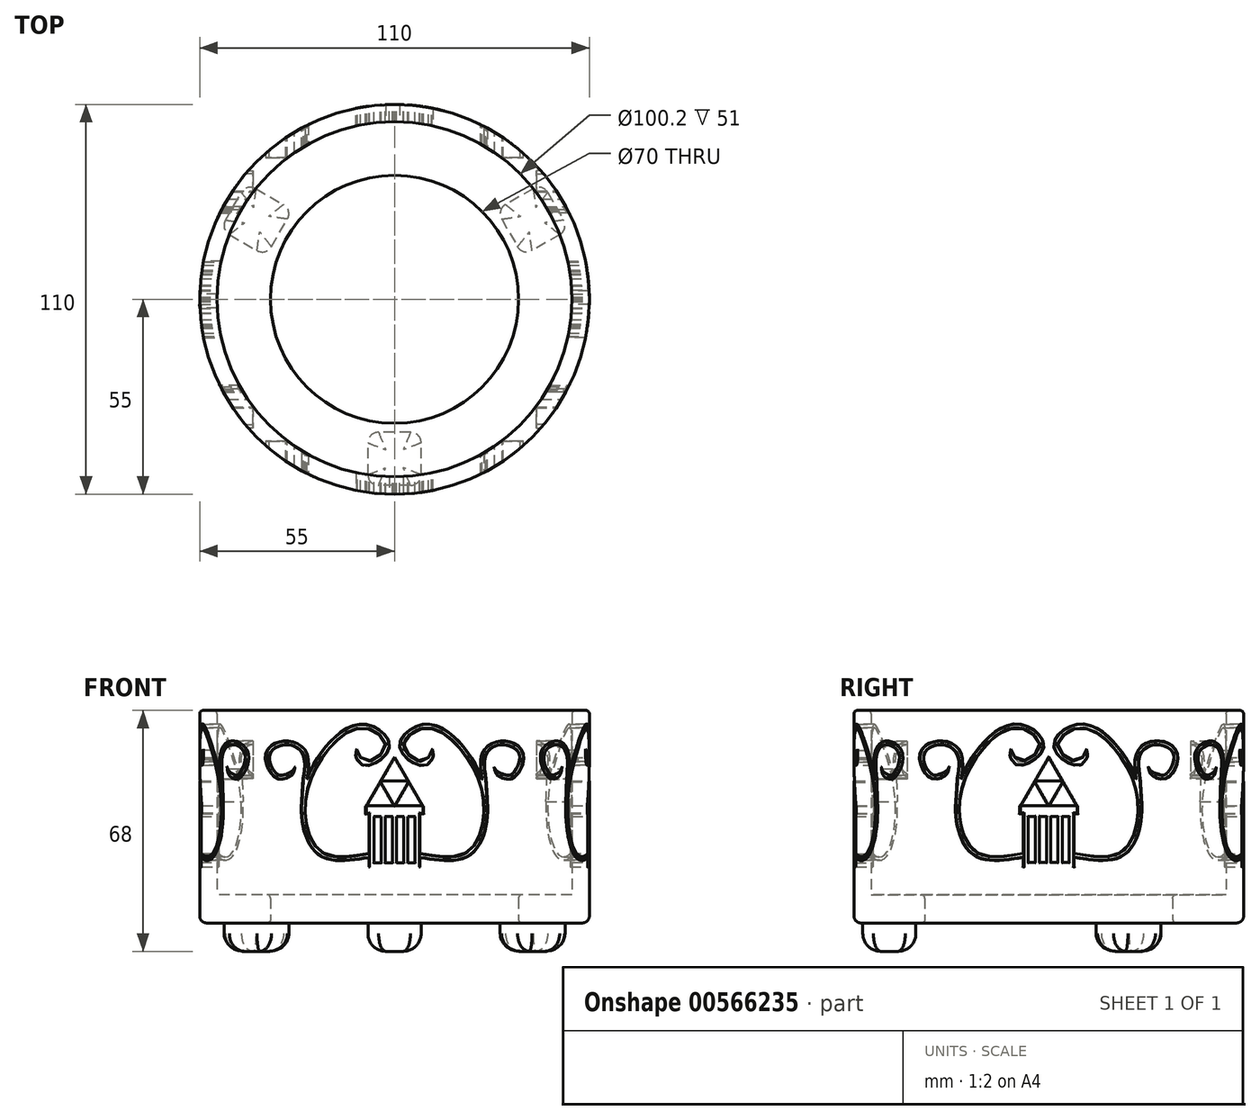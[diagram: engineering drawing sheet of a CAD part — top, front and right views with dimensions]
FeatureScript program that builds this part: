
annotation { "Feature Type Name" : "Feature", "Feature Type Description" : "" }
export const myFeature = defineFeature(function(context is Context, id is Id, definition is map)
    precondition{}
    {
        {
            var Q0;
            Q0=qCreatedBy(makeId("Top.planeOp"),FACE);
            var sketch = newSketch(context, id + "F0", { "sketchPlane" : qUnion([Q0])});
            skCircle(sketch, "E0", {"center": v(0, 0) * mm, "radius": 50.1 * mm});
            skCircle(sketch, "E1", {"center": v(0, 0) * mm, "radius": 55 * mm});
            skCircle(sketch, "E2", {"center": v(0, 0) * mm, "radius": 35 * mm});
            skLineSegment(sketch, "E3", {"start": v(0, -35) * mm, "end": v(0, -45) * mm, "construction": true});
            skLineSegment(sketch, "E4.bottom", {"start": v(4.5, -52.5) * mm, "end": v(-4.5, -52.5) * mm});
            skLineSegment(sketch, "E4.top", {"start": v(4.5, -37.5) * mm, "end": v(-4.5, -37.5) * mm});
            skLineSegment(sketch, "E4.left", {"start": v(7.5, -49.5) * mm, "end": v(7.5, -40.5) * mm});
            skLineSegment(sketch, "E4.right", {"start": v(-7.5, -49.5) * mm, "end": v(-7.5, -40.5) * mm});
            skPoint(sketch, "E4.middle", {"position": v(0, -45) * mm});
            skPoint(sketch, "E5.visualSharp", {"position": v(-7.5, -37.5) * mm});
            skArc(sketch, "E5.filletArc", {"start": v(-4.5, -37.5) * mm, "mid": v(-6.62, -38.38) * mm, "end": v(-7.5, -40.5) * mm});
            skPoint(sketch, "E6.visualSharp", {"position": v(7.5, -37.5) * mm});
            skArc(sketch, "E6.filletArc", {"start": v(7.5, -40.5) * mm, "mid": v(6.62, -38.38) * mm, "end": v(4.5, -37.5) * mm});
            skPoint(sketch, "E7.visualSharp", {"position": v(7.5, -52.5) * mm});
            skArc(sketch, "E7.filletArc", {"start": v(4.5, -52.5) * mm, "mid": v(6.62, -51.62) * mm, "end": v(7.5, -49.5) * mm});
            skPoint(sketch, "E8.visualSharp", {"position": v(-7.5, -52.5) * mm});
            skArc(sketch, "E8.filletArc", {"start": v(-7.5, -49.5) * mm, "mid": v(-6.62, -51.62) * mm, "end": v(-4.5, -52.5) * mm});
            skLineSegment(sketch, "E9.1.0", {"start": v(46.62, 18.25) * mm, "end": v(38.82, 13.75) * mm});
            skArc(sketch, "E9.1.1", {"start": v(34.73, 14.85) * mm, "mid": v(36.55, 13.46) * mm, "end": v(38.82, 13.75) * mm});
            skLineSegment(sketch, "E9.1.2", {"start": v(30.23, 22.65) * mm, "end": v(34.73, 14.85) * mm});
            skArc(sketch, "E9.1.3", {"start": v(31.32, 26.75) * mm, "mid": v(29.93, 24.92) * mm, "end": v(30.23, 22.65) * mm});
            skLineSegment(sketch, "E9.1.4", {"start": v(39.12, 31.25) * mm, "end": v(31.32, 26.75) * mm});
            skArc(sketch, "E9.1.5", {"start": v(43.22, 30.15) * mm, "mid": v(41.4, 31.54) * mm, "end": v(39.12, 31.25) * mm});
            skLineSegment(sketch, "E9.1.6", {"start": v(43.22, 30.15) * mm, "end": v(47.72, 22.35) * mm});
            skArc(sketch, "E9.1.7", {"start": v(46.62, 18.25) * mm, "mid": v(48.02, 20.08) * mm, "end": v(47.72, 22.35) * mm});
            skLineSegment(sketch, "E9.2.0", {"start": v(-39.12, 31.25) * mm, "end": v(-31.32, 26.75) * mm});
            skArc(sketch, "E9.2.1", {"start": v(-30.23, 22.65) * mm, "mid": v(-29.93, 24.92) * mm, "end": v(-31.32, 26.75) * mm});
            skLineSegment(sketch, "E9.2.2", {"start": v(-34.73, 14.85) * mm, "end": v(-30.23, 22.65) * mm});
            skArc(sketch, "E9.2.3", {"start": v(-38.82, 13.75) * mm, "mid": v(-36.55, 13.46) * mm, "end": v(-34.73, 14.85) * mm});
            skLineSegment(sketch, "E9.2.4", {"start": v(-46.62, 18.25) * mm, "end": v(-38.82, 13.75) * mm});
            skArc(sketch, "E9.2.5", {"start": v(-47.72, 22.35) * mm, "mid": v(-48.02, 20.08) * mm, "end": v(-46.62, 18.25) * mm});
            skLineSegment(sketch, "E9.2.6", {"start": v(-47.72, 22.35) * mm, "end": v(-43.22, 30.15) * mm});
            skArc(sketch, "E9.2.7", {"start": v(-39.12, 31.25) * mm, "mid": v(-41.4, 31.54) * mm, "end": v(-43.22, 30.15) * mm});
            skSolve(sketch);
        }
        {
            var Q0;
            Q0=makeQuery(id+"F0.imprint","IMPRINT",FACE,{"disambiguationData":[TD([[makeQuery(id+"F0.imprint","IMPRINT",EDGE,{"derivedFrom":sQuery(id+"F0.wireOp",EDGE,"E0")}),-1.0]])]});
            var Q1;
            {var subQ5=sQuery(id+"F0.wireOp",EDGE,"E9.2.6");Q1=makeQuery(id+"F0.imprint","IMPRINT",FACE,{"disambiguationData":[TD([[makeQuery(id+"F0.imprint","IMPRINT",EDGE,{"derivedFrom":subQ5}),-1.0]])]});}
            var Q2;
            {var subQ5=sQuery(id+"F0.wireOp",EDGE,"E9.1.6");Q2=makeQuery(id+"F0.imprint","IMPRINT",FACE,{"disambiguationData":[TD([[makeQuery(id+"F0.imprint","IMPRINT",EDGE,{"derivedFrom":subQ5}),-1.0]])]});}
            var Q3;
            {var subQ5=sQuery(id+"F0.wireOp",EDGE,"E4.bottom");Q3=makeQuery(id+"F0.imprint","IMPRINT",FACE,{"disambiguationData":[TD([[makeQuery(id+"F0.imprint","IMPRINT",EDGE,{"derivedFrom":subQ5}),-1.0]])]});}
            extrude(context, id + "F1", {"entities" : qUnion([Q0, Q1, Q2, Q3]), "depth" : 60 * mm, "offsetDistance" : 25 * mm});
        }
        {
            var Q0;
            Q0=makeQuery(id+"F0.imprint","IMPRINT",FACE,{"disambiguationData":[TD([[makeQuery(id+"F0.imprint","IMPRINT",EDGE,{"derivedFrom":sQuery(id+"F0.wireOp",EDGE,"E0")}),1.0]])]});
            var Q1;
            {var subQ0=sQuery(id+"F0.wireOp",EDGE,"E9.1.0");Q1=makeQuery(id+"F0.imprint","IMPRINT",FACE,{"disambiguationData":[TD([[makeQuery(id+"F0.imprint","IMPRINT",EDGE,{"derivedFrom":subQ0}),-1.0]])]});}
            var Q2;
            {var subQ0=sQuery(id+"F0.wireOp",EDGE,"E9.2.0");Q2=makeQuery(id+"F0.imprint","IMPRINT",FACE,{"disambiguationData":[TD([[makeQuery(id+"F0.imprint","IMPRINT",EDGE,{"derivedFrom":subQ0}),-1.0]])]});}
            var Q3;
            Q3=makeQuery(id+"F0.imprint","IMPRINT",FACE,{"disambiguationData":[TD([[makeQuery(id+"F0.imprint","IMPRINT",EDGE,{"derivedFrom":sQuery(id+"F0.wireOp",EDGE,"E4.top")}),1.0]])]});
            extrude(context, id + "F2", {"entities" : qUnion([Q0, Q1, Q2, Q3]), "operationType" : NewBodyOperationType.ADD, "depth" : 8 * mm, "offsetDistance" : 25 * mm});
        }
        {
            var Q0;
            Q0=qCreatedBy(makeId("Front.planeOp"),FACE);
            var sketch = newSketch(context, id + "F3", { "sketchPlane" : qUnion([Q0])});
            skLineSegment(sketch, "E10", {"start": v(0, 46.86) * mm, "end": v(4, 39.93) * mm});
            skLineSegment(sketch, "E11", {"start": v(4, 39.93) * mm, "end": v(-4, 39.93) * mm});
            skLineSegment(sketch, "E12", {"start": v(-4, 39.93) * mm, "end": v(0, 46.86) * mm});
            skLineSegment(sketch, "E13", {"start": v(4, 39.93) * mm, "end": v(0, 33) * mm});
            skLineSegment(sketch, "E14", {"start": v(0, 33) * mm, "end": v(8, 33) * mm});
            skLineSegment(sketch, "E15", {"start": v(8, 33) * mm, "end": v(4, 39.93) * mm});
            skLineSegment(sketch, "E16", {"start": v(-4, 39.93) * mm, "end": v(0, 33) * mm});
            skLineSegment(sketch, "E17", {"start": v(-8, 33) * mm, "end": v(-4, 39.93) * mm});
            skLineSegment(sketch, "E18", {"start": v(0, 33) * mm, "end": v(-8, 33) * mm});
            skLineSegment(sketch, "E19", {"start": v(-8, 33) * mm, "end": v(-8, 31) * mm});
            skLineSegment(sketch, "E20", {"start": v(8, 31) * mm, "end": v(8, 33) * mm});
            skLineSegment(sketch, "E21", {"start": v(7, 31) * mm, "end": v(7, 16) * mm});
            skLineSegment(sketch, "E22", {"start": v(7, 16) * mm, "end": v(-7, 16) * mm});
            skLineSegment(sketch, "E23", {"start": v(-7, 16) * mm, "end": v(-7, 31) * mm});
            skLineSegment(sketch, "E24.bottom", {"start": v(5.8, 30) * mm, "end": v(3.8, 30) * mm});
            skLineSegment(sketch, "E24.top", {"start": v(5.8, 17) * mm, "end": v(3.8, 17) * mm});
            skLineSegment(sketch, "E24.left", {"start": v(5.8, 30) * mm, "end": v(5.8, 17) * mm});
            skLineSegment(sketch, "E24.right", {"start": v(3.8, 30) * mm, "end": v(3.8, 17) * mm});
            skLineSegment(sketch, "E25.bottom", {"start": v(2.6, 17) * mm, "end": v(0.6, 17) * mm});
            skLineSegment(sketch, "E25.top", {"start": v(2.6, 30) * mm, "end": v(0.6, 30) * mm});
            skLineSegment(sketch, "E25.left", {"start": v(2.6, 17) * mm, "end": v(2.6, 30) * mm});
            skLineSegment(sketch, "E25.right", {"start": v(0.6, 17) * mm, "end": v(0.6, 30) * mm});
            skLineSegment(sketch, "E26.top", {"start": v(-0.6, 30) * mm, "end": v(-2.6, 30) * mm});
            skLineSegment(sketch, "E26.right", {"start": v(-2.6, 17) * mm, "end": v(-2.6, 30) * mm});
            skLineSegment(sketch, "E27.bottom", {"start": v(-3.8, 17) * mm, "end": v(-5.8, 17) * mm});
            skLineSegment(sketch, "E27.top", {"start": v(-3.8, 30) * mm, "end": v(-5.8, 30) * mm});
            skLineSegment(sketch, "E27.left", {"start": v(-3.8, 17) * mm, "end": v(-3.8, 30) * mm});
            skLineSegment(sketch, "E27.right", {"start": v(-5.8, 17) * mm, "end": v(-5.8, 30) * mm});
            skLineSegment(sketch, "E28", {"start": v(-0.6, 30) * mm, "end": v(-0.6, 17) * mm});
            skLineSegment(sketch, "E29", {"start": v(-0.6, 17) * mm, "end": v(-2.6, 17) * mm});
            skFitSpline(sketch, "E30", {"points": [v(7, 18.58) * mm, v(21.25, 19.27) * mm, v(26.2, 32.82) * mm, v(20.55, 48.14) * mm, v(8.79, 56.05) * mm, v(1.47, 50.51) * mm, v(4.83, 45.57) * mm, v(8.99, 44.58) * mm, v(10.47, 46.16) * mm], "startDerivative": vector(104.29, -16.9) * mm, "endDerivative": vector(19.37, 32.84) * mm});
            skFitSpline(sketch, "E31.0", {"points": [v(7.16, 19.56) * mm, v(8.25, 19.39) * mm, v(10.4, 19.04) * mm, v(13.5, 18.68) * mm, v(15.87, 18.66) * mm, v(17.58, 18.86) * mm, v(18.76, 19.14) * mm, v(19.82, 19.55) * mm, v(20.77, 20.12) * mm, v(21.63, 20.86) * mm, v(22.4, 21.78) * mm, v(23.1, 22.87) * mm, v(23.9, 24.5) * mm, v(24.66, 26.83) * mm, v(25.16, 29.89) * mm, v(25.25, 33) * mm, v(24.95, 36) * mm, v(24.27, 38.89) * mm, v(23.24, 41.67) * mm, v(21.9, 44.36) * mm, v(20.23, 46.96) * mm, v(18.29, 49.47) * mm, v(16.14, 51.74) * mm, v(14.23, 53.25) * mm, v(12.68, 54.16) * mm, v(11.52, 54.66) * mm, v(10.37, 54.98) * mm, v(9.43, 55.08) * mm, v(8.68, 55.05) * mm, v(7.92, 54.95) * mm, v(6.97, 54.7) * mm, v(5.87, 54.23) * mm, v(4.85, 53.6) * mm, v(3.96, 52.88) * mm, v(3.24, 52.1) * mm, v(2.73, 51.3) * mm, v(2.5, 50.68) * mm, v(2.44, 50.25) * mm, v(2.44, 49.83) * mm, v(2.56, 49.3) * mm, v(2.89, 48.64) * mm, v(3.56, 47.75) * mm, v(4.52, 46.94) * mm, v(5.57, 46.28) * mm, v(6.35, 45.9) * mm, v(7.09, 45.62) * mm, v(7.75, 45.47) * mm, v(8.2, 45.44) * mm, v(8.46, 45.47) * mm, v(8.61, 45.5) * mm, v(8.72, 45.55) * mm, v(8.86, 45.64) * mm, v(9.06, 45.82) * mm, v(9.32, 46.18) * mm, v(9.5, 46.5) * mm, v(9.6, 46.67) * mm]});
            skLineSegment(sketch, "E32", {"start": v(7.16, 19.56) * mm, "end": v(7, 19.94) * mm});
            skFitSpline(sketch, "E33", {"points": [v(10.47, 46.16) * mm, v(10.82, 47.06) * mm, v(10.61, 48.76) * mm], "startDerivative": vector(0.97, 1.8) * mm, "endDerivative": vector(-0.49, 2.17) * mm});
            skLineSegment(sketch, "E34", {"start": v(10.61, 48.76) * mm, "end": v(9.6, 46.67) * mm});
            skFitSpline(sketch, "E35", {"points": [v(25.01, 29.21) * mm, v(16.42, 37.92) * mm, v(12, 34.2) * mm, v(11.36, 25.97) * mm, v(17.98, 23.01) * mm, v(21.05, 29.47) * mm, v(15.1, 29.83) * mm], "startDerivative": vector(-33.14, 93.73) * mm, "endDerivative": vector(-8.06, -72.83) * mm});
            skFitSpline(sketch, "E36.0", {"points": [v(24.07, 28.88) * mm, v(23.4, 30.77) * mm, v(21.88, 33.78) * mm, v(19.82, 35.87) * mm, v(18.28, 36.7) * mm, v(17.22, 36.97) * mm, v(16.28, 36.93) * mm, v(15.43, 36.65) * mm, v(14.61, 36.1) * mm, v(13.84, 35.29) * mm, v(13.13, 34.24) * mm, v(12.5, 32.98) * mm, v(12.02, 31.6) * mm, v(11.7, 30.18) * mm, v(11.63, 28.78) * mm, v(11.77, 27.7) * mm, v(12.02, 26.9) * mm, v(12.27, 26.36) * mm, v(12.6, 25.84) * mm, v(13.15, 25.2) * mm, v(14, 24.5) * mm, v(15.16, 23.95) * mm, v(16.17, 23.76) * mm, v(16.95, 23.78) * mm, v(17.52, 23.9) * mm, v(18.07, 24.11) * mm, v(18.62, 24.43) * mm, v(19.14, 24.84) * mm, v(19.75, 25.48) * mm, v(20.22, 26.24) * mm, v(20.47, 27.01) * mm, v(20.55, 27.58) * mm, v(20.52, 28.13) * mm, v(20.36, 28.66) * mm, v(20.07, 29.18) * mm, v(19.6, 29.73) * mm, v(19.01, 30.21) * mm, v(18.35, 30.6) * mm, v(17.7, 30.84) * mm, v(17.12, 30.93) * mm, v(16.78, 30.87) * mm, v(16.6, 30.79) * mm, v(16.48, 30.7) * mm, v(16.37, 30.59) * mm, v(16.22, 30.34) * mm, v(16.13, 30.02) * mm, v(16.1, 29.72) * mm]});
            skFitSpline(sketch, "E37", {"points": [v(15.1, 29.83) * mm, v(15.1, 28.54) * mm, v(15.68, 27.75) * mm], "startDerivative": vector(-0.33, -2.62) * mm, "endDerivative": vector(1.54, -1.53) * mm});
            skLineSegment(sketch, "E38", {"start": v(16.1, 29.72) * mm, "end": v(15.68, 27.75) * mm});
            skLineSegment(sketch, "E39", {"start": v(24.02, 29.03) * mm, "end": v(24.65, 27.14) * mm});
            skFitSpline(sketch, "E40", {"points": [v(24.7, 40.55) * mm, v(25.08, 48.45) * mm, v(30.9, 51.3) * mm, v(36.26, 47.6) * mm, v(33.52, 41.03) * mm, v(30.36, 40.96) * mm], "startDerivative": vector(-5.16, 38.6) * mm, "endDerivative": vector(-21.83, 6.32) * mm});
            skFitSpline(sketch, "E41.0", {"points": [v(25.7, 40.68) * mm, v(25.6, 41.49) * mm, v(25.38, 43.08) * mm, v(25.25, 45.26) * mm, v(25.45, 46.79) * mm, v(25.78, 47.66) * mm, v(26.03, 48.1) * mm, v(26.32, 48.51) * mm, v(26.78, 49) * mm, v(27.7, 49.66) * mm, v(28.8, 50.12) * mm, v(30.03, 50.31) * mm, v(30.96, 50.32) * mm, v(31.9, 50.18) * mm, v(32.82, 49.9) * mm, v(33.64, 49.5) * mm, v(34.33, 48.99) * mm, v(34.86, 48.4) * mm, v(35.15, 47.85) * mm, v(35.29, 47.38) * mm, v(35.36, 46.86) * mm, v(35.34, 46.12) * mm, v(35.13, 45.14) * mm, v(34.76, 44.17) * mm, v(34.27, 43.27) * mm, v(33.8, 42.64) * mm, v(33.44, 42.24) * mm, v(33.17, 42) * mm, v(32.93, 41.84) * mm, v(32.64, 41.7) * mm, v(32.31, 41.62) * mm, v(31.85, 41.62) * mm, v(31.3, 41.73) * mm, v(30.86, 41.85) * mm, v(30.63, 41.92) * mm]});
            skFitSpline(sketch, "E42", {"points": [v(30.36, 40.96) * mm, v(28.83, 41.98) * mm, v(28.24, 43.52) * mm], "startDerivative": vector(-3.42, 1.69) * mm, "endDerivative": vector(-0.79, 3.45) * mm});
            skFitSpline(sketch, "E43", {"points": [v(30.63, 41.92) * mm, v(28.87, 42.76) * mm, v(28.24, 43.52) * mm], "startDerivative": vector(-3.46, 1.32) * mm, "endDerivative": vector(-1.2, 1.92) * mm});
            skLineSegment(sketch, "E44", {"start": v(25.7, 40.68) * mm, "end": v(26.12, 34.19) * mm});
            skLineSegment(sketch, "E45.MirrorCS", {"start": v(-7.16, 19.56) * mm, "end": v(-7, 19.94) * mm});
            skLineSegment(sketch, "E46.MirrorCS", {"start": v(-16.1, 29.72) * mm, "end": v(-15.68, 27.75) * mm});
            skFitSpline(sketch, "E47.MirrorCS", {"points": [v(-15.1, 29.83) * mm, v(-15.1, 28.54) * mm, v(-15.68, 27.75) * mm], "startDerivative": vector(0.33, -2.62) * mm, "endDerivative": vector(-1.54, -1.53) * mm});
            skLineSegment(sketch, "E48.MirrorCS", {"start": v(-24.02, 29.03) * mm, "end": v(-24.65, 27.14) * mm});
            skFitSpline(sketch, "E49.MirrorCS", {"points": [v(-25.01, 29.21) * mm, v(-16.42, 37.92) * mm, v(-12, 34.2) * mm, v(-11.36, 25.97) * mm, v(-17.98, 23.01) * mm, v(-21.05, 29.47) * mm, v(-15.1, 29.83) * mm], "startDerivative": vector(33.14, 93.73) * mm, "endDerivative": vector(8.06, -72.83) * mm});
            skFitSpline(sketch, "E50.MirrorCS", {"points": [v(-10.47, 46.16) * mm, v(-10.82, 47.06) * mm, v(-10.61, 48.76) * mm], "startDerivative": vector(-0.97, 1.8) * mm, "endDerivative": vector(0.49, 2.17) * mm});
            skLineSegment(sketch, "E51.MirrorCS", {"start": v(-25.7, 40.68) * mm, "end": v(-26.12, 34.19) * mm});
            skLineSegment(sketch, "E52.MirrorCS", {"start": v(-10.61, 48.76) * mm, "end": v(-9.6, 46.67) * mm});
            skFitSpline(sketch, "E53.MirrorCS", {"points": [v(-30.36, 40.96) * mm, v(-28.83, 41.98) * mm, v(-28.24, 43.52) * mm], "startDerivative": vector(3.42, 1.69) * mm, "endDerivative": vector(0.79, 3.45) * mm});
            skFitSpline(sketch, "E54.MirrorCS", {"points": [v(-30.63, 41.92) * mm, v(-28.87, 42.76) * mm, v(-28.24, 43.52) * mm], "startDerivative": vector(3.46, 1.32) * mm, "endDerivative": vector(1.2, 1.92) * mm});
            skFitSpline(sketch, "E55.MirrorCS", {"points": [v(-24.7, 40.55) * mm, v(-25.08, 48.45) * mm, v(-30.9, 51.3) * mm, v(-36.26, 47.6) * mm, v(-33.52, 41.03) * mm, v(-30.36, 40.96) * mm], "startDerivative": vector(5.16, 38.6) * mm, "endDerivative": vector(21.83, 6.32) * mm});
            skFitSpline(sketch, "E56.MirrorCS", {"points": [v(-7, 18.58) * mm, v(-21.25, 19.27) * mm, v(-26.2, 32.82) * mm, v(-20.55, 48.14) * mm, v(-8.79, 56.05) * mm, v(-1.47, 50.51) * mm, v(-4.83, 45.57) * mm, v(-8.99, 44.58) * mm, v(-10.47, 46.16) * mm], "startDerivative": vector(-104.29, -16.9) * mm, "endDerivative": vector(-19.37, 32.84) * mm});
            skFitSpline(sketch, "E57.0", {"points": [v(-7.16, 19.56) * mm, v(-8.25, 19.39) * mm, v(-10.4, 19.04) * mm, v(-13.5, 18.68) * mm, v(-15.87, 18.66) * mm, v(-17.58, 18.86) * mm, v(-18.76, 19.14) * mm, v(-19.82, 19.55) * mm, v(-20.77, 20.12) * mm, v(-21.63, 20.86) * mm, v(-22.4, 21.78) * mm, v(-23.1, 22.87) * mm, v(-23.9, 24.5) * mm, v(-24.66, 26.83) * mm, v(-25.16, 29.89) * mm, v(-25.25, 33) * mm, v(-24.95, 36) * mm, v(-24.27, 38.89) * mm, v(-23.24, 41.67) * mm, v(-21.9, 44.36) * mm, v(-20.23, 46.96) * mm, v(-18.29, 49.47) * mm, v(-16.14, 51.74) * mm, v(-14.23, 53.25) * mm, v(-12.68, 54.16) * mm, v(-11.52, 54.66) * mm, v(-10.37, 54.98) * mm, v(-9.43, 55.08) * mm, v(-8.68, 55.05) * mm, v(-7.92, 54.95) * mm, v(-6.97, 54.7) * mm, v(-5.87, 54.23) * mm, v(-4.85, 53.6) * mm, v(-3.96, 52.88) * mm, v(-3.24, 52.1) * mm, v(-2.73, 51.3) * mm, v(-2.5, 50.68) * mm, v(-2.44, 50.25) * mm, v(-2.44, 49.83) * mm, v(-2.56, 49.3) * mm, v(-2.89, 48.64) * mm, v(-3.56, 47.75) * mm, v(-4.52, 46.94) * mm, v(-5.57, 46.28) * mm, v(-6.35, 45.9) * mm, v(-7.09, 45.62) * mm, v(-7.75, 45.47) * mm, v(-8.2, 45.44) * mm, v(-8.46, 45.47) * mm, v(-8.61, 45.5) * mm, v(-8.72, 45.55) * mm, v(-8.86, 45.64) * mm, v(-9.06, 45.82) * mm, v(-9.32, 46.18) * mm, v(-9.5, 46.5) * mm, v(-9.6, 46.67) * mm]});
            skFitSpline(sketch, "E58.0", {"points": [v(-24.07, 28.88) * mm, v(-23.4, 30.77) * mm, v(-21.88, 33.78) * mm, v(-19.82, 35.87) * mm, v(-18.28, 36.7) * mm, v(-17.22, 36.97) * mm, v(-16.28, 36.93) * mm, v(-15.43, 36.65) * mm, v(-14.61, 36.1) * mm, v(-13.84, 35.29) * mm, v(-13.13, 34.24) * mm, v(-12.5, 32.98) * mm, v(-12.02, 31.6) * mm, v(-11.7, 30.18) * mm, v(-11.63, 28.78) * mm, v(-11.77, 27.7) * mm, v(-12.02, 26.9) * mm, v(-12.27, 26.36) * mm, v(-12.6, 25.84) * mm, v(-13.15, 25.2) * mm, v(-14, 24.5) * mm, v(-15.16, 23.95) * mm, v(-16.17, 23.76) * mm, v(-16.95, 23.78) * mm, v(-17.52, 23.9) * mm, v(-18.07, 24.11) * mm, v(-18.62, 24.43) * mm, v(-19.14, 24.84) * mm, v(-19.75, 25.48) * mm, v(-20.22, 26.24) * mm, v(-20.47, 27.01) * mm, v(-20.55, 27.58) * mm, v(-20.52, 28.13) * mm, v(-20.36, 28.66) * mm, v(-20.07, 29.18) * mm, v(-19.6, 29.73) * mm, v(-19.01, 30.21) * mm, v(-18.35, 30.6) * mm, v(-17.7, 30.84) * mm, v(-17.12, 30.93) * mm, v(-16.78, 30.87) * mm, v(-16.6, 30.79) * mm, v(-16.48, 30.7) * mm, v(-16.37, 30.59) * mm, v(-16.22, 30.34) * mm, v(-16.13, 30.02) * mm, v(-16.1, 29.72) * mm]});
            skFitSpline(sketch, "E59.0", {"points": [v(-25.7, 40.68) * mm, v(-25.6, 41.49) * mm, v(-25.38, 43.08) * mm, v(-25.25, 45.26) * mm, v(-25.45, 46.79) * mm, v(-25.78, 47.66) * mm, v(-26.03, 48.1) * mm, v(-26.32, 48.51) * mm, v(-26.78, 49) * mm, v(-27.7, 49.66) * mm, v(-28.8, 50.12) * mm, v(-30.03, 50.31) * mm, v(-30.96, 50.32) * mm, v(-31.9, 50.18) * mm, v(-32.82, 49.9) * mm, v(-33.64, 49.5) * mm, v(-34.33, 48.99) * mm, v(-34.86, 48.4) * mm, v(-35.15, 47.85) * mm, v(-35.29, 47.38) * mm, v(-35.36, 46.86) * mm, v(-35.34, 46.12) * mm, v(-35.13, 45.14) * mm, v(-34.76, 44.17) * mm, v(-34.27, 43.27) * mm, v(-33.8, 42.64) * mm, v(-33.44, 42.24) * mm, v(-33.17, 42) * mm, v(-32.93, 41.84) * mm, v(-32.64, 41.7) * mm, v(-32.31, 41.62) * mm, v(-31.85, 41.62) * mm, v(-31.3, 41.73) * mm, v(-30.86, 41.85) * mm, v(-30.63, 41.92) * mm]});
            skLineSegment(sketch, "E60.0", {"start": v(4, 39.73) * mm, "end": v(0.17, 33.1) * mm});
            skLineSegment(sketch, "E60.1", {"start": v(7.83, 33.1) * mm, "end": v(4, 39.73) * mm});
            skLineSegment(sketch, "E60.2", {"start": v(0.17, 33.1) * mm, "end": v(7.83, 33.1) * mm});
            skLineSegment(sketch, "E61.0", {"start": v(-4, 39.73) * mm, "end": v(-0.17, 33.1) * mm});
            skLineSegment(sketch, "E61.1", {"start": v(-7.83, 33.1) * mm, "end": v(-4, 39.73) * mm});
            skLineSegment(sketch, "E61.2", {"start": v(-0.17, 33.1) * mm, "end": v(-7.83, 33.1) * mm});
            skLineSegment(sketch, "E62.0", {"start": v(3.83, 40.03) * mm, "end": v(-3.83, 40.03) * mm});
            skLineSegment(sketch, "E62.1", {"start": v(0, 46.66) * mm, "end": v(3.83, 40.03) * mm});
            skLineSegment(sketch, "E62.2", {"start": v(-3.83, 40.03) * mm, "end": v(0, 46.66) * mm});
            skLineSegment(sketch, "E63", {"start": v(7, 31) * mm, "end": v(8, 31) * mm});
            skLineSegment(sketch, "E64", {"start": v(-8, 31) * mm, "end": v(-7, 31) * mm});
            skLineSegment(sketch, "E65.0", {"start": v(8.2, 30.8) * mm, "end": v(8.2, 33) * mm});
            skLineSegment(sketch, "E65.1", {"start": v(7.2, 30.8) * mm, "end": v(8.2, 30.8) * mm});
            skLineSegment(sketch, "E65.2", {"start": v(7.2, 30.8) * mm, "end": v(7.2, 15.8) * mm});
            skLineSegment(sketch, "E65.3", {"start": v(-8.2, 33) * mm, "end": v(-8.2, 30.8) * mm});
            skLineSegment(sketch, "E65.4", {"start": v(-8.2, 30.8) * mm, "end": v(-7.2, 30.8) * mm});
            skLineSegment(sketch, "E65.5", {"start": v(-7.2, 15.8) * mm, "end": v(-7.2, 30.8) * mm});
            skLineSegment(sketch, "E65.6", {"start": v(7.2, 15.8) * mm, "end": v(-7.2, 15.8) * mm});
            skLineSegment(sketch, "E66", {"start": v(-8, 33) * mm, "end": v(-8.2, 33) * mm});
            skLineSegment(sketch, "E67", {"start": v(8.2, 33) * mm, "end": v(8, 33) * mm});
            skLineSegment(sketch, "E68", {"start": v(7, 16) * mm, "end": v(7, 15.8) * mm});
            skLineSegment(sketch, "E69", {"start": v(-7, 16) * mm, "end": v(-7, 15.8) * mm});
            skSolve(sketch);
        }
        {
            var Q0;
            {var subQ1=sQuery(id+"F3.wireOp",EDGE,"E51.MirrorCS");Q0=makeQuery(id+"F3.imprint","IMPRINT",FACE,{"disambiguationData":[TD([[makeQuery(id+"F3.imprint","IMPRINT",EDGE,{"derivedFrom":subQ1}),1.0]])]});}
            var Q1;
            {var subQ1=sQuery(id+"F3.wireOp",EDGE,"E45.MirrorCS");Q1=makeQuery(id+"F3.imprint","IMPRINT",FACE,{"disambiguationData":[TD([[makeQuery(id+"F3.imprint","IMPRINT",EDGE,{"derivedFrom":subQ1}),-1.0]])]});}
            var Q2;
            {var subQ3=sQuery(id+"F3.wireOp",EDGE,"E46.MirrorCS");Q2=makeQuery(id+"F3.imprint","IMPRINT",FACE,{"disambiguationData":[TD([[makeQuery(id+"F3.imprint","IMPRINT",EDGE,{"derivedFrom":subQ3}),1.0]])]});}
            var Q3;
            {var subQ6=sQuery(id+"F3.wireOp",EDGE,"E32");Q3=makeQuery(id+"F3.imprint","IMPRINT",FACE,{"disambiguationData":[TD([[makeQuery(id+"F3.imprint","IMPRINT",EDGE,{"derivedFrom":subQ6}),1.0]])]});}
            var Q4;
            {var subQ0=sQuery(id+"F3.wireOp",EDGE,"E40");Q4=makeQuery(id+"F3.imprint","IMPRINT",FACE,{"disambiguationData":[TD([[makeQuery(id+"F3.imprint","IMPRINT",EDGE,{"derivedFrom":subQ0}),-1.0]])]});}
            var Q5;
            {var subQ0=sQuery(id+"F3.wireOp",EDGE,"E35");Q5=makeQuery(id+"F3.imprint","IMPRINT",FACE,{"disambiguationData":[TD([[makeQuery(id+"F3.imprint","IMPRINT",EDGE,{"derivedFrom":subQ0}),1.0]])]});}
            var Q6;
            Q6=makeQuery(id+"F3.imprint","IMPRINT",FACE,{"disambiguationData":[TD([[makeQuery(id+"F3.imprint","IMPRINT",EDGE,{"derivedFrom":sQuery(id+"F3.wireOp",EDGE,"E24.bottom")}),1.0]])]});
            var Q7;
            Q7=makeQuery(id+"F3.imprint","IMPRINT",FACE,{"disambiguationData":[TD([[makeQuery(id+"F3.imprint","IMPRINT",EDGE,{"derivedFrom":sQuery(id+"F3.wireOp",EDGE,"E25.bottom")}),-1.0]])]});
            var Q8;
            Q8=makeQuery(id+"F3.imprint","IMPRINT",FACE,{"disambiguationData":[TD([[makeQuery(id+"F3.imprint","IMPRINT",EDGE,{"derivedFrom":sQuery(id+"F3.wireOp",EDGE,"E26.top")}),1.0]])]});
            var Q9;
            Q9=makeQuery(id+"F3.imprint","IMPRINT",FACE,{"disambiguationData":[TD([[makeQuery(id+"F3.imprint","IMPRINT",EDGE,{"derivedFrom":sQuery(id+"F3.wireOp",EDGE,"E27.bottom")}),-1.0]])]});
            var Q10;
            Q10=makeQuery(id+"F3.imprint","IMPRINT",FACE,{"disambiguationData":[TD([[makeQuery(id+"F3.imprint","IMPRINT",EDGE,{"derivedFrom":sQuery(id+"F3.wireOp",EDGE,"E61.0")}),-1.0]])]});
            var Q11;
            Q11=makeQuery(id+"F3.imprint","IMPRINT",FACE,{"disambiguationData":[TD([[makeQuery(id+"F3.imprint","IMPRINT",EDGE,{"derivedFrom":sQuery(id+"F3.wireOp",EDGE,"E60.0")}),1.0]])]});
            var Q12;
            Q12=makeQuery(id+"F3.imprint","IMPRINT",FACE,{"disambiguationData":[TD([[makeQuery(id+"F3.imprint","IMPRINT",EDGE,{"derivedFrom":sQuery(id+"F3.wireOp",EDGE,"E62.0")}),-1.0]])]});
            var Q13;
            Q13=makeQuery(id+"F3.imprint","IMPRINT",FACE,{"disambiguationData":[TD([[makeQuery(id+"F3.imprint","IMPRINT",EDGE,{"derivedFrom":sQuery(id+"F3.wireOp",EDGE,"E20")}),-1.0]])]});
            var Q14;
            {var subQ9=sQuery(id+"F3.wireOp",EDGE,"E50.MirrorCS");Q14=makeQuery(id+"F3.imprint","IMPRINT",FACE,{"disambiguationData":[TD([[makeQuery(id+"F3.imprint","IMPRINT",EDGE,{"derivedFrom":subQ9}),-1.0]])]});}
            var Q15;
            {var subQ4=sQuery(id+"F3.wireOp",EDGE,"E33");Q15=makeQuery(id+"F3.imprint","IMPRINT",FACE,{"disambiguationData":[TD([[makeQuery(id+"F3.imprint","IMPRINT",EDGE,{"derivedFrom":subQ4}),1.0]])]});}
            var Q16;
            Q16=makeQuery(id+"F3.imprint","IMPRINT",FACE,{"disambiguationData":[TD([[makeQuery(id+"F3.imprint","IMPRINT",EDGE,{"derivedFrom":sQuery(id+"F3.wireOp",EDGE,"E19")}),-1.0]])]});
            var Q17;
            {var subQ3=sQuery(id+"F3.wireOp",EDGE,"E69");Q17=makeQuery(id+"F3.imprint","IMPRINT",FACE,{"disambiguationData":[TD([[makeQuery(id+"F3.imprint","IMPRINT",EDGE,{"derivedFrom":subQ3}),-1.0]])]});}
            var Q18;
            {var subQ3=sQuery(id+"F3.wireOp",EDGE,"E68");Q18=makeQuery(id+"F3.imprint","IMPRINT",FACE,{"disambiguationData":[TD([[makeQuery(id+"F3.imprint","IMPRINT",EDGE,{"derivedFrom":subQ3}),1.0]])]});}
            extrude(context, id + "F4", {"entities" : qUnion([Q0, Q1, Q2, Q3, Q4, Q5, Q6, Q7, Q8, Q9, Q10, Q11, Q12, Q13, Q14, Q15, Q16, Q17, Q18]), "operationType" : NewBodyOperationType.REMOVE, "depth" : 110 * mm, "offsetDistance" : 25 * mm, "hasSecondDirection" : true, "secondDirectionOppositeDirection" : true, "secondDirectionDepth" : 110 * mm});
        }
        {
            var Q0;
            Q0=qCreatedBy(makeId("Right.planeOp"),FACE);
            var sketch = newSketch(context, id + "F5", { "sketchPlane" : qUnion([Q0])});
            skLineSegment(sketch, "E70", {"start": v(0, 46.9) * mm, "end": v(4, 39.97) * mm});
            skLineSegment(sketch, "E71", {"start": v(4, 39.97) * mm, "end": v(-4, 39.97) * mm});
            skLineSegment(sketch, "E72", {"start": v(-4, 39.97) * mm, "end": v(0, 46.9) * mm});
            skLineSegment(sketch, "E73", {"start": v(4, 39.97) * mm, "end": v(0, 33.04) * mm});
            skLineSegment(sketch, "E74", {"start": v(0, 33.04) * mm, "end": v(8, 33.04) * mm});
            skLineSegment(sketch, "E75", {"start": v(8, 33.04) * mm, "end": v(4, 39.97) * mm});
            skLineSegment(sketch, "E76", {"start": v(-4, 39.97) * mm, "end": v(0, 33.04) * mm});
            skLineSegment(sketch, "E77", {"start": v(-8, 33.04) * mm, "end": v(-4, 39.97) * mm});
            skLineSegment(sketch, "E78", {"start": v(0, 33.04) * mm, "end": v(-8, 33.04) * mm});
            skLineSegment(sketch, "E79", {"start": v(-8, 33.04) * mm, "end": v(-8, 31.04) * mm});
            skLineSegment(sketch, "E80", {"start": v(8, 31.04) * mm, "end": v(8, 33.04) * mm});
            skLineSegment(sketch, "E81", {"start": v(7, 31.04) * mm, "end": v(7, 16.04) * mm});
            skLineSegment(sketch, "E82", {"start": v(7, 16.04) * mm, "end": v(-7, 16.04) * mm});
            skLineSegment(sketch, "E83", {"start": v(-7, 16.04) * mm, "end": v(-7, 31.04) * mm});
            skLineSegment(sketch, "E84.bottom", {"start": v(5.8, 30.04) * mm, "end": v(3.8, 30.04) * mm});
            skLineSegment(sketch, "E84.top", {"start": v(5.8, 17.04) * mm, "end": v(3.8, 17.04) * mm});
            skLineSegment(sketch, "E84.left", {"start": v(5.8, 30.04) * mm, "end": v(5.8, 17.04) * mm});
            skLineSegment(sketch, "E84.right", {"start": v(3.8, 30.04) * mm, "end": v(3.8, 17.04) * mm});
            skLineSegment(sketch, "E85.bottom", {"start": v(2.6, 17.04) * mm, "end": v(0.6, 17.04) * mm});
            skLineSegment(sketch, "E85.top", {"start": v(2.6, 30.04) * mm, "end": v(0.6, 30.04) * mm});
            skLineSegment(sketch, "E85.left", {"start": v(2.6, 17.04) * mm, "end": v(2.6, 30.04) * mm});
            skLineSegment(sketch, "E85.right", {"start": v(0.6, 17.04) * mm, "end": v(0.6, 30.04) * mm});
            skLineSegment(sketch, "E86.top", {"start": v(-0.6, 30.04) * mm, "end": v(-2.6, 30.04) * mm});
            skLineSegment(sketch, "E86.right", {"start": v(-2.6, 17.04) * mm, "end": v(-2.6, 30.04) * mm});
            skLineSegment(sketch, "E87.bottom", {"start": v(-3.8, 17.04) * mm, "end": v(-5.8, 17.04) * mm});
            skLineSegment(sketch, "E87.top", {"start": v(-3.8, 30.04) * mm, "end": v(-5.8, 30.04) * mm});
            skLineSegment(sketch, "E87.left", {"start": v(-3.8, 17.04) * mm, "end": v(-3.8, 30.04) * mm});
            skLineSegment(sketch, "E87.right", {"start": v(-5.8, 17.04) * mm, "end": v(-5.8, 30.04) * mm});
            skLineSegment(sketch, "E88", {"start": v(-0.6, 30.04) * mm, "end": v(-0.6, 17.04) * mm});
            skLineSegment(sketch, "E89", {"start": v(-0.6, 17.04) * mm, "end": v(-2.6, 17.04) * mm});
            skFitSpline(sketch, "E90", {"points": [v(7, 18.62) * mm, v(21.24, 19.3) * mm, v(26.19, 32.86) * mm, v(20.55, 48.18) * mm, v(8.78, 56.1) * mm, v(1.47, 50.55) * mm, v(4.83, 45.61) * mm, v(8.98, 44.62) * mm, v(10.47, 46.2) * mm], "startDerivative": vector(104.29, -16.9) * mm, "endDerivative": vector(19.37, 32.84) * mm});
            skFitSpline(sketch, "E91.0", {"points": [v(7.16, 19.6) * mm, v(8.24, 19.43) * mm, v(10.4, 19.08) * mm, v(13.5, 18.72) * mm, v(15.87, 18.7) * mm, v(17.58, 18.9) * mm, v(18.75, 19.18) * mm, v(19.82, 19.6) * mm, v(20.77, 20.16) * mm, v(21.62, 20.9) * mm, v(22.4, 21.82) * mm, v(23.1, 22.9) * mm, v(23.9, 24.54) * mm, v(24.65, 26.87) * mm, v(25.15, 29.93) * mm, v(25.25, 33.05) * mm, v(24.94, 36.04) * mm, v(24.27, 38.93) * mm, v(23.24, 41.71) * mm, v(21.89, 44.4) * mm, v(20.23, 47) * mm, v(18.29, 49.51) * mm, v(16.13, 51.78) * mm, v(14.23, 53.3) * mm, v(12.68, 54.2) * mm, v(11.51, 54.7) * mm, v(10.37, 55.02) * mm, v(9.42, 55.12) * mm, v(8.67, 55.1) * mm, v(7.92, 55) * mm, v(6.97, 54.74) * mm, v(5.87, 54.27) * mm, v(4.85, 53.65) * mm, v(3.95, 52.92) * mm, v(3.23, 52.13) * mm, v(2.73, 51.34) * mm, v(2.5, 50.72) * mm, v(2.44, 50.3) * mm, v(2.44, 49.87) * mm, v(2.56, 49.34) * mm, v(2.89, 48.68) * mm, v(3.56, 47.8) * mm, v(4.52, 46.98) * mm, v(5.57, 46.32) * mm, v(6.34, 45.94) * mm, v(7.08, 45.66) * mm, v(7.74, 45.5) * mm, v(8.19, 45.48) * mm, v(8.46, 45.5) * mm, v(8.6, 45.55) * mm, v(8.72, 45.6) * mm, v(8.86, 45.68) * mm, v(9.05, 45.86) * mm, v(9.31, 46.22) * mm, v(9.5, 46.54) * mm, v(9.6, 46.71) * mm]});
            skLineSegment(sketch, "E92", {"start": v(7.16, 19.6) * mm, "end": v(7, 19.98) * mm});
            skFitSpline(sketch, "E93", {"points": [v(10.47, 46.2) * mm, v(10.82, 47.1) * mm, v(10.6, 48.8) * mm], "startDerivative": vector(0.97, 1.8) * mm, "endDerivative": vector(-0.49, 2.17) * mm});
            skLineSegment(sketch, "E94", {"start": v(10.6, 48.8) * mm, "end": v(9.6, 46.71) * mm});
            skFitSpline(sketch, "E95", {"points": [v(25.01, 29.25) * mm, v(16.41, 37.96) * mm, v(12, 34.24) * mm, v(11.36, 26) * mm, v(17.98, 23.05) * mm, v(21.05, 29.51) * mm, v(15.1, 29.87) * mm], "startDerivative": vector(-33.14, 93.73) * mm, "endDerivative": vector(-8.06, -72.83) * mm});
            skFitSpline(sketch, "E96.0", {"points": [v(24.07, 28.92) * mm, v(23.4, 30.8) * mm, v(21.88, 33.82) * mm, v(19.81, 35.91) * mm, v(18.27, 36.74) * mm, v(17.21, 37) * mm, v(16.28, 36.97) * mm, v(15.43, 36.69) * mm, v(14.61, 36.14) * mm, v(13.83, 35.33) * mm, v(13.13, 34.28) * mm, v(12.5, 33.02) * mm, v(12.01, 31.65) * mm, v(11.7, 30.22) * mm, v(11.62, 28.82) * mm, v(11.76, 27.74) * mm, v(12.01, 26.95) * mm, v(12.27, 26.4) * mm, v(12.6, 25.88) * mm, v(13.15, 25.23) * mm, v(13.99, 24.54) * mm, v(15.15, 23.99) * mm, v(16.16, 23.8) * mm, v(16.95, 23.82) * mm, v(17.52, 23.94) * mm, v(18.07, 24.15) * mm, v(18.62, 24.47) * mm, v(19.13, 24.88) * mm, v(19.75, 25.52) * mm, v(20.21, 26.28) * mm, v(20.47, 27.05) * mm, v(20.55, 27.62) * mm, v(20.51, 28.17) * mm, v(20.36, 28.7) * mm, v(20.07, 29.22) * mm, v(19.6, 29.77) * mm, v(19, 30.25) * mm, v(18.35, 30.64) * mm, v(17.7, 30.88) * mm, v(17.11, 30.97) * mm, v(16.78, 30.91) * mm, v(16.59, 30.83) * mm, v(16.47, 30.75) * mm, v(16.37, 30.63) * mm, v(16.22, 30.38) * mm, v(16.13, 30.06) * mm, v(16.1, 29.76) * mm]});
            skFitSpline(sketch, "E97", {"points": [v(15.1, 29.87) * mm, v(15.1, 28.58) * mm, v(15.68, 27.79) * mm], "startDerivative": vector(-0.33, -2.62) * mm, "endDerivative": vector(1.54, -1.53) * mm});
            skLineSegment(sketch, "E98", {"start": v(16.1, 29.76) * mm, "end": v(15.68, 27.79) * mm});
            skLineSegment(sketch, "E99", {"start": v(24.02, 29.07) * mm, "end": v(24.65, 27.18) * mm});
            skFitSpline(sketch, "E100", {"points": [v(24.7, 40.6) * mm, v(25.07, 48.49) * mm, v(30.9, 51.34) * mm, v(36.25, 47.64) * mm, v(33.51, 41.07) * mm, v(30.35, 41) * mm], "startDerivative": vector(-5.16, 38.6) * mm, "endDerivative": vector(-21.83, 6.32) * mm});
            skFitSpline(sketch, "E101.0", {"points": [v(25.7, 40.72) * mm, v(25.59, 41.53) * mm, v(25.37, 43.12) * mm, v(25.25, 45.3) * mm, v(25.44, 46.83) * mm, v(25.77, 47.7) * mm, v(26.02, 48.14) * mm, v(26.32, 48.56) * mm, v(26.78, 49.04) * mm, v(27.69, 49.7) * mm, v(28.8, 50.16) * mm, v(30.02, 50.35) * mm, v(30.96, 50.36) * mm, v(31.9, 50.22) * mm, v(32.81, 49.95) * mm, v(33.63, 49.54) * mm, v(34.33, 49.03) * mm, v(34.86, 48.44) * mm, v(35.15, 47.89) * mm, v(35.28, 47.42) * mm, v(35.36, 46.9) * mm, v(35.34, 46.16) * mm, v(35.13, 45.19) * mm, v(34.76, 44.21) * mm, v(34.27, 43.3) * mm, v(33.8, 42.68) * mm, v(33.43, 42.28) * mm, v(33.16, 42.04) * mm, v(32.92, 41.88) * mm, v(32.64, 41.74) * mm, v(32.3, 41.66) * mm, v(31.85, 41.66) * mm, v(31.29, 41.77) * mm, v(30.86, 41.9) * mm, v(30.63, 41.96) * mm]});
            skFitSpline(sketch, "E102", {"points": [v(30.35, 41) * mm, v(28.83, 42.02) * mm, v(28.24, 43.56) * mm], "startDerivative": vector(-3.42, 1.69) * mm, "endDerivative": vector(-0.79, 3.45) * mm});
            skFitSpline(sketch, "E103", {"points": [v(30.63, 41.96) * mm, v(28.87, 42.8) * mm, v(28.24, 43.56) * mm], "startDerivative": vector(-3.46, 1.32) * mm, "endDerivative": vector(-1.2, 1.92) * mm});
            skLineSegment(sketch, "E104", {"start": v(25.7, 40.72) * mm, "end": v(26.11, 34.23) * mm});
            skLineSegment(sketch, "E105.MirrorCS", {"start": v(-7.16, 19.6) * mm, "end": v(-7, 19.98) * mm});
            skLineSegment(sketch, "E106.MirrorCS", {"start": v(-16.1, 29.76) * mm, "end": v(-15.69, 27.79) * mm});
            skFitSpline(sketch, "E107.MirrorCS", {"points": [v(-15.1, 29.87) * mm, v(-15.1, 28.58) * mm, v(-15.69, 27.79) * mm], "startDerivative": vector(0.33, -2.62) * mm, "endDerivative": vector(-1.54, -1.53) * mm});
            skLineSegment(sketch, "E108.MirrorCS", {"start": v(-24.02, 29.07) * mm, "end": v(-24.66, 27.18) * mm});
            skFitSpline(sketch, "E109.MirrorCS", {"points": [v(-25.02, 29.25) * mm, v(-16.42, 37.96) * mm, v(-12.01, 34.24) * mm, v(-11.37, 26) * mm, v(-17.98, 23.05) * mm, v(-21.06, 29.51) * mm, v(-15.1, 29.87) * mm], "startDerivative": vector(33.14, 93.73) * mm, "endDerivative": vector(8.06, -72.83) * mm});
            skFitSpline(sketch, "E110.MirrorCS", {"points": [v(-10.47, 46.2) * mm, v(-10.83, 47.1) * mm, v(-10.62, 48.8) * mm], "startDerivative": vector(-0.97, 1.8) * mm, "endDerivative": vector(0.49, 2.17) * mm});
            skLineSegment(sketch, "E111.MirrorCS", {"start": v(-25.7, 40.72) * mm, "end": v(-26.12, 34.23) * mm});
            skLineSegment(sketch, "E112.MirrorCS", {"start": v(-10.62, 48.8) * mm, "end": v(-9.61, 46.71) * mm});
            skFitSpline(sketch, "E113.MirrorCS", {"points": [v(-30.36, 41) * mm, v(-28.84, 42.02) * mm, v(-28.25, 43.56) * mm], "startDerivative": vector(3.42, 1.69) * mm, "endDerivative": vector(0.79, 3.45) * mm});
            skFitSpline(sketch, "E114.MirrorCS", {"points": [v(-30.64, 41.96) * mm, v(-28.88, 42.8) * mm, v(-28.25, 43.56) * mm], "startDerivative": vector(3.46, 1.32) * mm, "endDerivative": vector(1.2, 1.92) * mm});
            skFitSpline(sketch, "E115.MirrorCS", {"points": [v(-24.71, 40.6) * mm, v(-25.08, 48.49) * mm, v(-30.9, 51.34) * mm, v(-36.26, 47.64) * mm, v(-33.52, 41.07) * mm, v(-30.36, 41) * mm], "startDerivative": vector(5.16, 38.6) * mm, "endDerivative": vector(21.83, 6.32) * mm});
            skFitSpline(sketch, "E116.MirrorCS", {"points": [v(-7, 18.62) * mm, v(-21.25, 19.3) * mm, v(-26.2, 32.86) * mm, v(-20.56, 48.18) * mm, v(-8.8, 56.1) * mm, v(-1.48, 50.55) * mm, v(-4.84, 45.61) * mm, v(-9, 44.62) * mm, v(-10.47, 46.2) * mm], "startDerivative": vector(-104.29, -16.9) * mm, "endDerivative": vector(-19.37, 32.84) * mm});
            skFitSpline(sketch, "E117.0", {"points": [v(-7.16, 19.6) * mm, v(-8.25, 19.43) * mm, v(-10.4, 19.08) * mm, v(-13.5, 18.72) * mm, v(-15.87, 18.7) * mm, v(-17.59, 18.9) * mm, v(-18.76, 19.18) * mm, v(-19.83, 19.6) * mm, v(-20.77, 20.16) * mm, v(-21.63, 20.9) * mm, v(-22.41, 21.82) * mm, v(-23.1, 22.9) * mm, v(-23.9, 24.54) * mm, v(-24.66, 26.87) * mm, v(-25.16, 29.93) * mm, v(-25.26, 33.05) * mm, v(-24.95, 36.04) * mm, v(-24.27, 38.93) * mm, v(-23.25, 41.71) * mm, v(-21.9, 44.4) * mm, v(-20.24, 47) * mm, v(-18.3, 49.51) * mm, v(-16.14, 51.78) * mm, v(-14.23, 53.3) * mm, v(-12.68, 54.2) * mm, v(-11.52, 54.7) * mm, v(-10.37, 55.02) * mm, v(-9.43, 55.12) * mm, v(-8.68, 55.1) * mm, v(-7.93, 55) * mm, v(-6.98, 54.74) * mm, v(-5.87, 54.27) * mm, v(-4.85, 53.65) * mm, v(-3.96, 52.92) * mm, v(-3.24, 52.13) * mm, v(-2.73, 51.34) * mm, v(-2.5, 50.72) * mm, v(-2.45, 50.3) * mm, v(-2.45, 49.87) * mm, v(-2.56, 49.34) * mm, v(-2.9, 48.68) * mm, v(-3.57, 47.8) * mm, v(-4.52, 46.98) * mm, v(-5.57, 46.32) * mm, v(-6.35, 45.94) * mm, v(-7.1, 45.66) * mm, v(-7.75, 45.5) * mm, v(-8.2, 45.48) * mm, v(-8.46, 45.5) * mm, v(-8.62, 45.55) * mm, v(-8.72, 45.6) * mm, v(-8.87, 45.68) * mm, v(-9.06, 45.86) * mm, v(-9.32, 46.22) * mm, v(-9.51, 46.54) * mm, v(-9.61, 46.71) * mm]});
            skFitSpline(sketch, "E118.0", {"points": [v(-24.08, 28.92) * mm, v(-23.4, 30.8) * mm, v(-21.88, 33.82) * mm, v(-19.82, 35.91) * mm, v(-18.28, 36.74) * mm, v(-17.22, 37) * mm, v(-16.29, 36.97) * mm, v(-15.44, 36.69) * mm, v(-14.62, 36.14) * mm, v(-13.84, 35.33) * mm, v(-13.13, 34.28) * mm, v(-12.51, 33.02) * mm, v(-12.02, 31.65) * mm, v(-11.71, 30.22) * mm, v(-11.63, 28.82) * mm, v(-11.77, 27.74) * mm, v(-12.02, 26.95) * mm, v(-12.28, 26.4) * mm, v(-12.61, 25.88) * mm, v(-13.16, 25.23) * mm, v(-14, 24.54) * mm, v(-15.16, 23.99) * mm, v(-16.17, 23.8) * mm, v(-16.96, 23.82) * mm, v(-17.52, 23.94) * mm, v(-18.08, 24.15) * mm, v(-18.63, 24.47) * mm, v(-19.14, 24.88) * mm, v(-19.76, 25.52) * mm, v(-20.22, 26.28) * mm, v(-20.47, 27.05) * mm, v(-20.55, 27.62) * mm, v(-20.52, 28.17) * mm, v(-20.37, 28.7) * mm, v(-20.08, 29.22) * mm, v(-19.6, 29.77) * mm, v(-19.01, 30.25) * mm, v(-18.35, 30.64) * mm, v(-17.7, 30.88) * mm, v(-17.12, 30.97) * mm, v(-16.78, 30.91) * mm, v(-16.6, 30.83) * mm, v(-16.48, 30.75) * mm, v(-16.37, 30.63) * mm, v(-16.23, 30.38) * mm, v(-16.13, 30.06) * mm, v(-16.1, 29.76) * mm]});
            skFitSpline(sketch, "E119.0", {"points": [v(-25.7, 40.72) * mm, v(-25.6, 41.53) * mm, v(-25.38, 43.12) * mm, v(-25.26, 45.3) * mm, v(-25.45, 46.83) * mm, v(-25.78, 47.7) * mm, v(-26.03, 48.14) * mm, v(-26.33, 48.56) * mm, v(-26.79, 49.04) * mm, v(-27.7, 49.7) * mm, v(-28.81, 50.16) * mm, v(-30.03, 50.35) * mm, v(-30.97, 50.36) * mm, v(-31.91, 50.22) * mm, v(-32.82, 49.95) * mm, v(-33.64, 49.54) * mm, v(-34.34, 49.03) * mm, v(-34.87, 48.44) * mm, v(-35.16, 47.89) * mm, v(-35.3, 47.42) * mm, v(-35.37, 46.9) * mm, v(-35.35, 46.16) * mm, v(-35.13, 45.19) * mm, v(-34.76, 44.21) * mm, v(-34.28, 43.3) * mm, v(-33.81, 42.68) * mm, v(-33.44, 42.28) * mm, v(-33.17, 42.04) * mm, v(-32.93, 41.88) * mm, v(-32.65, 41.74) * mm, v(-32.32, 41.66) * mm, v(-31.85, 41.66) * mm, v(-31.3, 41.77) * mm, v(-30.87, 41.9) * mm, v(-30.64, 41.96) * mm]});
            skLineSegment(sketch, "E120.0", {"start": v(4, 39.77) * mm, "end": v(0.17, 33.14) * mm});
            skLineSegment(sketch, "E120.1", {"start": v(7.82, 33.14) * mm, "end": v(4, 39.77) * mm});
            skLineSegment(sketch, "E120.2", {"start": v(0.17, 33.14) * mm, "end": v(7.82, 33.14) * mm});
            skLineSegment(sketch, "E121.0", {"start": v(-4, 39.77) * mm, "end": v(-0.18, 33.14) * mm});
            skLineSegment(sketch, "E121.1", {"start": v(-7.83, 33.14) * mm, "end": v(-4, 39.77) * mm});
            skLineSegment(sketch, "E121.2", {"start": v(-0.18, 33.14) * mm, "end": v(-7.83, 33.14) * mm});
            skLineSegment(sketch, "E122.0", {"start": v(3.82, 40.07) * mm, "end": v(-3.83, 40.07) * mm});
            skLineSegment(sketch, "E122.1", {"start": v(0, 46.7) * mm, "end": v(3.82, 40.07) * mm});
            skLineSegment(sketch, "E122.2", {"start": v(-3.83, 40.07) * mm, "end": v(0, 46.7) * mm});
            skLineSegment(sketch, "E123", {"start": v(7, 31.04) * mm, "end": v(8, 31.04) * mm});
            skLineSegment(sketch, "E124", {"start": v(-8, 31.04) * mm, "end": v(-7, 31.04) * mm});
            skLineSegment(sketch, "E125.0", {"start": v(8.2, 30.84) * mm, "end": v(8.2, 33.04) * mm});
            skLineSegment(sketch, "E125.1", {"start": v(7.2, 30.84) * mm, "end": v(8.2, 30.84) * mm});
            skLineSegment(sketch, "E125.2", {"start": v(7.2, 30.84) * mm, "end": v(7.2, 15.84) * mm});
            skLineSegment(sketch, "E125.3", {"start": v(-8.2, 33.04) * mm, "end": v(-8.2, 30.84) * mm});
            skLineSegment(sketch, "E125.4", {"start": v(-8.2, 30.84) * mm, "end": v(-7.2, 30.84) * mm});
            skLineSegment(sketch, "E125.5", {"start": v(-7.2, 15.84) * mm, "end": v(-7.2, 30.84) * mm});
            skLineSegment(sketch, "E125.6", {"start": v(7.2, 15.84) * mm, "end": v(-7.2, 15.84) * mm});
            skLineSegment(sketch, "E126", {"start": v(-8, 33.04) * mm, "end": v(-8.2, 33.04) * mm});
            skLineSegment(sketch, "E127", {"start": v(8.2, 33.04) * mm, "end": v(8, 33.04) * mm});
            skLineSegment(sketch, "E128", {"start": v(7, 16.04) * mm, "end": v(7, 15.84) * mm});
            skLineSegment(sketch, "E129", {"start": v(-7, 16.04) * mm, "end": v(-7, 15.84) * mm});
            skSolve(sketch);
        }
        {
            var Q0;
            {var subQ0=sQuery(id+"F5.wireOp",EDGE,"E100");Q0=makeQuery(id+"F5.imprint","IMPRINT",FACE,{"disambiguationData":[TD([[makeQuery(id+"F5.imprint","IMPRINT",EDGE,{"derivedFrom":subQ0}),-1.0]])]});}
            var Q1;
            {var subQ4=sQuery(id+"F5.wireOp",EDGE,"E93");Q1=makeQuery(id+"F5.imprint","IMPRINT",FACE,{"disambiguationData":[TD([[makeQuery(id+"F5.imprint","IMPRINT",EDGE,{"derivedFrom":subQ4}),1.0]])]});}
            var Q2;
            {var subQ0=sQuery(id+"F5.wireOp",EDGE,"E95");Q2=makeQuery(id+"F5.imprint","IMPRINT",FACE,{"disambiguationData":[TD([[makeQuery(id+"F5.imprint","IMPRINT",EDGE,{"derivedFrom":subQ0}),1.0]])]});}
            var Q3;
            {var subQ9=sQuery(id+"F5.wireOp",EDGE,"E110.MirrorCS");Q3=makeQuery(id+"F5.imprint","IMPRINT",FACE,{"disambiguationData":[TD([[makeQuery(id+"F5.imprint","IMPRINT",EDGE,{"derivedFrom":subQ9}),-1.0]])]});}
            var Q4;
            {var subQ2=sQuery(id+"F5.wireOp",EDGE,"E106.MirrorCS");Q4=makeQuery(id+"F5.imprint","IMPRINT",FACE,{"disambiguationData":[TD([[makeQuery(id+"F5.imprint","IMPRINT",EDGE,{"derivedFrom":subQ2}),1.0]])]});}
            var Q5;
            {var subQ1=sQuery(id+"F5.wireOp",EDGE,"E111.MirrorCS");Q5=makeQuery(id+"F5.imprint","IMPRINT",FACE,{"disambiguationData":[TD([[makeQuery(id+"F5.imprint","IMPRINT",EDGE,{"derivedFrom":subQ1}),1.0]])]});}
            var Q6;
            Q6=makeQuery(id+"F5.imprint","IMPRINT",FACE,{"disambiguationData":[TD([[makeQuery(id+"F5.imprint","IMPRINT",EDGE,{"derivedFrom":sQuery(id+"F5.wireOp",EDGE,"E122.0")}),-1.0]])]});
            var Q7;
            Q7=makeQuery(id+"F5.imprint","IMPRINT",FACE,{"disambiguationData":[TD([[makeQuery(id+"F5.imprint","IMPRINT",EDGE,{"derivedFrom":sQuery(id+"F5.wireOp",EDGE,"E120.0")}),1.0]])]});
            var Q8;
            Q8=makeQuery(id+"F5.imprint","IMPRINT",FACE,{"disambiguationData":[TD([[makeQuery(id+"F5.imprint","IMPRINT",EDGE,{"derivedFrom":sQuery(id+"F5.wireOp",EDGE,"E121.0")}),-1.0]])]});
            var Q9;
            Q9=makeQuery(id+"F5.imprint","IMPRINT",FACE,{"disambiguationData":[TD([[makeQuery(id+"F5.imprint","IMPRINT",EDGE,{"derivedFrom":sQuery(id+"F5.wireOp",EDGE,"E80")}),-1.0]])]});
            var Q10;
            Q10=makeQuery(id+"F5.imprint","IMPRINT",FACE,{"disambiguationData":[TD([[makeQuery(id+"F5.imprint","IMPRINT",EDGE,{"derivedFrom":sQuery(id+"F5.wireOp",EDGE,"E79")}),-1.0]])]});
            var Q11;
            Q11=makeQuery(id+"F5.imprint","IMPRINT",FACE,{"disambiguationData":[TD([[makeQuery(id+"F5.imprint","IMPRINT",EDGE,{"derivedFrom":sQuery(id+"F5.wireOp",EDGE,"E87.bottom")}),-1.0]])]});
            var Q12;
            Q12=makeQuery(id+"F5.imprint","IMPRINT",FACE,{"disambiguationData":[TD([[makeQuery(id+"F5.imprint","IMPRINT",EDGE,{"derivedFrom":sQuery(id+"F5.wireOp",EDGE,"E86.top")}),1.0]])]});
            var Q13;
            Q13=makeQuery(id+"F5.imprint","IMPRINT",FACE,{"disambiguationData":[TD([[makeQuery(id+"F5.imprint","IMPRINT",EDGE,{"derivedFrom":sQuery(id+"F5.wireOp",EDGE,"E85.bottom")}),-1.0]])]});
            var Q14;
            Q14=makeQuery(id+"F5.imprint","IMPRINT",FACE,{"disambiguationData":[TD([[makeQuery(id+"F5.imprint","IMPRINT",EDGE,{"derivedFrom":sQuery(id+"F5.wireOp",EDGE,"E84.bottom")}),1.0]])]});
            var Q15;
            {var subQ3=sQuery(id+"F5.wireOp",EDGE,"E128");Q15=makeQuery(id+"F5.imprint","IMPRINT",FACE,{"disambiguationData":[TD([[makeQuery(id+"F5.imprint","IMPRINT",EDGE,{"derivedFrom":subQ3}),1.0]])]});}
            var Q16;
            {var subQ0=sQuery(id+"F5.wireOp",EDGE,"E92");Q16=makeQuery(id+"F5.imprint","IMPRINT",FACE,{"disambiguationData":[TD([[makeQuery(id+"F5.imprint","IMPRINT",EDGE,{"derivedFrom":subQ0}),1.0]])]});}
            var Q17;
            {var subQ1=sQuery(id+"F5.wireOp",EDGE,"E105.MirrorCS");Q17=makeQuery(id+"F5.imprint","IMPRINT",FACE,{"disambiguationData":[TD([[makeQuery(id+"F5.imprint","IMPRINT",EDGE,{"derivedFrom":subQ1}),-1.0]])]});}
            var Q18;
            {var subQ3=sQuery(id+"F5.wireOp",EDGE,"E129");Q18=makeQuery(id+"F5.imprint","IMPRINT",FACE,{"disambiguationData":[TD([[makeQuery(id+"F5.imprint","IMPRINT",EDGE,{"derivedFrom":subQ3}),-1.0]])]});}
            extrude(context, id + "F6", {"entities" : qUnion([Q0, Q1, Q2, Q3, Q4, Q5, Q6, Q7, Q8, Q9, Q10, Q11, Q12, Q13, Q14, Q15, Q16, Q17, Q18]), "operationType" : NewBodyOperationType.REMOVE, "oppositeDirection" : true, "depth" : 110 * mm, "offsetDistance" : 25 * mm, "hasSecondDirection" : true, "secondDirectionOppositeDirection" : false, "secondDirectionDepth" : 110 * mm});
        }
        {
            var Q0;
            Q0=makeQuery(id+"F0.imprint","IMPRINT",FACE,{"disambiguationData":[TD([[makeQuery(id+"F0.imprint","IMPRINT",EDGE,{"derivedFrom":sQuery(id+"F0.wireOp",EDGE,"E4.top")}),1.0]])]});
            var Q1;
            {var subQ5=sQuery(id+"F0.wireOp",EDGE,"E4.bottom");Q1=makeQuery(id+"F0.imprint","IMPRINT",FACE,{"disambiguationData":[TD([[makeQuery(id+"F0.imprint","IMPRINT",EDGE,{"derivedFrom":subQ5}),-1.0]])]});}
            var Q2;
            {var subQ0=sQuery(id+"F0.wireOp",EDGE,"E9.1.0");Q2=makeQuery(id+"F0.imprint","IMPRINT",FACE,{"disambiguationData":[TD([[makeQuery(id+"F0.imprint","IMPRINT",EDGE,{"derivedFrom":subQ0}),-1.0]])]});}
            var Q3;
            {var subQ5=sQuery(id+"F0.wireOp",EDGE,"E9.1.6");Q3=makeQuery(id+"F0.imprint","IMPRINT",FACE,{"disambiguationData":[TD([[makeQuery(id+"F0.imprint","IMPRINT",EDGE,{"derivedFrom":subQ5}),-1.0]])]});}
            var Q4;
            {var subQ0=sQuery(id+"F0.wireOp",EDGE,"E9.2.0");Q4=makeQuery(id+"F0.imprint","IMPRINT",FACE,{"disambiguationData":[TD([[makeQuery(id+"F0.imprint","IMPRINT",EDGE,{"derivedFrom":subQ0}),-1.0]])]});}
            var Q5;
            {var subQ5=sQuery(id+"F0.wireOp",EDGE,"E9.2.6");Q5=makeQuery(id+"F0.imprint","IMPRINT",FACE,{"disambiguationData":[TD([[makeQuery(id+"F0.imprint","IMPRINT",EDGE,{"derivedFrom":subQ5}),-1.0]])]});}
            extrude(context, id + "F7", {"entities" : qUnion([Q0, Q1, Q2, Q3, Q4, Q5]), "operationType" : NewBodyOperationType.ADD, "oppositeDirection" : true, "depth" : 8 * mm, "offsetDistance" : 25 * mm});
        }
        {
            var Q0;
            Q0=makeQuery(id+"F7.opExtrude","CAP_FACE",FACE,{"disambiguationData":[OSD([sQuery(id+"F0.wireOp",EDGE,"E4.bottom"),sQuery(id+"F0.wireOp",EDGE,"E4.top"),sQuery(id+"F0.wireOp",EDGE,"E4.left"),sQuery(id+"F0.wireOp",EDGE,"E4.right"),sQuery(id+"F0.wireOp",EDGE,"E5.filletArc"),sQuery(id+"F0.wireOp",EDGE,"E6.filletArc"),sQuery(id+"F0.wireOp",EDGE,"E7.filletArc"),sQuery(id+"F0.wireOp",EDGE,"E8.filletArc")])],"isStart":false});
            var Q1;
            Q1=makeQuery(id+"F7.opExtrude","CAP_FACE",FACE,{"disambiguationData":[OSD([sQuery(id+"F0.wireOp",EDGE,"E9.1.0"),sQuery(id+"F0.wireOp",EDGE,"E9.1.1"),sQuery(id+"F0.wireOp",EDGE,"E9.1.2"),sQuery(id+"F0.wireOp",EDGE,"E9.1.3"),sQuery(id+"F0.wireOp",EDGE,"E9.1.4"),sQuery(id+"F0.wireOp",EDGE,"E9.1.5"),sQuery(id+"F0.wireOp",EDGE,"E9.1.6"),sQuery(id+"F0.wireOp",EDGE,"E9.1.7")])],"isStart":false});
            var Q2;
            Q2=makeQuery(id+"F7.opExtrude","CAP_FACE",FACE,{"disambiguationData":[OSD([sQuery(id+"F0.wireOp",EDGE,"E9.2.0"),sQuery(id+"F0.wireOp",EDGE,"E9.2.1"),sQuery(id+"F0.wireOp",EDGE,"E9.2.2"),sQuery(id+"F0.wireOp",EDGE,"E9.2.3"),sQuery(id+"F0.wireOp",EDGE,"E9.2.4"),sQuery(id+"F0.wireOp",EDGE,"E9.2.5"),sQuery(id+"F0.wireOp",EDGE,"E9.2.6"),sQuery(id+"F0.wireOp",EDGE,"E9.2.7")])],"isStart":false});
            fillet(context, id + "F8", {"entities" : qUnion([Q0, Q1, Q2]), "radius" : 5 * mm, "tangentPropagation" : true, "allowEdgeOverflow" : false});
        }
        {
            var Q0;
            Q0=makeQuery(id+"F1.opExtrude","CAP_EDGE",EDGE,{"disambiguationData":[OSD([sQuery(id+"F0.wireOp",EDGE,"E1")])],"isStart":false});
            var Q1;
            Q1=makeQuery(id+"F1.opExtrude","CAP_EDGE",EDGE,{"disambiguationData":[OSD([sQuery(id+"F0.wireOp",EDGE,"E0")])],"isStart":false});
            var Q2;
            Q2=makeQuery(id+"F2.opExtrude","CAP_EDGE",EDGE,{"disambiguationData":[OSD([sQuery(id+"F0.wireOp",EDGE,"E2")])],"isStart":true});
            fillet(context, id + "F9", {"entities" : qUnion([Q0, Q1, Q2]), "radius" : 1 * mm, "tangentPropagation" : true, "allowEdgeOverflow" : false});
        }
        {
            var Q0;
            Q0=makeQuery(id+"F1.opExtrude","CAP_EDGE",EDGE,{"disambiguationData":[OSD([sQuery(id+"F0.wireOp",EDGE,"E1")])],"isStart":true});
            fillet(context, id + "F10", {"entities" : qUnion([Q0]), "radius" : 2 * mm, "tangentPropagation" : true, "allowEdgeOverflow" : false});
        }
        {
            var Q0;
            {var subQ0=sQuery(id+"F3.wireOp",EDGE,"E56.MirrorCS");Q0=makeQuery(id+"F4.boolean.opBoolean","INTERSECT",EDGE,{"disambiguationData":[OD(0.0)],"derivedFrom":[makeQuery(id+"F1.opExtrude","SWEPT_FACE",FACE,{"disambiguationData":[OSD([sQuery(id+"F0.wireOp",EDGE,"E1")])]}),makeQuery(id+"F4.opExtrude","SWEPT_FACE",FACE,{"disambiguationData":[OSD([subQ0]),TDD([makeQuery(id+"F3.imprint","IMPRINT",EDGE,{"disambiguationData":[TD([[makeQuery(id+"F3.imprint","INTERSECT",VERTEX,{"derivedFrom":[sQuery(id+"F3.wireOp",EDGE,"E50.MirrorCS"),subQ0]}),1.0]])],"derivedFrom":subQ0})])]})]});}
            var Q1;
            {var subQ0=sQuery(id+"F3.wireOp",EDGE,"E57.0");Q1=makeQuery(id+"F4.boolean.opBoolean","INTERSECT",EDGE,{"disambiguationData":[OD(0.0)],"derivedFrom":[makeQuery(id+"F1.opExtrude","SWEPT_FACE",FACE,{"disambiguationData":[OSD([sQuery(id+"F0.wireOp",EDGE,"E1")])]}),makeQuery(id+"F4.opExtrude","SWEPT_FACE",FACE,{"disambiguationData":[OSD([subQ0]),TDD([makeQuery(id+"F3.imprint","IMPRINT",EDGE,{"disambiguationData":[TD([[makeQuery(id+"F3.imprint","INTERSECT",VERTEX,{"derivedFrom":[sQuery(id+"F3.wireOp",EDGE,"E49.MirrorCS"),subQ0]}),-1.0]])],"derivedFrom":subQ0})])]})]});}
            var Q2;
            Q2=makeQuery(id+"F4.boolean.opBoolean","INTERSECT",EDGE,{"disambiguationData":[OD(0.0)],"derivedFrom":[makeQuery(id+"F1.opExtrude","SWEPT_FACE",FACE,{"disambiguationData":[OSD([sQuery(id+"F0.wireOp",EDGE,"E1")])]}),makeQuery(id+"F4.opExtrude","SWEPT_FACE",FACE,{"disambiguationData":[OSD([sQuery(id+"F3.wireOp",EDGE,"E55.MirrorCS")])]})]});
            var Q3;
            Q3=makeQuery(id+"F4.boolean.opBoolean","INTERSECT",EDGE,{"disambiguationData":[OD(0.0)],"derivedFrom":[makeQuery(id+"F1.opExtrude","SWEPT_FACE",FACE,{"disambiguationData":[OSD([sQuery(id+"F0.wireOp",EDGE,"E1")])]}),makeQuery(id+"F4.opExtrude","SWEPT_FACE",FACE,{"disambiguationData":[OSD([sQuery(id+"F3.wireOp",EDGE,"E59.0")])]})]});
            var Q4;
            Q4=makeQuery(id+"F4.boolean.opBoolean","INTERSECT",EDGE,{"disambiguationData":[OD(0.0)],"derivedFrom":[makeQuery(id+"F1.opExtrude","SWEPT_FACE",FACE,{"disambiguationData":[OSD([sQuery(id+"F0.wireOp",EDGE,"E1")])]}),makeQuery(id+"F4.opExtrude","SWEPT_FACE",FACE,{"disambiguationData":[OSD([sQuery(id+"F3.wireOp",EDGE,"E54.MirrorCS")])]})]});
            var Q5;
            Q5=makeQuery(id+"F4.boolean.opBoolean","INTERSECT",EDGE,{"disambiguationData":[OD(0.0)],"derivedFrom":[makeQuery(id+"F1.opExtrude","SWEPT_FACE",FACE,{"disambiguationData":[OSD([sQuery(id+"F0.wireOp",EDGE,"E1")])]}),makeQuery(id+"F4.opExtrude","SWEPT_FACE",FACE,{"disambiguationData":[OSD([sQuery(id+"F3.wireOp",EDGE,"E53.MirrorCS")])]})]});
            var Q6;
            Q6=makeQuery(id+"F4.boolean.opBoolean","INTERSECT",EDGE,{"disambiguationData":[OD(0.0)],"derivedFrom":[makeQuery(id+"F1.opExtrude","SWEPT_FACE",FACE,{"disambiguationData":[OSD([sQuery(id+"F0.wireOp",EDGE,"E1")])]}),makeQuery(id+"F4.opExtrude","SWEPT_FACE",FACE,{"disambiguationData":[OSD([sQuery(id+"F3.wireOp",EDGE,"E50.MirrorCS")])]})]});
            var Q7;
            Q7=makeQuery(id+"F4.boolean.opBoolean","INTERSECT",EDGE,{"disambiguationData":[OD(0.0)],"derivedFrom":[makeQuery(id+"F1.opExtrude","SWEPT_FACE",FACE,{"disambiguationData":[OSD([sQuery(id+"F0.wireOp",EDGE,"E1")])]}),makeQuery(id+"F4.opExtrude","SWEPT_FACE",FACE,{"disambiguationData":[OSD([sQuery(id+"F3.wireOp",EDGE,"E52.MirrorCS")])]})]});
            var Q8;
            {var subQ0=sQuery(id+"F3.wireOp",EDGE,"E56.MirrorCS");Q8=makeQuery(id+"F4.boolean.opBoolean","INTERSECT",EDGE,{"disambiguationData":[OD(0.0)],"derivedFrom":[makeQuery(id+"F1.opExtrude","SWEPT_FACE",FACE,{"disambiguationData":[OSD([sQuery(id+"F0.wireOp",EDGE,"E1")])]}),makeQuery(id+"F4.opExtrude","SWEPT_FACE",FACE,{"disambiguationData":[OSD([subQ0]),TDD([makeQuery(id+"F3.imprint","IMPRINT",EDGE,{"disambiguationData":[TD([[makeQuery(id+"F3.imprint","INTERSECT",VERTEX,{"derivedFrom":[sQuery(id+"F3.wireOp",EDGE,"E51.MirrorCS"),subQ0]}),1.0]])],"derivedFrom":subQ0})])]})]});}
            var Q9;
            Q9=makeQuery(id+"F4.boolean.opBoolean","INTERSECT",EDGE,{"disambiguationData":[OD(0.0)],"derivedFrom":[makeQuery(id+"F1.opExtrude","SWEPT_FACE",FACE,{"disambiguationData":[OSD([sQuery(id+"F0.wireOp",EDGE,"E1")])]}),makeQuery(id+"F4.opExtrude","SWEPT_FACE",FACE,{"disambiguationData":[OSD([sQuery(id+"F3.wireOp",EDGE,"E51.MirrorCS")])]})]});
            var Q10;
            Q10=makeQuery(id+"F4.boolean.opBoolean","INTERSECT",EDGE,{"disambiguationData":[OD(0.0)],"derivedFrom":[makeQuery(id+"F1.opExtrude","SWEPT_FACE",FACE,{"disambiguationData":[OSD([sQuery(id+"F0.wireOp",EDGE,"E1")])]}),makeQuery(id+"F4.opExtrude","SWEPT_FACE",FACE,{"disambiguationData":[OSD([sQuery(id+"F3.wireOp",EDGE,"E49.MirrorCS")])]})]});
            var Q11;
            Q11=makeQuery(id+"F4.boolean.opBoolean","INTERSECT",EDGE,{"disambiguationData":[OD(0.0)],"derivedFrom":[makeQuery(id+"F1.opExtrude","SWEPT_FACE",FACE,{"disambiguationData":[OSD([sQuery(id+"F0.wireOp",EDGE,"E1")])]}),makeQuery(id+"F4.opExtrude","SWEPT_FACE",FACE,{"disambiguationData":[OSD([sQuery(id+"F3.wireOp",EDGE,"E58.0")])]})]});
            var Q12;
            Q12=makeQuery(id+"F4.boolean.opBoolean","INTERSECT",EDGE,{"disambiguationData":[OD(0.0)],"derivedFrom":[makeQuery(id+"F1.opExtrude","SWEPT_FACE",FACE,{"disambiguationData":[OSD([sQuery(id+"F0.wireOp",EDGE,"E1")])]}),makeQuery(id+"F4.opExtrude","SWEPT_FACE",FACE,{"disambiguationData":[OSD([sQuery(id+"F3.wireOp",EDGE,"E48.MirrorCS")])]})]});
            var Q13;
            {var subQ0=sQuery(id+"F3.wireOp",EDGE,"E57.0");Q13=makeQuery(id+"F4.boolean.opBoolean","INTERSECT",EDGE,{"disambiguationData":[OD(0.0)],"derivedFrom":[makeQuery(id+"F1.opExtrude","SWEPT_FACE",FACE,{"disambiguationData":[OSD([sQuery(id+"F0.wireOp",EDGE,"E1")])]}),makeQuery(id+"F4.opExtrude","SWEPT_FACE",FACE,{"disambiguationData":[OSD([subQ0]),TDD([makeQuery(id+"F3.imprint","IMPRINT",EDGE,{"disambiguationData":[TD([[makeQuery(id+"F3.imprint","INTERSECT",VERTEX,{"derivedFrom":[sQuery(id+"F3.wireOp",EDGE,"E48.MirrorCS"),subQ0]}),1.0]])],"derivedFrom":subQ0})])]})]});}
            var Q14;
            Q14=makeQuery(id+"F4.boolean.opBoolean","INTERSECT",EDGE,{"disambiguationData":[OD(0.0)],"derivedFrom":[makeQuery(id+"F1.opExtrude","SWEPT_FACE",FACE,{"disambiguationData":[OSD([sQuery(id+"F0.wireOp",EDGE,"E1")])]}),makeQuery(id+"F4.opExtrude","SWEPT_FACE",FACE,{"disambiguationData":[OSD([sQuery(id+"F3.wireOp",EDGE,"E46.MirrorCS")])]})]});
            var Q15;
            Q15=makeQuery(id+"F4.boolean.opBoolean","INTERSECT",EDGE,{"disambiguationData":[OD(0.0)],"derivedFrom":[makeQuery(id+"F1.opExtrude","SWEPT_FACE",FACE,{"disambiguationData":[OSD([sQuery(id+"F0.wireOp",EDGE,"E1")])]}),makeQuery(id+"F4.opExtrude","SWEPT_FACE",FACE,{"disambiguationData":[OSD([sQuery(id+"F3.wireOp",EDGE,"E47.MirrorCS")])]})]});
            var Q16;
            Q16=makeQuery(id+"F4.boolean.opBoolean","INTERSECT",EDGE,{"disambiguationData":[OD(0.0)],"derivedFrom":[makeQuery(id+"F1.opExtrude","SWEPT_FACE",FACE,{"disambiguationData":[OSD([sQuery(id+"F0.wireOp",EDGE,"E1")])]}),makeQuery(id+"F4.opExtrude","SWEPT_FACE",FACE,{"disambiguationData":[OSD([sQuery(id+"F3.wireOp",EDGE,"E62.2")])]})]});
            var Q17;
            Q17=makeQuery(id+"F4.boolean.opBoolean","INTERSECT",EDGE,{"disambiguationData":[OD(0.0)],"derivedFrom":[makeQuery(id+"F1.opExtrude","SWEPT_FACE",FACE,{"disambiguationData":[OSD([sQuery(id+"F0.wireOp",EDGE,"E1")])]}),makeQuery(id+"F4.opExtrude","SWEPT_FACE",FACE,{"disambiguationData":[OSD([sQuery(id+"F3.wireOp",EDGE,"E62.1")])]})]});
            var Q18;
            Q18=makeQuery(id+"F4.boolean.opBoolean","INTERSECT",EDGE,{"disambiguationData":[OD(0.0)],"derivedFrom":[makeQuery(id+"F1.opExtrude","SWEPT_FACE",FACE,{"disambiguationData":[OSD([sQuery(id+"F0.wireOp",EDGE,"E1")])]}),makeQuery(id+"F4.opExtrude","SWEPT_FACE",FACE,{"disambiguationData":[OSD([sQuery(id+"F3.wireOp",EDGE,"E62.0")])]})]});
            var Q19;
            Q19=makeQuery(id+"F4.boolean.opBoolean","INTERSECT",EDGE,{"disambiguationData":[OD(0.0)],"derivedFrom":[makeQuery(id+"F1.opExtrude","SWEPT_FACE",FACE,{"disambiguationData":[OSD([sQuery(id+"F0.wireOp",EDGE,"E1")])]}),makeQuery(id+"F4.opExtrude","SWEPT_FACE",FACE,{"disambiguationData":[OSD([sQuery(id+"F3.wireOp",EDGE,"E61.0")])]})]});
            var Q20;
            Q20=makeQuery(id+"F4.boolean.opBoolean","INTERSECT",EDGE,{"disambiguationData":[OD(0.0)],"derivedFrom":[makeQuery(id+"F1.opExtrude","SWEPT_FACE",FACE,{"disambiguationData":[OSD([sQuery(id+"F0.wireOp",EDGE,"E1")])]}),makeQuery(id+"F4.opExtrude","SWEPT_FACE",FACE,{"disambiguationData":[OSD([sQuery(id+"F3.wireOp",EDGE,"E61.1")])]})]});
            var Q21;
            Q21=makeQuery(id+"F4.boolean.opBoolean","INTERSECT",EDGE,{"disambiguationData":[OD(0.0)],"derivedFrom":[makeQuery(id+"F1.opExtrude","SWEPT_FACE",FACE,{"disambiguationData":[OSD([sQuery(id+"F0.wireOp",EDGE,"E1")])]}),makeQuery(id+"F4.opExtrude","SWEPT_FACE",FACE,{"disambiguationData":[OSD([sQuery(id+"F3.wireOp",EDGE,"E60.0")])]})]});
            var Q22;
            Q22=makeQuery(id+"F4.boolean.opBoolean","INTERSECT",EDGE,{"disambiguationData":[OD(0.0)],"derivedFrom":[makeQuery(id+"F1.opExtrude","SWEPT_FACE",FACE,{"disambiguationData":[OSD([sQuery(id+"F0.wireOp",EDGE,"E1")])]}),makeQuery(id+"F4.opExtrude","SWEPT_FACE",FACE,{"disambiguationData":[OSD([sQuery(id+"F3.wireOp",EDGE,"E60.1")])]})]});
            var Q23;
            Q23=makeQuery(id+"F4.boolean.opBoolean","INTERSECT",EDGE,{"disambiguationData":[OD(0.0)],"derivedFrom":[makeQuery(id+"F1.opExtrude","SWEPT_FACE",FACE,{"disambiguationData":[OSD([sQuery(id+"F0.wireOp",EDGE,"E1")])]}),makeQuery(id+"F4.opExtrude","SWEPT_FACE",FACE,{"disambiguationData":[OSD([sQuery(id+"F3.wireOp",EDGE,"E60.2")])]})]});
            var Q24;
            Q24=makeQuery(id+"F4.boolean.opBoolean","INTERSECT",EDGE,{"disambiguationData":[OD(0.0)],"derivedFrom":[makeQuery(id+"F1.opExtrude","SWEPT_FACE",FACE,{"disambiguationData":[OSD([sQuery(id+"F0.wireOp",EDGE,"E1")])]}),makeQuery(id+"F4.opExtrude","SWEPT_FACE",FACE,{"disambiguationData":[OSD([sQuery(id+"F3.wireOp",EDGE,"E61.2")])]})]});
            var Q25;
            Q25=makeQuery(id+"F4.boolean.opBoolean","INTERSECT",EDGE,{"disambiguationData":[OD(0.0)],"derivedFrom":[makeQuery(id+"F1.opExtrude","SWEPT_FACE",FACE,{"disambiguationData":[OSD([sQuery(id+"F0.wireOp",EDGE,"E1")])]}),makeQuery(id+"F4.opExtrude","SWEPT_FACE",FACE,{"disambiguationData":[OSD([sQuery(id+"F3.wireOp",EDGE,"E65.0")])]})]});
            var Q26;
            Q26=makeQuery(id+"F4.boolean.opBoolean","INTERSECT",EDGE,{"disambiguationData":[OD(0.0)],"derivedFrom":[makeQuery(id+"F1.opExtrude","SWEPT_FACE",FACE,{"disambiguationData":[OSD([sQuery(id+"F0.wireOp",EDGE,"E1")])]}),makeQuery(id+"F4.opExtrude","SWEPT_FACE",FACE,{"disambiguationData":[OSD([sQuery(id+"F3.wireOp",EDGE,"E65.1")])]})]});
            var Q27;
            Q27=makeQuery(id+"F4.boolean.opBoolean","INTERSECT",EDGE,{"disambiguationData":[OD(0.0)],"derivedFrom":[makeQuery(id+"F1.opExtrude","SWEPT_FACE",FACE,{"disambiguationData":[OSD([sQuery(id+"F0.wireOp",EDGE,"E1")])]}),makeQuery(id+"F4.opExtrude","SWEPT_FACE",FACE,{"disambiguationData":[OSD([sQuery(id+"F3.wireOp",EDGE,"E63")])]})]});
            var Q28;
            Q28=makeQuery(id+"F4.boolean.opBoolean","INTERSECT",EDGE,{"disambiguationData":[OD(0.0)],"derivedFrom":[makeQuery(id+"F1.opExtrude","SWEPT_FACE",FACE,{"disambiguationData":[OSD([sQuery(id+"F0.wireOp",EDGE,"E1")])]}),makeQuery(id+"F4.opExtrude","SWEPT_FACE",FACE,{"disambiguationData":[OSD([sQuery(id+"F3.wireOp",EDGE,"E21"),sQuery(id+"F3.wireOp",EDGE,"E68")])]})]});
            var Q29;
            {var subQ0=sQuery(id+"F3.wireOp",EDGE,"E65.2");Q29=makeQuery(id+"F4.boolean.opBoolean","INTERSECT",EDGE,{"disambiguationData":[OD(0.0)],"derivedFrom":[makeQuery(id+"F1.opExtrude","SWEPT_FACE",FACE,{"disambiguationData":[OSD([sQuery(id+"F0.wireOp",EDGE,"E1")])]}),makeQuery(id+"F4.opExtrude","SWEPT_FACE",FACE,{"disambiguationData":[OSD([subQ0]),TDD([makeQuery(id+"F3.imprint","IMPRINT",EDGE,{"disambiguationData":[TD([[makeQuery(id+"F3.imprint","INTERSECT",VERTEX,{"derivedFrom":[sQuery(id+"F3.wireOp",EDGE,"E65.1"),subQ0]}),-1.0]])],"derivedFrom":subQ0})])]})]});}
            var Q30;
            Q30=makeQuery(id+"F4.boolean.opBoolean","INTERSECT",EDGE,{"disambiguationData":[OD(0.0)],"derivedFrom":[makeQuery(id+"F1.opExtrude","SWEPT_FACE",FACE,{"disambiguationData":[OSD([sQuery(id+"F0.wireOp",EDGE,"E1")])]}),makeQuery(id+"F4.opExtrude","SWEPT_FACE",FACE,{"disambiguationData":[OSD([sQuery(id+"F3.wireOp",EDGE,"E65.3")])]})]});
            var Q31;
            Q31=makeQuery(id+"F4.boolean.opBoolean","INTERSECT",EDGE,{"disambiguationData":[OD(0.0)],"derivedFrom":[makeQuery(id+"F1.opExtrude","SWEPT_FACE",FACE,{"disambiguationData":[OSD([sQuery(id+"F0.wireOp",EDGE,"E1")])]}),makeQuery(id+"F4.opExtrude","SWEPT_FACE",FACE,{"disambiguationData":[OSD([sQuery(id+"F3.wireOp",EDGE,"E65.4")])]})]});
            var Q32;
            Q32=makeQuery(id+"F4.boolean.opBoolean","INTERSECT",EDGE,{"disambiguationData":[OD(0.0)],"derivedFrom":[makeQuery(id+"F1.opExtrude","SWEPT_FACE",FACE,{"disambiguationData":[OSD([sQuery(id+"F0.wireOp",EDGE,"E1")])]}),makeQuery(id+"F4.opExtrude","SWEPT_FACE",FACE,{"disambiguationData":[OSD([sQuery(id+"F3.wireOp",EDGE,"E64")])]})]});
            var Q33;
            Q33=makeQuery(id+"F4.boolean.opBoolean","INTERSECT",EDGE,{"disambiguationData":[OD(0.0)],"derivedFrom":[makeQuery(id+"F1.opExtrude","SWEPT_FACE",FACE,{"disambiguationData":[OSD([sQuery(id+"F0.wireOp",EDGE,"E1")])]}),makeQuery(id+"F4.opExtrude","SWEPT_FACE",FACE,{"disambiguationData":[OSD([sQuery(id+"F3.wireOp",EDGE,"E23"),sQuery(id+"F3.wireOp",EDGE,"E69")])]})]});
            var Q34;
            {var subQ0=sQuery(id+"F3.wireOp",EDGE,"E65.5");Q34=makeQuery(id+"F4.boolean.opBoolean","INTERSECT",EDGE,{"disambiguationData":[OD(0.0)],"derivedFrom":[makeQuery(id+"F1.opExtrude","SWEPT_FACE",FACE,{"disambiguationData":[OSD([sQuery(id+"F0.wireOp",EDGE,"E1")])]}),makeQuery(id+"F4.opExtrude","SWEPT_FACE",FACE,{"disambiguationData":[OSD([subQ0]),TDD([makeQuery(id+"F3.imprint","IMPRINT",EDGE,{"disambiguationData":[TD([[makeQuery(id+"F3.imprint","INTERSECT",VERTEX,{"derivedFrom":[sQuery(id+"F3.wireOp",EDGE,"E65.4"),subQ0]}),1.0]])],"derivedFrom":subQ0})])]})]});}
            var Q35;
            {var subQ0=sQuery(id+"F3.wireOp",EDGE,"E65.5");Q35=makeQuery(id+"F4.boolean.opBoolean","INTERSECT",EDGE,{"disambiguationData":[OD(0.0)],"derivedFrom":[makeQuery(id+"F1.opExtrude","SWEPT_FACE",FACE,{"disambiguationData":[OSD([sQuery(id+"F0.wireOp",EDGE,"E1")])]}),makeQuery(id+"F4.opExtrude","SWEPT_FACE",FACE,{"disambiguationData":[OSD([subQ0]),TDD([makeQuery(id+"F3.imprint","IMPRINT",EDGE,{"disambiguationData":[TD([[makeQuery(id+"F3.imprint","INTERSECT",VERTEX,{"derivedFrom":[subQ0,sQuery(id+"F3.wireOp",EDGE,"E65.6")]}),-1.0]])],"derivedFrom":subQ0})])]})]});}
            var Q36;
            Q36=makeQuery(id+"F4.boolean.opBoolean","INTERSECT",EDGE,{"disambiguationData":[OD(0.0)],"derivedFrom":[makeQuery(id+"F1.opExtrude","SWEPT_FACE",FACE,{"disambiguationData":[OSD([sQuery(id+"F0.wireOp",EDGE,"E1")])]}),makeQuery(id+"F4.opExtrude","SWEPT_FACE",FACE,{"disambiguationData":[OSD([sQuery(id+"F3.wireOp",EDGE,"E27.right")])]})]});
            var Q37;
            Q37=makeQuery(id+"F4.boolean.opBoolean","INTERSECT",EDGE,{"disambiguationData":[OD(0.0)],"derivedFrom":[makeQuery(id+"F1.opExtrude","SWEPT_FACE",FACE,{"disambiguationData":[OSD([sQuery(id+"F0.wireOp",EDGE,"E1")])]}),makeQuery(id+"F4.opExtrude","SWEPT_FACE",FACE,{"disambiguationData":[OSD([sQuery(id+"F3.wireOp",EDGE,"E27.top")])]})]});
            var Q38;
            Q38=makeQuery(id+"F4.boolean.opBoolean","INTERSECT",EDGE,{"disambiguationData":[OD(0.0)],"derivedFrom":[makeQuery(id+"F1.opExtrude","SWEPT_FACE",FACE,{"disambiguationData":[OSD([sQuery(id+"F0.wireOp",EDGE,"E1")])]}),makeQuery(id+"F4.opExtrude","SWEPT_FACE",FACE,{"disambiguationData":[OSD([sQuery(id+"F3.wireOp",EDGE,"E27.bottom")])]})]});
            var Q39;
            Q39=makeQuery(id+"F4.boolean.opBoolean","INTERSECT",EDGE,{"disambiguationData":[OD(0.0)],"derivedFrom":[makeQuery(id+"F1.opExtrude","SWEPT_FACE",FACE,{"disambiguationData":[OSD([sQuery(id+"F0.wireOp",EDGE,"E1")])]}),makeQuery(id+"F4.opExtrude","SWEPT_FACE",FACE,{"disambiguationData":[OSD([sQuery(id+"F3.wireOp",EDGE,"E26.right")])]})]});
            var Q40;
            Q40=makeQuery(id+"F4.boolean.opBoolean","INTERSECT",EDGE,{"disambiguationData":[OD(0.0)],"derivedFrom":[makeQuery(id+"F1.opExtrude","SWEPT_FACE",FACE,{"disambiguationData":[OSD([sQuery(id+"F0.wireOp",EDGE,"E1")])]}),makeQuery(id+"F4.opExtrude","SWEPT_FACE",FACE,{"disambiguationData":[OSD([sQuery(id+"F3.wireOp",EDGE,"E26.top")])]})]});
            var Q41;
            Q41=makeQuery(id+"F4.boolean.opBoolean","INTERSECT",EDGE,{"disambiguationData":[OD(0.0)],"derivedFrom":[makeQuery(id+"F1.opExtrude","SWEPT_FACE",FACE,{"disambiguationData":[OSD([sQuery(id+"F0.wireOp",EDGE,"E1")])]}),makeQuery(id+"F4.opExtrude","SWEPT_FACE",FACE,{"disambiguationData":[OSD([sQuery(id+"F3.wireOp",EDGE,"E28")])]})]});
            var Q42;
            Q42=makeQuery(id+"F4.boolean.opBoolean","INTERSECT",EDGE,{"disambiguationData":[OD(0.0)],"derivedFrom":[makeQuery(id+"F1.opExtrude","SWEPT_FACE",FACE,{"disambiguationData":[OSD([sQuery(id+"F0.wireOp",EDGE,"E1")])]}),makeQuery(id+"F4.opExtrude","SWEPT_FACE",FACE,{"disambiguationData":[OSD([sQuery(id+"F3.wireOp",EDGE,"E29")])]})]});
            var Q43;
            Q43=makeQuery(id+"F4.boolean.opBoolean","INTERSECT",EDGE,{"disambiguationData":[OD(0.0)],"derivedFrom":[makeQuery(id+"F1.opExtrude","SWEPT_FACE",FACE,{"disambiguationData":[OSD([sQuery(id+"F0.wireOp",EDGE,"E1")])]}),makeQuery(id+"F4.opExtrude","SWEPT_FACE",FACE,{"disambiguationData":[OSD([sQuery(id+"F3.wireOp",EDGE,"E25.bottom")])]})]});
            var Q44;
            Q44=makeQuery(id+"F4.boolean.opBoolean","INTERSECT",EDGE,{"disambiguationData":[OD(0.0)],"derivedFrom":[makeQuery(id+"F1.opExtrude","SWEPT_FACE",FACE,{"disambiguationData":[OSD([sQuery(id+"F0.wireOp",EDGE,"E1")])]}),makeQuery(id+"F4.opExtrude","SWEPT_FACE",FACE,{"disambiguationData":[OSD([sQuery(id+"F3.wireOp",EDGE,"E24.top")])]})]});
            var Q45;
            Q45=makeQuery(id+"F4.boolean.opBoolean","INTERSECT",EDGE,{"disambiguationData":[OD(0.0)],"derivedFrom":[makeQuery(id+"F1.opExtrude","SWEPT_FACE",FACE,{"disambiguationData":[OSD([sQuery(id+"F0.wireOp",EDGE,"E1")])]}),makeQuery(id+"F4.opExtrude","SWEPT_FACE",FACE,{"disambiguationData":[OSD([sQuery(id+"F3.wireOp",EDGE,"E25.right")])]})]});
            var Q46;
            Q46=makeQuery(id+"F4.boolean.opBoolean","INTERSECT",EDGE,{"disambiguationData":[OD(0.0)],"derivedFrom":[makeQuery(id+"F1.opExtrude","SWEPT_FACE",FACE,{"disambiguationData":[OSD([sQuery(id+"F0.wireOp",EDGE,"E1")])]}),makeQuery(id+"F4.opExtrude","SWEPT_FACE",FACE,{"disambiguationData":[OSD([sQuery(id+"F3.wireOp",EDGE,"E25.left")])]})]});
            var Q47;
            Q47=makeQuery(id+"F4.boolean.opBoolean","INTERSECT",EDGE,{"disambiguationData":[OD(0.0)],"derivedFrom":[makeQuery(id+"F1.opExtrude","SWEPT_FACE",FACE,{"disambiguationData":[OSD([sQuery(id+"F0.wireOp",EDGE,"E1")])]}),makeQuery(id+"F4.opExtrude","SWEPT_FACE",FACE,{"disambiguationData":[OSD([sQuery(id+"F3.wireOp",EDGE,"E24.right")])]})]});
            var Q48;
            Q48=makeQuery(id+"F4.boolean.opBoolean","INTERSECT",EDGE,{"disambiguationData":[OD(0.0)],"derivedFrom":[makeQuery(id+"F1.opExtrude","SWEPT_FACE",FACE,{"disambiguationData":[OSD([sQuery(id+"F0.wireOp",EDGE,"E1")])]}),makeQuery(id+"F4.opExtrude","SWEPT_FACE",FACE,{"disambiguationData":[OSD([sQuery(id+"F3.wireOp",EDGE,"E24.left")])]})]});
            var Q49;
            Q49=makeQuery(id+"F4.boolean.opBoolean","INTERSECT",EDGE,{"disambiguationData":[OD(0.0)],"derivedFrom":[makeQuery(id+"F1.opExtrude","SWEPT_FACE",FACE,{"disambiguationData":[OSD([sQuery(id+"F0.wireOp",EDGE,"E1")])]}),makeQuery(id+"F4.opExtrude","SWEPT_FACE",FACE,{"disambiguationData":[OSD([sQuery(id+"F3.wireOp",EDGE,"E27.left")])]})]});
            var Q50;
            Q50=makeQuery(id+"F4.boolean.opBoolean","INTERSECT",EDGE,{"disambiguationData":[OD(0.0)],"derivedFrom":[makeQuery(id+"F1.opExtrude","SWEPT_FACE",FACE,{"disambiguationData":[OSD([sQuery(id+"F0.wireOp",EDGE,"E1")])]}),makeQuery(id+"F4.opExtrude","SWEPT_FACE",FACE,{"disambiguationData":[OSD([sQuery(id+"F3.wireOp",EDGE,"E25.top")])]})]});
            var Q51;
            Q51=makeQuery(id+"F4.boolean.opBoolean","INTERSECT",EDGE,{"disambiguationData":[OD(0.0)],"derivedFrom":[makeQuery(id+"F1.opExtrude","SWEPT_FACE",FACE,{"disambiguationData":[OSD([sQuery(id+"F0.wireOp",EDGE,"E1")])]}),makeQuery(id+"F4.opExtrude","SWEPT_FACE",FACE,{"disambiguationData":[OSD([sQuery(id+"F3.wireOp",EDGE,"E24.bottom")])]})]});
            var Q52;
            {var subQ0=sQuery(id+"F3.wireOp",EDGE,"E30");Q52=makeQuery(id+"F4.boolean.opBoolean","INTERSECT",EDGE,{"disambiguationData":[OD(0.0)],"derivedFrom":[makeQuery(id+"F1.opExtrude","SWEPT_FACE",FACE,{"disambiguationData":[OSD([sQuery(id+"F0.wireOp",EDGE,"E1")])]}),makeQuery(id+"F4.opExtrude","SWEPT_FACE",FACE,{"disambiguationData":[OSD([subQ0]),TDD([makeQuery(id+"F3.imprint","IMPRINT",EDGE,{"disambiguationData":[TD([[makeQuery(id+"F3.imprint","INTERSECT",VERTEX,{"derivedFrom":[subQ0,sQuery(id+"F3.wireOp",EDGE,"E44")]}),1.0]])],"derivedFrom":subQ0})])]})]});}
            var Q53;
            {var subQ0=sQuery(id+"F3.wireOp",EDGE,"E65.2");Q53=makeQuery(id+"F4.boolean.opBoolean","INTERSECT",EDGE,{"disambiguationData":[OD(0.0)],"derivedFrom":[makeQuery(id+"F1.opExtrude","SWEPT_FACE",FACE,{"disambiguationData":[OSD([sQuery(id+"F0.wireOp",EDGE,"E1")])]}),makeQuery(id+"F4.opExtrude","SWEPT_FACE",FACE,{"disambiguationData":[OSD([subQ0]),TDD([makeQuery(id+"F3.imprint","IMPRINT",EDGE,{"disambiguationData":[TD([[makeQuery(id+"F3.imprint","INTERSECT",VERTEX,{"derivedFrom":[subQ0,sQuery(id+"F3.wireOp",EDGE,"E65.6")]}),1.0]])],"derivedFrom":subQ0})])]})]});}
            var Q54;
            {var subQ0=sQuery(id+"F3.wireOp",EDGE,"E31.0");Q54=makeQuery(id+"F4.boolean.opBoolean","INTERSECT",EDGE,{"disambiguationData":[OD(0.0)],"derivedFrom":[makeQuery(id+"F1.opExtrude","SWEPT_FACE",FACE,{"disambiguationData":[OSD([sQuery(id+"F0.wireOp",EDGE,"E1")])]}),makeQuery(id+"F4.opExtrude","SWEPT_FACE",FACE,{"disambiguationData":[OSD([subQ0]),TDD([makeQuery(id+"F3.imprint","IMPRINT",EDGE,{"disambiguationData":[TD([[makeQuery(id+"F3.imprint","INTERSECT",VERTEX,{"derivedFrom":[subQ0,sQuery(id+"F3.wireOp",EDGE,"E39")]}),1.0]])],"derivedFrom":subQ0})])]})]});}
            var Q55;
            Q55=makeQuery(id+"F4.boolean.opBoolean","INTERSECT",EDGE,{"disambiguationData":[OD(0.0)],"derivedFrom":[makeQuery(id+"F1.opExtrude","SWEPT_FACE",FACE,{"disambiguationData":[OSD([sQuery(id+"F0.wireOp",EDGE,"E1")])]}),makeQuery(id+"F4.opExtrude","SWEPT_FACE",FACE,{"disambiguationData":[OSD([sQuery(id+"F3.wireOp",EDGE,"E35")])]})]});
            var Q56;
            Q56=makeQuery(id+"F4.boolean.opBoolean","INTERSECT",EDGE,{"disambiguationData":[OD(0.0)],"derivedFrom":[makeQuery(id+"F1.opExtrude","SWEPT_FACE",FACE,{"disambiguationData":[OSD([sQuery(id+"F0.wireOp",EDGE,"E1")])]}),makeQuery(id+"F4.opExtrude","SWEPT_FACE",FACE,{"disambiguationData":[OSD([sQuery(id+"F3.wireOp",EDGE,"E37")])]})]});
            var Q57;
            Q57=makeQuery(id+"F4.boolean.opBoolean","INTERSECT",EDGE,{"disambiguationData":[OD(0.0)],"derivedFrom":[makeQuery(id+"F1.opExtrude","SWEPT_FACE",FACE,{"disambiguationData":[OSD([sQuery(id+"F0.wireOp",EDGE,"E1")])]}),makeQuery(id+"F4.opExtrude","SWEPT_FACE",FACE,{"disambiguationData":[OSD([sQuery(id+"F3.wireOp",EDGE,"E38")])]})]});
            var Q58;
            Q58=makeQuery(id+"F4.boolean.opBoolean","INTERSECT",EDGE,{"disambiguationData":[OD(0.0)],"derivedFrom":[makeQuery(id+"F1.opExtrude","SWEPT_FACE",FACE,{"disambiguationData":[OSD([sQuery(id+"F0.wireOp",EDGE,"E1")])]}),makeQuery(id+"F4.opExtrude","SWEPT_FACE",FACE,{"disambiguationData":[OSD([sQuery(id+"F3.wireOp",EDGE,"E39")])]})]});
            var Q59;
            Q59=makeQuery(id+"F4.boolean.opBoolean","INTERSECT",EDGE,{"disambiguationData":[OD(0.0)],"derivedFrom":[makeQuery(id+"F1.opExtrude","SWEPT_FACE",FACE,{"disambiguationData":[OSD([sQuery(id+"F0.wireOp",EDGE,"E1")])]}),makeQuery(id+"F4.opExtrude","SWEPT_FACE",FACE,{"disambiguationData":[OSD([sQuery(id+"F3.wireOp",EDGE,"E36.0")])]})]});
            var Q60;
            {var subQ0=sQuery(id+"F3.wireOp",EDGE,"E31.0");Q60=makeQuery(id+"F4.boolean.opBoolean","INTERSECT",EDGE,{"disambiguationData":[OD(0.0)],"derivedFrom":[makeQuery(id+"F1.opExtrude","SWEPT_FACE",FACE,{"disambiguationData":[OSD([sQuery(id+"F0.wireOp",EDGE,"E1")])]}),makeQuery(id+"F4.opExtrude","SWEPT_FACE",FACE,{"disambiguationData":[OSD([subQ0]),TDD([makeQuery(id+"F3.imprint","IMPRINT",EDGE,{"disambiguationData":[TD([[makeQuery(id+"F3.imprint","INTERSECT",VERTEX,{"derivedFrom":[subQ0,sQuery(id+"F3.wireOp",EDGE,"E34")]}),1.0]])],"derivedFrom":subQ0})])]})]});}
            var Q61;
            Q61=makeQuery(id+"F4.boolean.opBoolean","INTERSECT",EDGE,{"disambiguationData":[OD(0.0)],"derivedFrom":[makeQuery(id+"F1.opExtrude","SWEPT_FACE",FACE,{"disambiguationData":[OSD([sQuery(id+"F0.wireOp",EDGE,"E1")])]}),makeQuery(id+"F4.opExtrude","SWEPT_FACE",FACE,{"disambiguationData":[OSD([sQuery(id+"F3.wireOp",EDGE,"E44")])]})]});
            var Q62;
            Q62=makeQuery(id+"F4.boolean.opBoolean","INTERSECT",EDGE,{"disambiguationData":[OD(0.0)],"derivedFrom":[makeQuery(id+"F1.opExtrude","SWEPT_FACE",FACE,{"disambiguationData":[OSD([sQuery(id+"F0.wireOp",EDGE,"E1")])]}),makeQuery(id+"F4.opExtrude","SWEPT_FACE",FACE,{"disambiguationData":[OSD([sQuery(id+"F3.wireOp",EDGE,"E41.0")])]})]});
            var Q63;
            Q63=makeQuery(id+"F4.boolean.opBoolean","INTERSECT",EDGE,{"disambiguationData":[OD(0.0)],"derivedFrom":[makeQuery(id+"F1.opExtrude","SWEPT_FACE",FACE,{"disambiguationData":[OSD([sQuery(id+"F0.wireOp",EDGE,"E1")])]}),makeQuery(id+"F4.opExtrude","SWEPT_FACE",FACE,{"disambiguationData":[OSD([sQuery(id+"F3.wireOp",EDGE,"E40")])]})]});
            var Q64;
            Q64=makeQuery(id+"F4.boolean.opBoolean","INTERSECT",EDGE,{"disambiguationData":[OD(0.0)],"derivedFrom":[makeQuery(id+"F1.opExtrude","SWEPT_FACE",FACE,{"disambiguationData":[OSD([sQuery(id+"F0.wireOp",EDGE,"E1")])]}),makeQuery(id+"F4.opExtrude","SWEPT_FACE",FACE,{"disambiguationData":[OSD([sQuery(id+"F3.wireOp",EDGE,"E43")])]})]});
            var Q65;
            Q65=makeQuery(id+"F4.boolean.opBoolean","INTERSECT",EDGE,{"disambiguationData":[OD(0.0)],"derivedFrom":[makeQuery(id+"F1.opExtrude","SWEPT_FACE",FACE,{"disambiguationData":[OSD([sQuery(id+"F0.wireOp",EDGE,"E1")])]}),makeQuery(id+"F4.opExtrude","SWEPT_FACE",FACE,{"disambiguationData":[OSD([sQuery(id+"F3.wireOp",EDGE,"E42")])]})]});
            var Q66;
            {var subQ0=sQuery(id+"F3.wireOp",EDGE,"E30");Q66=makeQuery(id+"F4.boolean.opBoolean","INTERSECT",EDGE,{"disambiguationData":[OD(0.0)],"derivedFrom":[makeQuery(id+"F1.opExtrude","SWEPT_FACE",FACE,{"disambiguationData":[OSD([sQuery(id+"F0.wireOp",EDGE,"E1")])]}),makeQuery(id+"F4.opExtrude","SWEPT_FACE",FACE,{"disambiguationData":[OSD([subQ0]),TDD([makeQuery(id+"F3.imprint","IMPRINT",EDGE,{"disambiguationData":[TD([[makeQuery(id+"F3.imprint","INTERSECT",VERTEX,{"derivedFrom":[subQ0,sQuery(id+"F3.wireOp",EDGE,"E33")]}),1.0]])],"derivedFrom":subQ0})])]})]});}
            var Q67;
            Q67=makeQuery(id+"F4.boolean.opBoolean","INTERSECT",EDGE,{"disambiguationData":[OD(0.0)],"derivedFrom":[makeQuery(id+"F1.opExtrude","SWEPT_FACE",FACE,{"disambiguationData":[OSD([sQuery(id+"F0.wireOp",EDGE,"E1")])]}),makeQuery(id+"F4.opExtrude","SWEPT_FACE",FACE,{"disambiguationData":[OSD([sQuery(id+"F3.wireOp",EDGE,"E34")])]})]});
            var Q68;
            Q68=makeQuery(id+"F4.boolean.opBoolean","INTERSECT",EDGE,{"disambiguationData":[OD(0.0)],"derivedFrom":[makeQuery(id+"F1.opExtrude","SWEPT_FACE",FACE,{"disambiguationData":[OSD([sQuery(id+"F0.wireOp",EDGE,"E1")])]}),makeQuery(id+"F4.opExtrude","SWEPT_FACE",FACE,{"disambiguationData":[OSD([sQuery(id+"F3.wireOp",EDGE,"E33")])]})]});
            fillet(context, id + "F11", {"entities" : qUnion([Q0, Q1, Q2, Q3, Q4, Q5, Q6, Q7, Q8, Q9, Q10, Q11, Q12, Q13, Q14, Q15, Q16, Q17, Q18, Q19, Q20, Q21, Q22, Q23, Q24, Q25, Q26, Q27, Q28, Q29, Q30, Q31, Q32, Q33, Q34, Q35, Q36, Q37, Q38, Q39, Q40, Q41, Q42, Q43, Q44, Q45, Q46, Q47, Q48, Q49, Q50, Q51, Q52, Q53, Q54, Q55, Q56, Q57, Q58, Q59, Q60, Q61, Q62, Q63, Q64, Q65, Q66, Q67, Q68]), "radius" : .1 * mm, "tangentPropagation" : true, "allowEdgeOverflow" : false});
        }
        {
            var Q0;
            {var subQ1=sQuery(id+"F3.wireOp",EDGE,"E51.MirrorCS");Q0=makeQuery(id+"F3.imprint","IMPRINT",FACE,{"disambiguationData":[TD([[makeQuery(id+"F3.imprint","IMPRINT",EDGE,{"derivedFrom":subQ1}),1.0]])]});}
            var Q1;
            {var subQ0=sQuery(id+"F3.wireOp",EDGE,"E40");Q1=makeQuery(id+"F3.imprint","IMPRINT",FACE,{"disambiguationData":[TD([[makeQuery(id+"F3.imprint","IMPRINT",EDGE,{"derivedFrom":subQ0}),-1.0]])]});}
            extrude(context, id + "F12", {"entities" : qUnion([Q0, Q1]), "operationType" : NewBodyOperationType.ADD, "depth" : 40 * mm, "offsetDistance" : 25 * mm, "hasSecondDirection" : true, "secondDirectionOppositeDirection" : true, "secondDirectionDepth" : 40 * mm});
        }
        {
            var Q0;
            {var subQ0=sQuery(id+"F5.wireOp",EDGE,"E100");Q0=makeQuery(id+"F5.imprint","IMPRINT",FACE,{"disambiguationData":[TD([[makeQuery(id+"F5.imprint","IMPRINT",EDGE,{"derivedFrom":subQ0}),-1.0]])]});}
            var Q1;
            {var subQ1=sQuery(id+"F5.wireOp",EDGE,"E111.MirrorCS");Q1=makeQuery(id+"F5.imprint","IMPRINT",FACE,{"disambiguationData":[TD([[makeQuery(id+"F5.imprint","IMPRINT",EDGE,{"derivedFrom":subQ1}),1.0]])]});}
            extrude(context, id + "F13", {"entities" : qUnion([Q0, Q1]), "operationType" : NewBodyOperationType.ADD, "depth" : 40 * mm, "offsetDistance" : 25 * mm, "hasSecondDirection" : true, "secondDirectionOppositeDirection" : true, "secondDirectionDepth" : 40 * mm});
        }
        {
            var Q0;
            Q0=makeQuery(id+"F2.opExtrude","CAP_FACE",FACE,{"disambiguationData":[OSD([sQuery(id+"F0.wireOp",EDGE,"E0"),sQuery(id+"F0.wireOp",EDGE,"E2")])],"isStart":false});
            var Q1;
            Q1=makeQuery(id+"F0.imprint","IMPRINT",FACE,{"disambiguationData":[TD([[makeQuery(id+"F0.imprint","IMPRINT",EDGE,{"derivedFrom":sQuery(id+"F0.wireOp",EDGE,"E2")}),1.0]])]});
            extrude(context, id + "F14", {"entities" : qUnion([Q0, Q1]), "operationType" : NewBodyOperationType.REMOVE, "depth" : 64 * mm, "offsetDistance" : 25 * mm});
        }
        {
            var Q0;
            Q0=makeQuery(id+"F2.opExtrude","CAP_EDGE",EDGE,{"disambiguationData":[OSD([sQuery(id+"F0.wireOp",EDGE,"E2")])],"isStart":false});
            fillet(context, id + "F15", {"entities" : qUnion([Q0]), "radius" : 1 * mm, "tangentPropagation" : true, "allowEdgeOverflow" : false});
        }
        {
            var Q0;
            Q0=makeQuery(id+"F6.boolean.opBoolean","INTERSECT",EDGE,{"disambiguationData":[OD(0.0)],"derivedFrom":[makeQuery(id+"F1.opExtrude","SWEPT_FACE",FACE,{"disambiguationData":[OSD([sQuery(id+"F0.wireOp",EDGE,"E1")])]}),makeQuery(id+"F6.opExtrude","SWEPT_FACE",FACE,{"disambiguationData":[OSD([sQuery(id+"F5.wireOp",EDGE,"E115.MirrorCS")])]})]});
            var Q1;
            Q1=makeQuery(id+"F6.boolean.opBoolean","INTERSECT",EDGE,{"disambiguationData":[OD(0.0)],"derivedFrom":[makeQuery(id+"F1.opExtrude","SWEPT_FACE",FACE,{"disambiguationData":[OSD([sQuery(id+"F0.wireOp",EDGE,"E1")])]}),makeQuery(id+"F6.opExtrude","SWEPT_FACE",FACE,{"disambiguationData":[OSD([sQuery(id+"F5.wireOp",EDGE,"E119.0")])]})]});
            var Q2;
            Q2=makeQuery(id+"F6.boolean.opBoolean","INTERSECT",EDGE,{"disambiguationData":[OD(0.0)],"derivedFrom":[makeQuery(id+"F1.opExtrude","SWEPT_FACE",FACE,{"disambiguationData":[OSD([sQuery(id+"F0.wireOp",EDGE,"E1")])]}),makeQuery(id+"F6.opExtrude","SWEPT_FACE",FACE,{"disambiguationData":[OSD([sQuery(id+"F5.wireOp",EDGE,"E114.MirrorCS")])]})]});
            var Q3;
            Q3=makeQuery(id+"F6.boolean.opBoolean","INTERSECT",EDGE,{"disambiguationData":[OD(0.0)],"derivedFrom":[makeQuery(id+"F1.opExtrude","SWEPT_FACE",FACE,{"disambiguationData":[OSD([sQuery(id+"F0.wireOp",EDGE,"E1")])]}),makeQuery(id+"F6.opExtrude","SWEPT_FACE",FACE,{"disambiguationData":[OSD([sQuery(id+"F5.wireOp",EDGE,"E113.MirrorCS")])]})]});
            var Q4;
            Q4=makeQuery(id+"F6.boolean.opBoolean","INTERSECT",EDGE,{"disambiguationData":[OD(0.0)],"derivedFrom":[makeQuery(id+"F1.opExtrude","SWEPT_FACE",FACE,{"disambiguationData":[OSD([sQuery(id+"F0.wireOp",EDGE,"E1")])]}),makeQuery(id+"F6.opExtrude","SWEPT_FACE",FACE,{"disambiguationData":[OSD([sQuery(id+"F5.wireOp",EDGE,"E111.MirrorCS")])]})]});
            var Q5;
            {var subQ0=sQuery(id+"F5.wireOp",EDGE,"E117.0");Q5=makeQuery(id+"F6.boolean.opBoolean","INTERSECT",EDGE,{"disambiguationData":[OD(0.0)],"derivedFrom":[makeQuery(id+"F1.opExtrude","SWEPT_FACE",FACE,{"disambiguationData":[OSD([sQuery(id+"F0.wireOp",EDGE,"E1")])]}),makeQuery(id+"F6.opExtrude","SWEPT_FACE",FACE,{"disambiguationData":[OSD([subQ0]),TDD([makeQuery(id+"F5.imprint","IMPRINT",EDGE,{"disambiguationData":[TD([[makeQuery(id+"F5.imprint","INTERSECT",VERTEX,{"derivedFrom":[sQuery(id+"F5.wireOp",EDGE,"E109.MirrorCS"),subQ0]}),-1.0]])],"derivedFrom":subQ0})])]})]});}
            var Q6;
            {var subQ0=sQuery(id+"F5.wireOp",EDGE,"E116.MirrorCS");Q6=makeQuery(id+"F6.boolean.opBoolean","INTERSECT",EDGE,{"disambiguationData":[OD(0.0)],"derivedFrom":[makeQuery(id+"F1.opExtrude","SWEPT_FACE",FACE,{"disambiguationData":[OSD([sQuery(id+"F0.wireOp",EDGE,"E1")])]}),makeQuery(id+"F6.opExtrude","SWEPT_FACE",FACE,{"disambiguationData":[OSD([subQ0]),TDD([makeQuery(id+"F5.imprint","IMPRINT",EDGE,{"disambiguationData":[TD([[makeQuery(id+"F5.imprint","INTERSECT",VERTEX,{"derivedFrom":[sQuery(id+"F5.wireOp",EDGE,"E110.MirrorCS"),subQ0]}),1.0]])],"derivedFrom":subQ0})])]})]});}
            var Q7;
            Q7=makeQuery(id+"F6.boolean.opBoolean","INTERSECT",EDGE,{"disambiguationData":[OD(0.0)],"derivedFrom":[makeQuery(id+"F1.opExtrude","SWEPT_FACE",FACE,{"disambiguationData":[OSD([sQuery(id+"F0.wireOp",EDGE,"E1")])]}),makeQuery(id+"F6.opExtrude","SWEPT_FACE",FACE,{"disambiguationData":[OSD([sQuery(id+"F5.wireOp",EDGE,"E112.MirrorCS")])]})]});
            var Q8;
            Q8=makeQuery(id+"F6.boolean.opBoolean","INTERSECT",EDGE,{"disambiguationData":[OD(0.0)],"derivedFrom":[makeQuery(id+"F1.opExtrude","SWEPT_FACE",FACE,{"disambiguationData":[OSD([sQuery(id+"F0.wireOp",EDGE,"E1")])]}),makeQuery(id+"F6.opExtrude","SWEPT_FACE",FACE,{"disambiguationData":[OSD([sQuery(id+"F5.wireOp",EDGE,"E110.MirrorCS")])]})]});
            var Q9;
            {var subQ0=sQuery(id+"F5.wireOp",EDGE,"E116.MirrorCS");Q9=makeQuery(id+"F6.boolean.opBoolean","INTERSECT",EDGE,{"disambiguationData":[OD(0.0)],"derivedFrom":[makeQuery(id+"F1.opExtrude","SWEPT_FACE",FACE,{"disambiguationData":[OSD([sQuery(id+"F0.wireOp",EDGE,"E1")])]}),makeQuery(id+"F6.opExtrude","SWEPT_FACE",FACE,{"disambiguationData":[OSD([subQ0]),TDD([makeQuery(id+"F5.imprint","IMPRINT",EDGE,{"disambiguationData":[TD([[makeQuery(id+"F5.imprint","INTERSECT",VERTEX,{"derivedFrom":[sQuery(id+"F5.wireOp",EDGE,"E111.MirrorCS"),subQ0]}),1.0]])],"derivedFrom":subQ0})])]})]});}
            var Q10;
            Q10=makeQuery(id+"F6.boolean.opBoolean","INTERSECT",EDGE,{"disambiguationData":[OD(0.0)],"derivedFrom":[makeQuery(id+"F1.opExtrude","SWEPT_FACE",FACE,{"disambiguationData":[OSD([sQuery(id+"F0.wireOp",EDGE,"E1")])]}),makeQuery(id+"F6.opExtrude","SWEPT_FACE",FACE,{"disambiguationData":[OSD([sQuery(id+"F5.wireOp",EDGE,"E109.MirrorCS")])]})]});
            var Q11;
            Q11=makeQuery(id+"F6.boolean.opBoolean","INTERSECT",EDGE,{"disambiguationData":[OD(0.0)],"derivedFrom":[makeQuery(id+"F1.opExtrude","SWEPT_FACE",FACE,{"disambiguationData":[OSD([sQuery(id+"F0.wireOp",EDGE,"E1")])]}),makeQuery(id+"F6.opExtrude","SWEPT_FACE",FACE,{"disambiguationData":[OSD([sQuery(id+"F5.wireOp",EDGE,"E118.0")])]})]});
            var Q12;
            Q12=makeQuery(id+"F6.boolean.opBoolean","INTERSECT",EDGE,{"disambiguationData":[OD(0.0)],"derivedFrom":[makeQuery(id+"F1.opExtrude","SWEPT_FACE",FACE,{"disambiguationData":[OSD([sQuery(id+"F0.wireOp",EDGE,"E1")])]}),makeQuery(id+"F6.opExtrude","SWEPT_FACE",FACE,{"disambiguationData":[OSD([sQuery(id+"F5.wireOp",EDGE,"E108.MirrorCS")])]})]});
            var Q13;
            {var subQ0=sQuery(id+"F5.wireOp",EDGE,"E117.0");Q13=makeQuery(id+"F6.boolean.opBoolean","INTERSECT",EDGE,{"disambiguationData":[OD(0.0)],"derivedFrom":[makeQuery(id+"F1.opExtrude","SWEPT_FACE",FACE,{"disambiguationData":[OSD([sQuery(id+"F0.wireOp",EDGE,"E1")])]}),makeQuery(id+"F6.opExtrude","SWEPT_FACE",FACE,{"disambiguationData":[OSD([subQ0]),TDD([makeQuery(id+"F5.imprint","IMPRINT",EDGE,{"disambiguationData":[TD([[makeQuery(id+"F5.imprint","INTERSECT",VERTEX,{"derivedFrom":[sQuery(id+"F5.wireOp",EDGE,"E108.MirrorCS"),subQ0]}),1.0]])],"derivedFrom":subQ0})])]})]});}
            var Q14;
            Q14=makeQuery(id+"F6.boolean.opBoolean","INTERSECT",EDGE,{"disambiguationData":[OD(0.0)],"derivedFrom":[makeQuery(id+"F1.opExtrude","SWEPT_FACE",FACE,{"disambiguationData":[OSD([sQuery(id+"F0.wireOp",EDGE,"E1")])]}),makeQuery(id+"F6.opExtrude","SWEPT_FACE",FACE,{"disambiguationData":[OSD([sQuery(id+"F5.wireOp",EDGE,"E106.MirrorCS")])]})]});
            var Q15;
            Q15=makeQuery(id+"F6.boolean.opBoolean","INTERSECT",EDGE,{"disambiguationData":[OD(0.0)],"derivedFrom":[makeQuery(id+"F1.opExtrude","SWEPT_FACE",FACE,{"disambiguationData":[OSD([sQuery(id+"F0.wireOp",EDGE,"E1")])]}),makeQuery(id+"F6.opExtrude","SWEPT_FACE",FACE,{"disambiguationData":[OSD([sQuery(id+"F5.wireOp",EDGE,"E107.MirrorCS")])]})]});
            var Q16;
            Q16=makeQuery(id+"F6.boolean.opBoolean","INTERSECT",EDGE,{"disambiguationData":[OD(0.0)],"derivedFrom":[makeQuery(id+"F1.opExtrude","SWEPT_FACE",FACE,{"disambiguationData":[OSD([sQuery(id+"F0.wireOp",EDGE,"E1")])]}),makeQuery(id+"F6.opExtrude","SWEPT_FACE",FACE,{"disambiguationData":[OSD([sQuery(id+"F5.wireOp",EDGE,"E100")])]})]});
            var Q17;
            Q17=makeQuery(id+"F6.boolean.opBoolean","INTERSECT",EDGE,{"disambiguationData":[OD(0.0)],"derivedFrom":[makeQuery(id+"F1.opExtrude","SWEPT_FACE",FACE,{"disambiguationData":[OSD([sQuery(id+"F0.wireOp",EDGE,"E1")])]}),makeQuery(id+"F6.opExtrude","SWEPT_FACE",FACE,{"disambiguationData":[OSD([sQuery(id+"F5.wireOp",EDGE,"E101.0")])]})]});
            var Q18;
            Q18=makeQuery(id+"F6.boolean.opBoolean","INTERSECT",EDGE,{"disambiguationData":[OD(0.0)],"derivedFrom":[makeQuery(id+"F1.opExtrude","SWEPT_FACE",FACE,{"disambiguationData":[OSD([sQuery(id+"F0.wireOp",EDGE,"E1")])]}),makeQuery(id+"F6.opExtrude","SWEPT_FACE",FACE,{"disambiguationData":[OSD([sQuery(id+"F5.wireOp",EDGE,"E103")])]})]});
            var Q19;
            Q19=makeQuery(id+"F6.boolean.opBoolean","INTERSECT",EDGE,{"disambiguationData":[OD(0.0)],"derivedFrom":[makeQuery(id+"F1.opExtrude","SWEPT_FACE",FACE,{"disambiguationData":[OSD([sQuery(id+"F0.wireOp",EDGE,"E1")])]}),makeQuery(id+"F6.opExtrude","SWEPT_FACE",FACE,{"disambiguationData":[OSD([sQuery(id+"F5.wireOp",EDGE,"E102")])]})]});
            var Q20;
            {var subQ0=sQuery(id+"F5.wireOp",EDGE,"E90");Q20=makeQuery(id+"F6.boolean.opBoolean","INTERSECT",EDGE,{"disambiguationData":[OD(0.0)],"derivedFrom":[makeQuery(id+"F1.opExtrude","SWEPT_FACE",FACE,{"disambiguationData":[OSD([sQuery(id+"F0.wireOp",EDGE,"E1")])]}),makeQuery(id+"F6.opExtrude","SWEPT_FACE",FACE,{"disambiguationData":[OSD([subQ0]),TDD([makeQuery(id+"F5.imprint","IMPRINT",EDGE,{"disambiguationData":[TD([[makeQuery(id+"F5.imprint","INTERSECT",VERTEX,{"derivedFrom":[subQ0,sQuery(id+"F5.wireOp",EDGE,"E93")]}),1.0]])],"derivedFrom":subQ0})])]})]});}
            var Q21;
            {var subQ0=sQuery(id+"F5.wireOp",EDGE,"E91.0");Q21=makeQuery(id+"F6.boolean.opBoolean","INTERSECT",EDGE,{"disambiguationData":[OD(0.0)],"derivedFrom":[makeQuery(id+"F1.opExtrude","SWEPT_FACE",FACE,{"disambiguationData":[OSD([sQuery(id+"F0.wireOp",EDGE,"E1")])]}),makeQuery(id+"F6.opExtrude","SWEPT_FACE",FACE,{"disambiguationData":[OSD([subQ0]),TDD([makeQuery(id+"F5.imprint","IMPRINT",EDGE,{"disambiguationData":[TD([[makeQuery(id+"F5.imprint","INTERSECT",VERTEX,{"derivedFrom":[subQ0,sQuery(id+"F5.wireOp",EDGE,"E94")]}),1.0]])],"derivedFrom":subQ0})])]})]});}
            var Q22;
            Q22=makeQuery(id+"F6.boolean.opBoolean","INTERSECT",EDGE,{"disambiguationData":[OD(0.0)],"derivedFrom":[makeQuery(id+"F1.opExtrude","SWEPT_FACE",FACE,{"disambiguationData":[OSD([sQuery(id+"F0.wireOp",EDGE,"E1")])]}),makeQuery(id+"F6.opExtrude","SWEPT_FACE",FACE,{"disambiguationData":[OSD([sQuery(id+"F5.wireOp",EDGE,"E93")])]})]});
            var Q23;
            Q23=makeQuery(id+"F6.boolean.opBoolean","INTERSECT",EDGE,{"disambiguationData":[OD(0.0)],"derivedFrom":[makeQuery(id+"F1.opExtrude","SWEPT_FACE",FACE,{"disambiguationData":[OSD([sQuery(id+"F0.wireOp",EDGE,"E1")])]}),makeQuery(id+"F6.opExtrude","SWEPT_FACE",FACE,{"disambiguationData":[OSD([sQuery(id+"F5.wireOp",EDGE,"E94")])]})]});
            var Q24;
            Q24=makeQuery(id+"F6.boolean.opBoolean","INTERSECT",EDGE,{"disambiguationData":[OD(0.0)],"derivedFrom":[makeQuery(id+"F1.opExtrude","SWEPT_FACE",FACE,{"disambiguationData":[OSD([sQuery(id+"F0.wireOp",EDGE,"E1")])]}),makeQuery(id+"F6.opExtrude","SWEPT_FACE",FACE,{"disambiguationData":[OSD([sQuery(id+"F5.wireOp",EDGE,"E104")])]})]});
            var Q25;
            {var subQ0=sQuery(id+"F5.wireOp",EDGE,"E90");Q25=makeQuery(id+"F6.boolean.opBoolean","INTERSECT",EDGE,{"disambiguationData":[OD(0.0)],"derivedFrom":[makeQuery(id+"F1.opExtrude","SWEPT_FACE",FACE,{"disambiguationData":[OSD([sQuery(id+"F0.wireOp",EDGE,"E1")])]}),makeQuery(id+"F6.opExtrude","SWEPT_FACE",FACE,{"disambiguationData":[OSD([subQ0]),TDD([makeQuery(id+"F5.imprint","IMPRINT",EDGE,{"disambiguationData":[TD([[makeQuery(id+"F5.imprint","INTERSECT",VERTEX,{"derivedFrom":[subQ0,sQuery(id+"F5.wireOp",EDGE,"E104")]}),1.0]])],"derivedFrom":subQ0})])]})]});}
            var Q26;
            Q26=makeQuery(id+"F6.boolean.opBoolean","INTERSECT",EDGE,{"disambiguationData":[OD(0.0)],"derivedFrom":[makeQuery(id+"F1.opExtrude","SWEPT_FACE",FACE,{"disambiguationData":[OSD([sQuery(id+"F0.wireOp",EDGE,"E1")])]}),makeQuery(id+"F6.opExtrude","SWEPT_FACE",FACE,{"disambiguationData":[OSD([sQuery(id+"F5.wireOp",EDGE,"E95")])]})]});
            var Q27;
            Q27=makeQuery(id+"F6.boolean.opBoolean","INTERSECT",EDGE,{"disambiguationData":[OD(0.0)],"derivedFrom":[makeQuery(id+"F1.opExtrude","SWEPT_FACE",FACE,{"disambiguationData":[OSD([sQuery(id+"F0.wireOp",EDGE,"E1")])]}),makeQuery(id+"F6.opExtrude","SWEPT_FACE",FACE,{"disambiguationData":[OSD([sQuery(id+"F5.wireOp",EDGE,"E96.0")])]})]});
            var Q28;
            Q28=makeQuery(id+"F6.boolean.opBoolean","INTERSECT",EDGE,{"disambiguationData":[OD(0.0)],"derivedFrom":[makeQuery(id+"F1.opExtrude","SWEPT_FACE",FACE,{"disambiguationData":[OSD([sQuery(id+"F0.wireOp",EDGE,"E1")])]}),makeQuery(id+"F6.opExtrude","SWEPT_FACE",FACE,{"disambiguationData":[OSD([sQuery(id+"F5.wireOp",EDGE,"E98")])]})]});
            var Q29;
            Q29=makeQuery(id+"F6.boolean.opBoolean","INTERSECT",EDGE,{"disambiguationData":[OD(0.0)],"derivedFrom":[makeQuery(id+"F1.opExtrude","SWEPT_FACE",FACE,{"disambiguationData":[OSD([sQuery(id+"F0.wireOp",EDGE,"E1")])]}),makeQuery(id+"F6.opExtrude","SWEPT_FACE",FACE,{"disambiguationData":[OSD([sQuery(id+"F5.wireOp",EDGE,"E97")])]})]});
            var Q30;
            Q30=makeQuery(id+"F6.boolean.opBoolean","INTERSECT",EDGE,{"disambiguationData":[OD(0.0)],"derivedFrom":[makeQuery(id+"F1.opExtrude","SWEPT_FACE",FACE,{"disambiguationData":[OSD([sQuery(id+"F0.wireOp",EDGE,"E1")])]}),makeQuery(id+"F6.opExtrude","SWEPT_FACE",FACE,{"disambiguationData":[OSD([sQuery(id+"F5.wireOp",EDGE,"E99")])]})]});
            var Q31;
            {var subQ0=sQuery(id+"F5.wireOp",EDGE,"E91.0");Q31=makeQuery(id+"F6.boolean.opBoolean","INTERSECT",EDGE,{"disambiguationData":[OD(0.0)],"derivedFrom":[makeQuery(id+"F1.opExtrude","SWEPT_FACE",FACE,{"disambiguationData":[OSD([sQuery(id+"F0.wireOp",EDGE,"E1")])]}),makeQuery(id+"F6.opExtrude","SWEPT_FACE",FACE,{"disambiguationData":[OSD([subQ0]),TDD([makeQuery(id+"F5.imprint","IMPRINT",EDGE,{"disambiguationData":[TD([[makeQuery(id+"F5.imprint","INTERSECT",VERTEX,{"derivedFrom":[subQ0,sQuery(id+"F5.wireOp",EDGE,"E99")]}),1.0]])],"derivedFrom":subQ0})])]})]});}
            var Q32;
            {var subQ0=sQuery(id+"F5.wireOp",EDGE,"E125.2");Q32=makeQuery(id+"F6.boolean.opBoolean","INTERSECT",EDGE,{"disambiguationData":[OD(0.0)],"derivedFrom":[makeQuery(id+"F1.opExtrude","SWEPT_FACE",FACE,{"disambiguationData":[OSD([sQuery(id+"F0.wireOp",EDGE,"E1")])]}),makeQuery(id+"F6.opExtrude","SWEPT_FACE",FACE,{"disambiguationData":[OSD([subQ0]),TDD([makeQuery(id+"F5.imprint","IMPRINT",EDGE,{"disambiguationData":[TD([[makeQuery(id+"F5.imprint","INTERSECT",VERTEX,{"derivedFrom":[sQuery(id+"F5.wireOp",EDGE,"E125.1"),subQ0]}),-1.0]])],"derivedFrom":subQ0})])]})]});}
            var Q33;
            Q33=makeQuery(id+"F6.boolean.opBoolean","INTERSECT",EDGE,{"disambiguationData":[OD(0.0)],"derivedFrom":[makeQuery(id+"F1.opExtrude","SWEPT_FACE",FACE,{"disambiguationData":[OSD([sQuery(id+"F0.wireOp",EDGE,"E1")])]}),makeQuery(id+"F6.opExtrude","SWEPT_FACE",FACE,{"disambiguationData":[OSD([sQuery(id+"F5.wireOp",EDGE,"E81"),sQuery(id+"F5.wireOp",EDGE,"E128")])]})]});
            var Q34;
            {var subQ0=sQuery(id+"F5.wireOp",EDGE,"E125.2");Q34=makeQuery(id+"F6.boolean.opBoolean","INTERSECT",EDGE,{"disambiguationData":[OD(0.0)],"derivedFrom":[makeQuery(id+"F1.opExtrude","SWEPT_FACE",FACE,{"disambiguationData":[OSD([sQuery(id+"F0.wireOp",EDGE,"E1")])]}),makeQuery(id+"F6.opExtrude","SWEPT_FACE",FACE,{"disambiguationData":[OSD([subQ0]),TDD([makeQuery(id+"F5.imprint","IMPRINT",EDGE,{"disambiguationData":[TD([[makeQuery(id+"F5.imprint","INTERSECT",VERTEX,{"derivedFrom":[subQ0,sQuery(id+"F5.wireOp",EDGE,"E125.6")]}),1.0]])],"derivedFrom":subQ0})])]})]});}
            var Q35;
            Q35=makeQuery(id+"F6.boolean.opBoolean","INTERSECT",EDGE,{"disambiguationData":[OD(0.0)],"derivedFrom":[makeQuery(id+"F1.opExtrude","SWEPT_FACE",FACE,{"disambiguationData":[OSD([sQuery(id+"F0.wireOp",EDGE,"E1")])]}),makeQuery(id+"F6.opExtrude","SWEPT_FACE",FACE,{"disambiguationData":[OSD([sQuery(id+"F5.wireOp",EDGE,"E123")])]})]});
            var Q36;
            Q36=makeQuery(id+"F6.boolean.opBoolean","INTERSECT",EDGE,{"disambiguationData":[OD(0.0)],"derivedFrom":[makeQuery(id+"F1.opExtrude","SWEPT_FACE",FACE,{"disambiguationData":[OSD([sQuery(id+"F0.wireOp",EDGE,"E1")])]}),makeQuery(id+"F6.opExtrude","SWEPT_FACE",FACE,{"disambiguationData":[OSD([sQuery(id+"F5.wireOp",EDGE,"E125.1")])]})]});
            var Q37;
            Q37=makeQuery(id+"F6.boolean.opBoolean","INTERSECT",EDGE,{"disambiguationData":[OD(0.0)],"derivedFrom":[makeQuery(id+"F1.opExtrude","SWEPT_FACE",FACE,{"disambiguationData":[OSD([sQuery(id+"F0.wireOp",EDGE,"E1")])]}),makeQuery(id+"F6.opExtrude","SWEPT_FACE",FACE,{"disambiguationData":[OSD([sQuery(id+"F5.wireOp",EDGE,"E125.0")])]})]});
            var Q38;
            Q38=makeQuery(id+"F6.boolean.opBoolean","INTERSECT",EDGE,{"disambiguationData":[OD(1.0)],"derivedFrom":[makeQuery(id+"F1.opExtrude","SWEPT_FACE",FACE,{"disambiguationData":[OSD([sQuery(id+"F0.wireOp",EDGE,"E1")])]}),makeQuery(id+"F6.opExtrude","SWEPT_FACE",FACE,{"disambiguationData":[OSD([sQuery(id+"F5.wireOp",EDGE,"E120.2")])]})]});
            var Q39;
            Q39=makeQuery(id+"F6.boolean.opBoolean","INTERSECT",EDGE,{"disambiguationData":[OD(1.0)],"derivedFrom":[makeQuery(id+"F1.opExtrude","SWEPT_FACE",FACE,{"disambiguationData":[OSD([sQuery(id+"F0.wireOp",EDGE,"E1")])]}),makeQuery(id+"F6.opExtrude","SWEPT_FACE",FACE,{"disambiguationData":[OSD([sQuery(id+"F5.wireOp",EDGE,"E120.1")])]})]});
            var Q40;
            Q40=makeQuery(id+"F6.boolean.opBoolean","INTERSECT",EDGE,{"disambiguationData":[OD(1.0)],"derivedFrom":[makeQuery(id+"F1.opExtrude","SWEPT_FACE",FACE,{"disambiguationData":[OSD([sQuery(id+"F0.wireOp",EDGE,"E1")])]}),makeQuery(id+"F6.opExtrude","SWEPT_FACE",FACE,{"disambiguationData":[OSD([sQuery(id+"F5.wireOp",EDGE,"E120.0")])]})]});
            var Q41;
            Q41=makeQuery(id+"F6.boolean.opBoolean","INTERSECT",EDGE,{"disambiguationData":[OD(1.0)],"derivedFrom":[makeQuery(id+"F1.opExtrude","SWEPT_FACE",FACE,{"disambiguationData":[OSD([sQuery(id+"F0.wireOp",EDGE,"E1")])]}),makeQuery(id+"F6.opExtrude","SWEPT_FACE",FACE,{"disambiguationData":[OSD([sQuery(id+"F5.wireOp",EDGE,"E122.0")])]})]});
            var Q42;
            Q42=makeQuery(id+"F6.boolean.opBoolean","INTERSECT",EDGE,{"disambiguationData":[OD(1.0)],"derivedFrom":[makeQuery(id+"F1.opExtrude","SWEPT_FACE",FACE,{"disambiguationData":[OSD([sQuery(id+"F0.wireOp",EDGE,"E1")])]}),makeQuery(id+"F6.opExtrude","SWEPT_FACE",FACE,{"disambiguationData":[OSD([sQuery(id+"F5.wireOp",EDGE,"E122.1")])]})]});
            var Q43;
            Q43=makeQuery(id+"F6.boolean.opBoolean","INTERSECT",EDGE,{"disambiguationData":[OD(1.0)],"derivedFrom":[makeQuery(id+"F1.opExtrude","SWEPT_FACE",FACE,{"disambiguationData":[OSD([sQuery(id+"F0.wireOp",EDGE,"E1")])]}),makeQuery(id+"F6.opExtrude","SWEPT_FACE",FACE,{"disambiguationData":[OSD([sQuery(id+"F5.wireOp",EDGE,"E122.2")])]})]});
            var Q44;
            Q44=makeQuery(id+"F6.boolean.opBoolean","INTERSECT",EDGE,{"disambiguationData":[OD(1.0)],"derivedFrom":[makeQuery(id+"F1.opExtrude","SWEPT_FACE",FACE,{"disambiguationData":[OSD([sQuery(id+"F0.wireOp",EDGE,"E1")])]}),makeQuery(id+"F6.opExtrude","SWEPT_FACE",FACE,{"disambiguationData":[OSD([sQuery(id+"F5.wireOp",EDGE,"E121.0")])]})]});
            var Q45;
            Q45=makeQuery(id+"F6.boolean.opBoolean","INTERSECT",EDGE,{"disambiguationData":[OD(1.0)],"derivedFrom":[makeQuery(id+"F1.opExtrude","SWEPT_FACE",FACE,{"disambiguationData":[OSD([sQuery(id+"F0.wireOp",EDGE,"E1")])]}),makeQuery(id+"F6.opExtrude","SWEPT_FACE",FACE,{"disambiguationData":[OSD([sQuery(id+"F5.wireOp",EDGE,"E121.1")])]})]});
            var Q46;
            Q46=makeQuery(id+"F6.boolean.opBoolean","INTERSECT",EDGE,{"disambiguationData":[OD(1.0)],"derivedFrom":[makeQuery(id+"F1.opExtrude","SWEPT_FACE",FACE,{"disambiguationData":[OSD([sQuery(id+"F0.wireOp",EDGE,"E1")])]}),makeQuery(id+"F6.opExtrude","SWEPT_FACE",FACE,{"disambiguationData":[OSD([sQuery(id+"F5.wireOp",EDGE,"E121.2")])]})]});
            var Q47;
            Q47=makeQuery(id+"F6.boolean.opBoolean","INTERSECT",EDGE,{"disambiguationData":[OD(0.0)],"derivedFrom":[makeQuery(id+"F1.opExtrude","SWEPT_FACE",FACE,{"disambiguationData":[OSD([sQuery(id+"F0.wireOp",EDGE,"E1")])]}),makeQuery(id+"F6.opExtrude","SWEPT_FACE",FACE,{"disambiguationData":[OSD([sQuery(id+"F5.wireOp",EDGE,"E125.3")])]})]});
            var Q48;
            Q48=makeQuery(id+"F6.boolean.opBoolean","INTERSECT",EDGE,{"disambiguationData":[OD(0.0)],"derivedFrom":[makeQuery(id+"F1.opExtrude","SWEPT_FACE",FACE,{"disambiguationData":[OSD([sQuery(id+"F0.wireOp",EDGE,"E1")])]}),makeQuery(id+"F6.opExtrude","SWEPT_FACE",FACE,{"disambiguationData":[OSD([sQuery(id+"F5.wireOp",EDGE,"E124")])]})]});
            var Q49;
            Q49=makeQuery(id+"F6.boolean.opBoolean","INTERSECT",EDGE,{"disambiguationData":[OD(0.0)],"derivedFrom":[makeQuery(id+"F1.opExtrude","SWEPT_FACE",FACE,{"disambiguationData":[OSD([sQuery(id+"F0.wireOp",EDGE,"E1")])]}),makeQuery(id+"F6.opExtrude","SWEPT_FACE",FACE,{"disambiguationData":[OSD([sQuery(id+"F5.wireOp",EDGE,"E125.4")])]})]});
            var Q50;
            {var subQ0=sQuery(id+"F5.wireOp",EDGE,"E125.5");Q50=makeQuery(id+"F6.boolean.opBoolean","INTERSECT",EDGE,{"disambiguationData":[OD(0.0)],"derivedFrom":[makeQuery(id+"F1.opExtrude","SWEPT_FACE",FACE,{"disambiguationData":[OSD([sQuery(id+"F0.wireOp",EDGE,"E1")])]}),makeQuery(id+"F6.opExtrude","SWEPT_FACE",FACE,{"disambiguationData":[OSD([subQ0]),TDD([makeQuery(id+"F5.imprint","IMPRINT",EDGE,{"disambiguationData":[TD([[makeQuery(id+"F5.imprint","INTERSECT",VERTEX,{"derivedFrom":[sQuery(id+"F5.wireOp",EDGE,"E125.4"),subQ0]}),1.0]])],"derivedFrom":subQ0})])]})]});}
            var Q51;
            Q51=makeQuery(id+"F6.boolean.opBoolean","INTERSECT",EDGE,{"disambiguationData":[OD(0.0)],"derivedFrom":[makeQuery(id+"F1.opExtrude","SWEPT_FACE",FACE,{"disambiguationData":[OSD([sQuery(id+"F0.wireOp",EDGE,"E1")])]}),makeQuery(id+"F6.opExtrude","SWEPT_FACE",FACE,{"disambiguationData":[OSD([sQuery(id+"F5.wireOp",EDGE,"E83"),sQuery(id+"F5.wireOp",EDGE,"E129")])]})]});
            var Q52;
            Q52=makeQuery(id+"F6.boolean.opBoolean","INTERSECT",EDGE,{"disambiguationData":[OD(1.0)],"derivedFrom":[makeQuery(id+"F1.opExtrude","SWEPT_FACE",FACE,{"disambiguationData":[OSD([sQuery(id+"F0.wireOp",EDGE,"E1")])]}),makeQuery(id+"F6.opExtrude","SWEPT_FACE",FACE,{"disambiguationData":[OSD([sQuery(id+"F5.wireOp",EDGE,"E87.top")])]})]});
            var Q53;
            Q53=makeQuery(id+"F6.boolean.opBoolean","INTERSECT",EDGE,{"disambiguationData":[OD(1.0)],"derivedFrom":[makeQuery(id+"F1.opExtrude","SWEPT_FACE",FACE,{"disambiguationData":[OSD([sQuery(id+"F0.wireOp",EDGE,"E1")])]}),makeQuery(id+"F6.opExtrude","SWEPT_FACE",FACE,{"disambiguationData":[OSD([sQuery(id+"F5.wireOp",EDGE,"E87.right")])]})]});
            var Q54;
            Q54=makeQuery(id+"F6.boolean.opBoolean","INTERSECT",EDGE,{"disambiguationData":[OD(1.0)],"derivedFrom":[makeQuery(id+"F1.opExtrude","SWEPT_FACE",FACE,{"disambiguationData":[OSD([sQuery(id+"F0.wireOp",EDGE,"E1")])]}),makeQuery(id+"F6.opExtrude","SWEPT_FACE",FACE,{"disambiguationData":[OSD([sQuery(id+"F5.wireOp",EDGE,"E87.left")])]})]});
            var Q55;
            Q55=makeQuery(id+"F6.boolean.opBoolean","INTERSECT",EDGE,{"disambiguationData":[OD(1.0)],"derivedFrom":[makeQuery(id+"F1.opExtrude","SWEPT_FACE",FACE,{"disambiguationData":[OSD([sQuery(id+"F0.wireOp",EDGE,"E1")])]}),makeQuery(id+"F6.opExtrude","SWEPT_FACE",FACE,{"disambiguationData":[OSD([sQuery(id+"F5.wireOp",EDGE,"E86.right")])]})]});
            var Q56;
            Q56=makeQuery(id+"F6.boolean.opBoolean","INTERSECT",EDGE,{"disambiguationData":[OD(1.0)],"derivedFrom":[makeQuery(id+"F1.opExtrude","SWEPT_FACE",FACE,{"disambiguationData":[OSD([sQuery(id+"F0.wireOp",EDGE,"E1")])]}),makeQuery(id+"F6.opExtrude","SWEPT_FACE",FACE,{"disambiguationData":[OSD([sQuery(id+"F5.wireOp",EDGE,"E88")])]})]});
            var Q57;
            Q57=makeQuery(id+"F6.boolean.opBoolean","INTERSECT",EDGE,{"disambiguationData":[OD(1.0)],"derivedFrom":[makeQuery(id+"F1.opExtrude","SWEPT_FACE",FACE,{"disambiguationData":[OSD([sQuery(id+"F0.wireOp",EDGE,"E1")])]}),makeQuery(id+"F6.opExtrude","SWEPT_FACE",FACE,{"disambiguationData":[OSD([sQuery(id+"F5.wireOp",EDGE,"E86.top")])]})]});
            var Q58;
            Q58=makeQuery(id+"F6.boolean.opBoolean","INTERSECT",EDGE,{"disambiguationData":[OD(1.0)],"derivedFrom":[makeQuery(id+"F1.opExtrude","SWEPT_FACE",FACE,{"disambiguationData":[OSD([sQuery(id+"F0.wireOp",EDGE,"E1")])]}),makeQuery(id+"F6.opExtrude","SWEPT_FACE",FACE,{"disambiguationData":[OSD([sQuery(id+"F5.wireOp",EDGE,"E85.top")])]})]});
            var Q59;
            Q59=makeQuery(id+"F6.boolean.opBoolean","INTERSECT",EDGE,{"disambiguationData":[OD(1.0)],"derivedFrom":[makeQuery(id+"F1.opExtrude","SWEPT_FACE",FACE,{"disambiguationData":[OSD([sQuery(id+"F0.wireOp",EDGE,"E1")])]}),makeQuery(id+"F6.opExtrude","SWEPT_FACE",FACE,{"disambiguationData":[OSD([sQuery(id+"F5.wireOp",EDGE,"E85.left")])]})]});
            var Q60;
            Q60=makeQuery(id+"F6.boolean.opBoolean","INTERSECT",EDGE,{"disambiguationData":[OD(1.0)],"derivedFrom":[makeQuery(id+"F1.opExtrude","SWEPT_FACE",FACE,{"disambiguationData":[OSD([sQuery(id+"F0.wireOp",EDGE,"E1")])]}),makeQuery(id+"F6.opExtrude","SWEPT_FACE",FACE,{"disambiguationData":[OSD([sQuery(id+"F5.wireOp",EDGE,"E85.right")])]})]});
            var Q61;
            Q61=makeQuery(id+"F6.boolean.opBoolean","INTERSECT",EDGE,{"disambiguationData":[OD(1.0)],"derivedFrom":[makeQuery(id+"F1.opExtrude","SWEPT_FACE",FACE,{"disambiguationData":[OSD([sQuery(id+"F0.wireOp",EDGE,"E1")])]}),makeQuery(id+"F6.opExtrude","SWEPT_FACE",FACE,{"disambiguationData":[OSD([sQuery(id+"F5.wireOp",EDGE,"E84.bottom")])]})]});
            var Q62;
            Q62=makeQuery(id+"F6.boolean.opBoolean","INTERSECT",EDGE,{"disambiguationData":[OD(1.0)],"derivedFrom":[makeQuery(id+"F1.opExtrude","SWEPT_FACE",FACE,{"disambiguationData":[OSD([sQuery(id+"F0.wireOp",EDGE,"E1")])]}),makeQuery(id+"F6.opExtrude","SWEPT_FACE",FACE,{"disambiguationData":[OSD([sQuery(id+"F5.wireOp",EDGE,"E84.right")])]})]});
            var Q63;
            Q63=makeQuery(id+"F6.boolean.opBoolean","INTERSECT",EDGE,{"disambiguationData":[OD(1.0)],"derivedFrom":[makeQuery(id+"F1.opExtrude","SWEPT_FACE",FACE,{"disambiguationData":[OSD([sQuery(id+"F0.wireOp",EDGE,"E1")])]}),makeQuery(id+"F6.opExtrude","SWEPT_FACE",FACE,{"disambiguationData":[OSD([sQuery(id+"F5.wireOp",EDGE,"E84.left")])]})]});
            var Q64;
            {var subQ0=sQuery(id+"F5.wireOp",EDGE,"E125.5");Q64=makeQuery(id+"F6.boolean.opBoolean","INTERSECT",EDGE,{"disambiguationData":[OD(0.0)],"derivedFrom":[makeQuery(id+"F1.opExtrude","SWEPT_FACE",FACE,{"disambiguationData":[OSD([sQuery(id+"F0.wireOp",EDGE,"E1")])]}),makeQuery(id+"F6.opExtrude","SWEPT_FACE",FACE,{"disambiguationData":[OSD([subQ0]),TDD([makeQuery(id+"F5.imprint","IMPRINT",EDGE,{"disambiguationData":[TD([[makeQuery(id+"F5.imprint","INTERSECT",VERTEX,{"derivedFrom":[subQ0,sQuery(id+"F5.wireOp",EDGE,"E125.6")]}),-1.0]])],"derivedFrom":subQ0})])]})]});}
            var Q65;
            {var subQ0=sQuery(id+"F5.wireOp",EDGE,"E125.6");Q65=makeQuery(id+"F6.boolean.opBoolean","INTERSECT",EDGE,{"disambiguationData":[OD(0.0)],"derivedFrom":[makeQuery(id+"F1.opExtrude","SWEPT_FACE",FACE,{"disambiguationData":[OSD([sQuery(id+"F0.wireOp",EDGE,"E1")])]}),makeQuery(id+"F6.opExtrude","SWEPT_FACE",FACE,{"disambiguationData":[OSD([subQ0]),TDD([makeQuery(id+"F5.imprint","IMPRINT",EDGE,{"disambiguationData":[TD([[makeQuery(id+"F5.imprint","INTERSECT",VERTEX,{"derivedFrom":[sQuery(id+"F5.wireOp",EDGE,"E125.5"),subQ0]}),1.0]])],"derivedFrom":subQ0})])]})]});}
            var Q66;
            Q66=makeQuery(id+"F6.boolean.opBoolean","INTERSECT",EDGE,{"disambiguationData":[OD(1.0)],"derivedFrom":[makeQuery(id+"F1.opExtrude","SWEPT_FACE",FACE,{"disambiguationData":[OSD([sQuery(id+"F0.wireOp",EDGE,"E1")])]}),makeQuery(id+"F6.opExtrude","SWEPT_FACE",FACE,{"disambiguationData":[OSD([sQuery(id+"F5.wireOp",EDGE,"E87.bottom")])]})]});
            var Q67;
            Q67=makeQuery(id+"F6.boolean.opBoolean","INTERSECT",EDGE,{"disambiguationData":[OD(1.0)],"derivedFrom":[makeQuery(id+"F1.opExtrude","SWEPT_FACE",FACE,{"disambiguationData":[OSD([sQuery(id+"F0.wireOp",EDGE,"E1")])]}),makeQuery(id+"F6.opExtrude","SWEPT_FACE",FACE,{"disambiguationData":[OSD([sQuery(id+"F5.wireOp",EDGE,"E89")])]})]});
            var Q68;
            Q68=makeQuery(id+"F6.boolean.opBoolean","INTERSECT",EDGE,{"disambiguationData":[OD(1.0)],"derivedFrom":[makeQuery(id+"F1.opExtrude","SWEPT_FACE",FACE,{"disambiguationData":[OSD([sQuery(id+"F0.wireOp",EDGE,"E1")])]}),makeQuery(id+"F6.opExtrude","SWEPT_FACE",FACE,{"disambiguationData":[OSD([sQuery(id+"F5.wireOp",EDGE,"E85.bottom")])]})]});
            var Q69;
            Q69=makeQuery(id+"F6.boolean.opBoolean","INTERSECT",EDGE,{"disambiguationData":[OD(1.0)],"derivedFrom":[makeQuery(id+"F1.opExtrude","SWEPT_FACE",FACE,{"disambiguationData":[OSD([sQuery(id+"F0.wireOp",EDGE,"E1")])]}),makeQuery(id+"F6.opExtrude","SWEPT_FACE",FACE,{"disambiguationData":[OSD([sQuery(id+"F5.wireOp",EDGE,"E84.top")])]})]});
            var Q70;
            {var subQ0=sQuery(id+"F5.wireOp",EDGE,"E125.6");Q70=makeQuery(id+"F6.boolean.opBoolean","INTERSECT",EDGE,{"disambiguationData":[OD(0.0)],"derivedFrom":[makeQuery(id+"F1.opExtrude","SWEPT_FACE",FACE,{"disambiguationData":[OSD([sQuery(id+"F0.wireOp",EDGE,"E1")])]}),makeQuery(id+"F6.opExtrude","SWEPT_FACE",FACE,{"disambiguationData":[OSD([subQ0]),TDD([makeQuery(id+"F5.imprint","IMPRINT",EDGE,{"disambiguationData":[TD([[makeQuery(id+"F5.imprint","INTERSECT",VERTEX,{"derivedFrom":[sQuery(id+"F5.wireOp",EDGE,"E125.2"),subQ0]}),-1.0]])],"derivedFrom":subQ0})])]})]});}
            fillet(context, id + "F16", {"entities" : qUnion([Q0, Q1, Q2, Q3, Q4, Q5, Q6, Q7, Q8, Q9, Q10, Q11, Q12, Q13, Q14, Q15, Q16, Q17, Q18, Q19, Q20, Q21, Q22, Q23, Q24, Q25, Q26, Q27, Q28, Q29, Q30, Q31, Q32, Q33, Q34, Q35, Q36, Q37, Q38, Q39, Q40, Q41, Q42, Q43, Q44, Q45, Q46, Q47, Q48, Q49, Q50, Q51, Q52, Q53, Q54, Q55, Q56, Q57, Q58, Q59, Q60, Q61, Q62, Q63, Q64, Q65, Q66, Q67, Q68, Q69, Q70]), "radius" : .1 * mm, "tangentPropagation" : true, "allowEdgeOverflow" : false});
        }
        {
            var Q0;
            Q0=makeQuery(id+"F4.boolean.opBoolean","INTERSECT",EDGE,{"disambiguationData":[OD(1.0)],"derivedFrom":[makeQuery(id+"F1.opExtrude","SWEPT_FACE",FACE,{"disambiguationData":[OSD([sQuery(id+"F0.wireOp",EDGE,"E1")])]}),makeQuery(id+"F4.opExtrude","SWEPT_FACE",FACE,{"disambiguationData":[OSD([sQuery(id+"F3.wireOp",EDGE,"E40")])]})]});
            var Q1;
            Q1=makeQuery(id+"F4.boolean.opBoolean","INTERSECT",EDGE,{"disambiguationData":[OD(1.0)],"derivedFrom":[makeQuery(id+"F1.opExtrude","SWEPT_FACE",FACE,{"disambiguationData":[OSD([sQuery(id+"F0.wireOp",EDGE,"E1")])]}),makeQuery(id+"F4.opExtrude","SWEPT_FACE",FACE,{"disambiguationData":[OSD([sQuery(id+"F3.wireOp",EDGE,"E41.0")])]})]});
            var Q2;
            Q2=makeQuery(id+"F4.boolean.opBoolean","INTERSECT",EDGE,{"disambiguationData":[OD(1.0)],"derivedFrom":[makeQuery(id+"F1.opExtrude","SWEPT_FACE",FACE,{"disambiguationData":[OSD([sQuery(id+"F0.wireOp",EDGE,"E1")])]}),makeQuery(id+"F4.opExtrude","SWEPT_FACE",FACE,{"disambiguationData":[OSD([sQuery(id+"F3.wireOp",EDGE,"E42")])]})]});
            var Q3;
            Q3=makeQuery(id+"F4.boolean.opBoolean","INTERSECT",EDGE,{"disambiguationData":[OD(1.0)],"derivedFrom":[makeQuery(id+"F1.opExtrude","SWEPT_FACE",FACE,{"disambiguationData":[OSD([sQuery(id+"F0.wireOp",EDGE,"E1")])]}),makeQuery(id+"F4.opExtrude","SWEPT_FACE",FACE,{"disambiguationData":[OSD([sQuery(id+"F3.wireOp",EDGE,"E43")])]})]});
            var Q4;
            {var subQ0=sQuery(id+"F3.wireOp",EDGE,"E30");Q4=makeQuery(id+"F4.boolean.opBoolean","INTERSECT",EDGE,{"disambiguationData":[OD(1.0)],"derivedFrom":[makeQuery(id+"F1.opExtrude","SWEPT_FACE",FACE,{"disambiguationData":[OSD([sQuery(id+"F0.wireOp",EDGE,"E1")])]}),makeQuery(id+"F4.opExtrude","SWEPT_FACE",FACE,{"disambiguationData":[OSD([subQ0]),TDD([makeQuery(id+"F3.imprint","IMPRINT",EDGE,{"disambiguationData":[TD([[makeQuery(id+"F3.imprint","INTERSECT",VERTEX,{"derivedFrom":[subQ0,sQuery(id+"F3.wireOp",EDGE,"E33")]}),1.0]])],"derivedFrom":subQ0})])]})]});}
            var Q5;
            {var subQ0=sQuery(id+"F3.wireOp",EDGE,"E31.0");Q5=makeQuery(id+"F4.boolean.opBoolean","INTERSECT",EDGE,{"disambiguationData":[OD(1.0)],"derivedFrom":[makeQuery(id+"F1.opExtrude","SWEPT_FACE",FACE,{"disambiguationData":[OSD([sQuery(id+"F0.wireOp",EDGE,"E1")])]}),makeQuery(id+"F4.opExtrude","SWEPT_FACE",FACE,{"disambiguationData":[OSD([subQ0]),TDD([makeQuery(id+"F3.imprint","IMPRINT",EDGE,{"disambiguationData":[TD([[makeQuery(id+"F3.imprint","INTERSECT",VERTEX,{"derivedFrom":[subQ0,sQuery(id+"F3.wireOp",EDGE,"E34")]}),1.0]])],"derivedFrom":subQ0})])]})]});}
            var Q6;
            Q6=makeQuery(id+"F4.boolean.opBoolean","INTERSECT",EDGE,{"disambiguationData":[OD(1.0)],"derivedFrom":[makeQuery(id+"F1.opExtrude","SWEPT_FACE",FACE,{"disambiguationData":[OSD([sQuery(id+"F0.wireOp",EDGE,"E1")])]}),makeQuery(id+"F4.opExtrude","SWEPT_FACE",FACE,{"disambiguationData":[OSD([sQuery(id+"F3.wireOp",EDGE,"E33")])]})]});
            var Q7;
            Q7=makeQuery(id+"F4.boolean.opBoolean","INTERSECT",EDGE,{"disambiguationData":[OD(1.0)],"derivedFrom":[makeQuery(id+"F1.opExtrude","SWEPT_FACE",FACE,{"disambiguationData":[OSD([sQuery(id+"F0.wireOp",EDGE,"E1")])]}),makeQuery(id+"F4.opExtrude","SWEPT_FACE",FACE,{"disambiguationData":[OSD([sQuery(id+"F3.wireOp",EDGE,"E34")])]})]});
            var Q8;
            Q8=makeQuery(id+"F4.boolean.opBoolean","INTERSECT",EDGE,{"disambiguationData":[OD(1.0)],"derivedFrom":[makeQuery(id+"F1.opExtrude","SWEPT_FACE",FACE,{"disambiguationData":[OSD([sQuery(id+"F0.wireOp",EDGE,"E1")])]}),makeQuery(id+"F4.opExtrude","SWEPT_FACE",FACE,{"disambiguationData":[OSD([sQuery(id+"F3.wireOp",EDGE,"E44")])]})]});
            var Q9;
            {var subQ0=sQuery(id+"F3.wireOp",EDGE,"E30");Q9=makeQuery(id+"F4.boolean.opBoolean","INTERSECT",EDGE,{"disambiguationData":[OD(1.0)],"derivedFrom":[makeQuery(id+"F1.opExtrude","SWEPT_FACE",FACE,{"disambiguationData":[OSD([sQuery(id+"F0.wireOp",EDGE,"E1")])]}),makeQuery(id+"F4.opExtrude","SWEPT_FACE",FACE,{"disambiguationData":[OSD([subQ0]),TDD([makeQuery(id+"F3.imprint","IMPRINT",EDGE,{"disambiguationData":[TD([[makeQuery(id+"F3.imprint","INTERSECT",VERTEX,{"derivedFrom":[subQ0,sQuery(id+"F3.wireOp",EDGE,"E44")]}),1.0]])],"derivedFrom":subQ0})])]})]});}
            var Q10;
            Q10=makeQuery(id+"F4.boolean.opBoolean","INTERSECT",EDGE,{"disambiguationData":[OD(1.0)],"derivedFrom":[makeQuery(id+"F1.opExtrude","SWEPT_FACE",FACE,{"disambiguationData":[OSD([sQuery(id+"F0.wireOp",EDGE,"E1")])]}),makeQuery(id+"F4.opExtrude","SWEPT_FACE",FACE,{"disambiguationData":[OSD([sQuery(id+"F3.wireOp",EDGE,"E35")])]})]});
            var Q11;
            Q11=makeQuery(id+"F4.boolean.opBoolean","INTERSECT",EDGE,{"disambiguationData":[OD(1.0)],"derivedFrom":[makeQuery(id+"F1.opExtrude","SWEPT_FACE",FACE,{"disambiguationData":[OSD([sQuery(id+"F0.wireOp",EDGE,"E1")])]}),makeQuery(id+"F4.opExtrude","SWEPT_FACE",FACE,{"disambiguationData":[OSD([sQuery(id+"F3.wireOp",EDGE,"E36.0")])]})]});
            var Q12;
            Q12=makeQuery(id+"F4.boolean.opBoolean","INTERSECT",EDGE,{"disambiguationData":[OD(1.0)],"derivedFrom":[makeQuery(id+"F1.opExtrude","SWEPT_FACE",FACE,{"disambiguationData":[OSD([sQuery(id+"F0.wireOp",EDGE,"E1")])]}),makeQuery(id+"F4.opExtrude","SWEPT_FACE",FACE,{"disambiguationData":[OSD([sQuery(id+"F3.wireOp",EDGE,"E39")])]})]});
            var Q13;
            Q13=makeQuery(id+"F4.boolean.opBoolean","INTERSECT",EDGE,{"disambiguationData":[OD(1.0)],"derivedFrom":[makeQuery(id+"F1.opExtrude","SWEPT_FACE",FACE,{"disambiguationData":[OSD([sQuery(id+"F0.wireOp",EDGE,"E1")])]}),makeQuery(id+"F4.opExtrude","SWEPT_FACE",FACE,{"disambiguationData":[OSD([sQuery(id+"F3.wireOp",EDGE,"E37")])]})]});
            var Q14;
            Q14=makeQuery(id+"F4.boolean.opBoolean","INTERSECT",EDGE,{"disambiguationData":[OD(1.0)],"derivedFrom":[makeQuery(id+"F1.opExtrude","SWEPT_FACE",FACE,{"disambiguationData":[OSD([sQuery(id+"F0.wireOp",EDGE,"E1")])]}),makeQuery(id+"F4.opExtrude","SWEPT_FACE",FACE,{"disambiguationData":[OSD([sQuery(id+"F3.wireOp",EDGE,"E38")])]})]});
            var Q15;
            {var subQ0=sQuery(id+"F3.wireOp",EDGE,"E31.0");Q15=makeQuery(id+"F4.boolean.opBoolean","INTERSECT",EDGE,{"disambiguationData":[OD(1.0)],"derivedFrom":[makeQuery(id+"F1.opExtrude","SWEPT_FACE",FACE,{"disambiguationData":[OSD([sQuery(id+"F0.wireOp",EDGE,"E1")])]}),makeQuery(id+"F4.opExtrude","SWEPT_FACE",FACE,{"disambiguationData":[OSD([subQ0]),TDD([makeQuery(id+"F3.imprint","IMPRINT",EDGE,{"disambiguationData":[TD([[makeQuery(id+"F3.imprint","INTERSECT",VERTEX,{"derivedFrom":[subQ0,sQuery(id+"F3.wireOp",EDGE,"E39")]}),1.0]])],"derivedFrom":subQ0})])]})]});}
            var Q16;
            {var subQ0=sQuery(id+"F3.wireOp",EDGE,"E65.2");Q16=makeQuery(id+"F4.boolean.opBoolean","INTERSECT",EDGE,{"disambiguationData":[OD(1.0)],"derivedFrom":[makeQuery(id+"F1.opExtrude","SWEPT_FACE",FACE,{"disambiguationData":[OSD([sQuery(id+"F0.wireOp",EDGE,"E1")])]}),makeQuery(id+"F4.opExtrude","SWEPT_FACE",FACE,{"disambiguationData":[OSD([subQ0]),TDD([makeQuery(id+"F3.imprint","IMPRINT",EDGE,{"disambiguationData":[TD([[makeQuery(id+"F3.imprint","INTERSECT",VERTEX,{"derivedFrom":[sQuery(id+"F3.wireOp",EDGE,"E65.1"),subQ0]}),-1.0]])],"derivedFrom":subQ0})])]})]});}
            var Q17;
            Q17=makeQuery(id+"F4.boolean.opBoolean","INTERSECT",EDGE,{"disambiguationData":[OD(1.0)],"derivedFrom":[makeQuery(id+"F1.opExtrude","SWEPT_FACE",FACE,{"disambiguationData":[OSD([sQuery(id+"F0.wireOp",EDGE,"E1")])]}),makeQuery(id+"F4.opExtrude","SWEPT_FACE",FACE,{"disambiguationData":[OSD([sQuery(id+"F3.wireOp",EDGE,"E65.1")])]})]});
            var Q18;
            Q18=makeQuery(id+"F4.boolean.opBoolean","INTERSECT",EDGE,{"disambiguationData":[OD(1.0)],"derivedFrom":[makeQuery(id+"F1.opExtrude","SWEPT_FACE",FACE,{"disambiguationData":[OSD([sQuery(id+"F0.wireOp",EDGE,"E1")])]}),makeQuery(id+"F4.opExtrude","SWEPT_FACE",FACE,{"disambiguationData":[OSD([sQuery(id+"F3.wireOp",EDGE,"E65.0")])]})]});
            var Q19;
            Q19=makeQuery(id+"F4.boolean.opBoolean","INTERSECT",EDGE,{"disambiguationData":[OD(1.0)],"derivedFrom":[makeQuery(id+"F1.opExtrude","SWEPT_FACE",FACE,{"disambiguationData":[OSD([sQuery(id+"F0.wireOp",EDGE,"E1")])]}),makeQuery(id+"F4.opExtrude","SWEPT_FACE",FACE,{"disambiguationData":[OSD([sQuery(id+"F3.wireOp",EDGE,"E63")])]})]});
            var Q20;
            Q20=makeQuery(id+"F4.boolean.opBoolean","INTERSECT",EDGE,{"disambiguationData":[OD(1.0)],"derivedFrom":[makeQuery(id+"F1.opExtrude","SWEPT_FACE",FACE,{"disambiguationData":[OSD([sQuery(id+"F0.wireOp",EDGE,"E1")])]}),makeQuery(id+"F4.opExtrude","SWEPT_FACE",FACE,{"disambiguationData":[OSD([sQuery(id+"F3.wireOp",EDGE,"E21"),sQuery(id+"F3.wireOp",EDGE,"E68")])]})]});
            var Q21;
            Q21=makeQuery(id+"F4.boolean.opBoolean","INTERSECT",EDGE,{"disambiguationData":[OD(1.0)],"derivedFrom":[makeQuery(id+"F1.opExtrude","SWEPT_FACE",FACE,{"disambiguationData":[OSD([sQuery(id+"F0.wireOp",EDGE,"E1")])]}),makeQuery(id+"F4.opExtrude","SWEPT_FACE",FACE,{"disambiguationData":[OSD([sQuery(id+"F3.wireOp",EDGE,"E60.1")])]})]});
            var Q22;
            Q22=makeQuery(id+"F4.boolean.opBoolean","INTERSECT",EDGE,{"disambiguationData":[OD(1.0)],"derivedFrom":[makeQuery(id+"F1.opExtrude","SWEPT_FACE",FACE,{"disambiguationData":[OSD([sQuery(id+"F0.wireOp",EDGE,"E1")])]}),makeQuery(id+"F4.opExtrude","SWEPT_FACE",FACE,{"disambiguationData":[OSD([sQuery(id+"F3.wireOp",EDGE,"E60.2")])]})]});
            var Q23;
            Q23=makeQuery(id+"F4.boolean.opBoolean","INTERSECT",EDGE,{"disambiguationData":[OD(1.0)],"derivedFrom":[makeQuery(id+"F1.opExtrude","SWEPT_FACE",FACE,{"disambiguationData":[OSD([sQuery(id+"F0.wireOp",EDGE,"E1")])]}),makeQuery(id+"F4.opExtrude","SWEPT_FACE",FACE,{"disambiguationData":[OSD([sQuery(id+"F3.wireOp",EDGE,"E60.0")])]})]});
            var Q24;
            Q24=makeQuery(id+"F4.boolean.opBoolean","INTERSECT",EDGE,{"disambiguationData":[OD(1.0)],"derivedFrom":[makeQuery(id+"F1.opExtrude","SWEPT_FACE",FACE,{"disambiguationData":[OSD([sQuery(id+"F0.wireOp",EDGE,"E1")])]}),makeQuery(id+"F4.opExtrude","SWEPT_FACE",FACE,{"disambiguationData":[OSD([sQuery(id+"F3.wireOp",EDGE,"E24.bottom")])]})]});
            var Q25;
            Q25=makeQuery(id+"F4.boolean.opBoolean","INTERSECT",EDGE,{"disambiguationData":[OD(1.0)],"derivedFrom":[makeQuery(id+"F1.opExtrude","SWEPT_FACE",FACE,{"disambiguationData":[OSD([sQuery(id+"F0.wireOp",EDGE,"E1")])]}),makeQuery(id+"F4.opExtrude","SWEPT_FACE",FACE,{"disambiguationData":[OSD([sQuery(id+"F3.wireOp",EDGE,"E24.left")])]})]});
            var Q26;
            Q26=makeQuery(id+"F4.boolean.opBoolean","INTERSECT",EDGE,{"disambiguationData":[OD(1.0)],"derivedFrom":[makeQuery(id+"F1.opExtrude","SWEPT_FACE",FACE,{"disambiguationData":[OSD([sQuery(id+"F0.wireOp",EDGE,"E1")])]}),makeQuery(id+"F4.opExtrude","SWEPT_FACE",FACE,{"disambiguationData":[OSD([sQuery(id+"F3.wireOp",EDGE,"E24.right")])]})]});
            var Q27;
            Q27=makeQuery(id+"F4.boolean.opBoolean","INTERSECT",EDGE,{"disambiguationData":[OD(1.0)],"derivedFrom":[makeQuery(id+"F1.opExtrude","SWEPT_FACE",FACE,{"disambiguationData":[OSD([sQuery(id+"F0.wireOp",EDGE,"E1")])]}),makeQuery(id+"F4.opExtrude","SWEPT_FACE",FACE,{"disambiguationData":[OSD([sQuery(id+"F3.wireOp",EDGE,"E25.left")])]})]});
            var Q28;
            Q28=makeQuery(id+"F4.boolean.opBoolean","INTERSECT",EDGE,{"disambiguationData":[OD(1.0)],"derivedFrom":[makeQuery(id+"F1.opExtrude","SWEPT_FACE",FACE,{"disambiguationData":[OSD([sQuery(id+"F0.wireOp",EDGE,"E1")])]}),makeQuery(id+"F4.opExtrude","SWEPT_FACE",FACE,{"disambiguationData":[OSD([sQuery(id+"F3.wireOp",EDGE,"E25.top")])]})]});
            var Q29;
            Q29=makeQuery(id+"F4.boolean.opBoolean","INTERSECT",EDGE,{"disambiguationData":[OD(1.0)],"derivedFrom":[makeQuery(id+"F1.opExtrude","SWEPT_FACE",FACE,{"disambiguationData":[OSD([sQuery(id+"F0.wireOp",EDGE,"E1")])]}),makeQuery(id+"F4.opExtrude","SWEPT_FACE",FACE,{"disambiguationData":[OSD([sQuery(id+"F3.wireOp",EDGE,"E25.right")])]})]});
            var Q30;
            Q30=makeQuery(id+"F4.boolean.opBoolean","INTERSECT",EDGE,{"disambiguationData":[OD(1.0)],"derivedFrom":[makeQuery(id+"F1.opExtrude","SWEPT_FACE",FACE,{"disambiguationData":[OSD([sQuery(id+"F0.wireOp",EDGE,"E1")])]}),makeQuery(id+"F4.opExtrude","SWEPT_FACE",FACE,{"disambiguationData":[OSD([sQuery(id+"F3.wireOp",EDGE,"E28")])]})]});
            var Q31;
            Q31=makeQuery(id+"F4.boolean.opBoolean","INTERSECT",EDGE,{"disambiguationData":[OD(1.0)],"derivedFrom":[makeQuery(id+"F1.opExtrude","SWEPT_FACE",FACE,{"disambiguationData":[OSD([sQuery(id+"F0.wireOp",EDGE,"E1")])]}),makeQuery(id+"F4.opExtrude","SWEPT_FACE",FACE,{"disambiguationData":[OSD([sQuery(id+"F3.wireOp",EDGE,"E26.top")])]})]});
            var Q32;
            Q32=makeQuery(id+"F4.boolean.opBoolean","INTERSECT",EDGE,{"disambiguationData":[OD(1.0)],"derivedFrom":[makeQuery(id+"F1.opExtrude","SWEPT_FACE",FACE,{"disambiguationData":[OSD([sQuery(id+"F0.wireOp",EDGE,"E1")])]}),makeQuery(id+"F4.opExtrude","SWEPT_FACE",FACE,{"disambiguationData":[OSD([sQuery(id+"F3.wireOp",EDGE,"E26.right")])]})]});
            var Q33;
            Q33=makeQuery(id+"F4.boolean.opBoolean","INTERSECT",EDGE,{"disambiguationData":[OD(1.0)],"derivedFrom":[makeQuery(id+"F1.opExtrude","SWEPT_FACE",FACE,{"disambiguationData":[OSD([sQuery(id+"F0.wireOp",EDGE,"E1")])]}),makeQuery(id+"F4.opExtrude","SWEPT_FACE",FACE,{"disambiguationData":[OSD([sQuery(id+"F3.wireOp",EDGE,"E27.left")])]})]});
            var Q34;
            Q34=makeQuery(id+"F4.boolean.opBoolean","INTERSECT",EDGE,{"disambiguationData":[OD(1.0)],"derivedFrom":[makeQuery(id+"F1.opExtrude","SWEPT_FACE",FACE,{"disambiguationData":[OSD([sQuery(id+"F0.wireOp",EDGE,"E1")])]}),makeQuery(id+"F4.opExtrude","SWEPT_FACE",FACE,{"disambiguationData":[OSD([sQuery(id+"F3.wireOp",EDGE,"E27.top")])]})]});
            var Q35;
            Q35=makeQuery(id+"F4.boolean.opBoolean","INTERSECT",EDGE,{"disambiguationData":[OD(1.0)],"derivedFrom":[makeQuery(id+"F1.opExtrude","SWEPT_FACE",FACE,{"disambiguationData":[OSD([sQuery(id+"F0.wireOp",EDGE,"E1")])]}),makeQuery(id+"F4.opExtrude","SWEPT_FACE",FACE,{"disambiguationData":[OSD([sQuery(id+"F3.wireOp",EDGE,"E27.right")])]})]});
            var Q36;
            Q36=makeQuery(id+"F4.boolean.opBoolean","INTERSECT",EDGE,{"disambiguationData":[OD(1.0)],"derivedFrom":[makeQuery(id+"F1.opExtrude","SWEPT_FACE",FACE,{"disambiguationData":[OSD([sQuery(id+"F0.wireOp",EDGE,"E1")])]}),makeQuery(id+"F4.opExtrude","SWEPT_FACE",FACE,{"disambiguationData":[OSD([sQuery(id+"F3.wireOp",EDGE,"E61.0")])]})]});
            var Q37;
            Q37=makeQuery(id+"F4.boolean.opBoolean","INTERSECT",EDGE,{"disambiguationData":[OD(1.0)],"derivedFrom":[makeQuery(id+"F1.opExtrude","SWEPT_FACE",FACE,{"disambiguationData":[OSD([sQuery(id+"F0.wireOp",EDGE,"E1")])]}),makeQuery(id+"F4.opExtrude","SWEPT_FACE",FACE,{"disambiguationData":[OSD([sQuery(id+"F3.wireOp",EDGE,"E61.1")])]})]});
            var Q38;
            Q38=makeQuery(id+"F4.boolean.opBoolean","INTERSECT",EDGE,{"disambiguationData":[OD(1.0)],"derivedFrom":[makeQuery(id+"F1.opExtrude","SWEPT_FACE",FACE,{"disambiguationData":[OSD([sQuery(id+"F0.wireOp",EDGE,"E1")])]}),makeQuery(id+"F4.opExtrude","SWEPT_FACE",FACE,{"disambiguationData":[OSD([sQuery(id+"F3.wireOp",EDGE,"E61.2")])]})]});
            var Q39;
            Q39=makeQuery(id+"F4.boolean.opBoolean","INTERSECT",EDGE,{"disambiguationData":[OD(1.0)],"derivedFrom":[makeQuery(id+"F1.opExtrude","SWEPT_FACE",FACE,{"disambiguationData":[OSD([sQuery(id+"F0.wireOp",EDGE,"E1")])]}),makeQuery(id+"F4.opExtrude","SWEPT_FACE",FACE,{"disambiguationData":[OSD([sQuery(id+"F3.wireOp",EDGE,"E62.1")])]})]});
            var Q40;
            Q40=makeQuery(id+"F4.boolean.opBoolean","INTERSECT",EDGE,{"disambiguationData":[OD(1.0)],"derivedFrom":[makeQuery(id+"F1.opExtrude","SWEPT_FACE",FACE,{"disambiguationData":[OSD([sQuery(id+"F0.wireOp",EDGE,"E1")])]}),makeQuery(id+"F4.opExtrude","SWEPT_FACE",FACE,{"disambiguationData":[OSD([sQuery(id+"F3.wireOp",EDGE,"E62.2")])]})]});
            var Q41;
            Q41=makeQuery(id+"F4.boolean.opBoolean","INTERSECT",EDGE,{"disambiguationData":[OD(1.0)],"derivedFrom":[makeQuery(id+"F1.opExtrude","SWEPT_FACE",FACE,{"disambiguationData":[OSD([sQuery(id+"F0.wireOp",EDGE,"E1")])]}),makeQuery(id+"F4.opExtrude","SWEPT_FACE",FACE,{"disambiguationData":[OSD([sQuery(id+"F3.wireOp",EDGE,"E62.0")])]})]});
            var Q42;
            {var subQ0=sQuery(id+"F3.wireOp",EDGE,"E57.0");Q42=makeQuery(id+"F4.boolean.opBoolean","INTERSECT",EDGE,{"disambiguationData":[OD(1.0)],"derivedFrom":[makeQuery(id+"F1.opExtrude","SWEPT_FACE",FACE,{"disambiguationData":[OSD([sQuery(id+"F0.wireOp",EDGE,"E1")])]}),makeQuery(id+"F4.opExtrude","SWEPT_FACE",FACE,{"disambiguationData":[OSD([subQ0]),TDD([makeQuery(id+"F3.imprint","IMPRINT",EDGE,{"disambiguationData":[TD([[makeQuery(id+"F3.imprint","INTERSECT",VERTEX,{"derivedFrom":[sQuery(id+"F3.wireOp",EDGE,"E49.MirrorCS"),subQ0]}),-1.0]])],"derivedFrom":subQ0})])]})]});}
            var Q43;
            {var subQ0=sQuery(id+"F3.wireOp",EDGE,"E56.MirrorCS");Q43=makeQuery(id+"F4.boolean.opBoolean","INTERSECT",EDGE,{"disambiguationData":[OD(1.0)],"derivedFrom":[makeQuery(id+"F1.opExtrude","SWEPT_FACE",FACE,{"disambiguationData":[OSD([sQuery(id+"F0.wireOp",EDGE,"E1")])]}),makeQuery(id+"F4.opExtrude","SWEPT_FACE",FACE,{"disambiguationData":[OSD([subQ0]),TDD([makeQuery(id+"F3.imprint","IMPRINT",EDGE,{"disambiguationData":[TD([[makeQuery(id+"F3.imprint","INTERSECT",VERTEX,{"derivedFrom":[sQuery(id+"F3.wireOp",EDGE,"E50.MirrorCS"),subQ0]}),1.0]])],"derivedFrom":subQ0})])]})]});}
            var Q44;
            Q44=makeQuery(id+"F4.boolean.opBoolean","INTERSECT",EDGE,{"disambiguationData":[OD(1.0)],"derivedFrom":[makeQuery(id+"F1.opExtrude","SWEPT_FACE",FACE,{"disambiguationData":[OSD([sQuery(id+"F0.wireOp",EDGE,"E1")])]}),makeQuery(id+"F4.opExtrude","SWEPT_FACE",FACE,{"disambiguationData":[OSD([sQuery(id+"F3.wireOp",EDGE,"E52.MirrorCS")])]})]});
            var Q45;
            Q45=makeQuery(id+"F4.boolean.opBoolean","INTERSECT",EDGE,{"disambiguationData":[OD(1.0)],"derivedFrom":[makeQuery(id+"F1.opExtrude","SWEPT_FACE",FACE,{"disambiguationData":[OSD([sQuery(id+"F0.wireOp",EDGE,"E1")])]}),makeQuery(id+"F4.opExtrude","SWEPT_FACE",FACE,{"disambiguationData":[OSD([sQuery(id+"F3.wireOp",EDGE,"E50.MirrorCS")])]})]});
            var Q46;
            Q46=makeQuery(id+"F4.boolean.opBoolean","INTERSECT",EDGE,{"disambiguationData":[OD(1.0)],"derivedFrom":[makeQuery(id+"F1.opExtrude","SWEPT_FACE",FACE,{"disambiguationData":[OSD([sQuery(id+"F0.wireOp",EDGE,"E1")])]}),makeQuery(id+"F4.opExtrude","SWEPT_FACE",FACE,{"disambiguationData":[OSD([sQuery(id+"F3.wireOp",EDGE,"E59.0")])]})]});
            var Q47;
            Q47=makeQuery(id+"F4.boolean.opBoolean","INTERSECT",EDGE,{"disambiguationData":[OD(1.0)],"derivedFrom":[makeQuery(id+"F1.opExtrude","SWEPT_FACE",FACE,{"disambiguationData":[OSD([sQuery(id+"F0.wireOp",EDGE,"E1")])]}),makeQuery(id+"F4.opExtrude","SWEPT_FACE",FACE,{"disambiguationData":[OSD([sQuery(id+"F3.wireOp",EDGE,"E55.MirrorCS")])]})]});
            var Q48;
            Q48=makeQuery(id+"F4.boolean.opBoolean","INTERSECT",EDGE,{"disambiguationData":[OD(1.0)],"derivedFrom":[makeQuery(id+"F1.opExtrude","SWEPT_FACE",FACE,{"disambiguationData":[OSD([sQuery(id+"F0.wireOp",EDGE,"E1")])]}),makeQuery(id+"F4.opExtrude","SWEPT_FACE",FACE,{"disambiguationData":[OSD([sQuery(id+"F3.wireOp",EDGE,"E54.MirrorCS")])]})]});
            var Q49;
            Q49=makeQuery(id+"F4.boolean.opBoolean","INTERSECT",EDGE,{"disambiguationData":[OD(1.0)],"derivedFrom":[makeQuery(id+"F1.opExtrude","SWEPT_FACE",FACE,{"disambiguationData":[OSD([sQuery(id+"F0.wireOp",EDGE,"E1")])]}),makeQuery(id+"F4.opExtrude","SWEPT_FACE",FACE,{"disambiguationData":[OSD([sQuery(id+"F3.wireOp",EDGE,"E53.MirrorCS")])]})]});
            var Q50;
            Q50=makeQuery(id+"F4.boolean.opBoolean","INTERSECT",EDGE,{"disambiguationData":[OD(1.0)],"derivedFrom":[makeQuery(id+"F1.opExtrude","SWEPT_FACE",FACE,{"disambiguationData":[OSD([sQuery(id+"F0.wireOp",EDGE,"E1")])]}),makeQuery(id+"F4.opExtrude","SWEPT_FACE",FACE,{"disambiguationData":[OSD([sQuery(id+"F3.wireOp",EDGE,"E51.MirrorCS")])]})]});
            var Q51;
            Q51=makeQuery(id+"F4.boolean.opBoolean","INTERSECT",EDGE,{"disambiguationData":[OD(1.0)],"derivedFrom":[makeQuery(id+"F1.opExtrude","SWEPT_FACE",FACE,{"disambiguationData":[OSD([sQuery(id+"F0.wireOp",EDGE,"E1")])]}),makeQuery(id+"F4.opExtrude","SWEPT_FACE",FACE,{"disambiguationData":[OSD([sQuery(id+"F3.wireOp",EDGE,"E49.MirrorCS")])]})]});
            var Q52;
            Q52=makeQuery(id+"F4.boolean.opBoolean","INTERSECT",EDGE,{"disambiguationData":[OD(1.0)],"derivedFrom":[makeQuery(id+"F1.opExtrude","SWEPT_FACE",FACE,{"disambiguationData":[OSD([sQuery(id+"F0.wireOp",EDGE,"E1")])]}),makeQuery(id+"F4.opExtrude","SWEPT_FACE",FACE,{"disambiguationData":[OSD([sQuery(id+"F3.wireOp",EDGE,"E58.0")])]})]});
            var Q53;
            {var subQ0=sQuery(id+"F3.wireOp",EDGE,"E56.MirrorCS");Q53=makeQuery(id+"F4.boolean.opBoolean","INTERSECT",EDGE,{"disambiguationData":[OD(1.0)],"derivedFrom":[makeQuery(id+"F1.opExtrude","SWEPT_FACE",FACE,{"disambiguationData":[OSD([sQuery(id+"F0.wireOp",EDGE,"E1")])]}),makeQuery(id+"F4.opExtrude","SWEPT_FACE",FACE,{"disambiguationData":[OSD([subQ0]),TDD([makeQuery(id+"F3.imprint","IMPRINT",EDGE,{"disambiguationData":[TD([[makeQuery(id+"F3.imprint","INTERSECT",VERTEX,{"derivedFrom":[sQuery(id+"F3.wireOp",EDGE,"E51.MirrorCS"),subQ0]}),1.0]])],"derivedFrom":subQ0})])]})]});}
            var Q54;
            Q54=makeQuery(id+"F4.boolean.opBoolean","INTERSECT",EDGE,{"disambiguationData":[OD(1.0)],"derivedFrom":[makeQuery(id+"F1.opExtrude","SWEPT_FACE",FACE,{"disambiguationData":[OSD([sQuery(id+"F0.wireOp",EDGE,"E1")])]}),makeQuery(id+"F4.opExtrude","SWEPT_FACE",FACE,{"disambiguationData":[OSD([sQuery(id+"F3.wireOp",EDGE,"E48.MirrorCS")])]})]});
            var Q55;
            {var subQ0=sQuery(id+"F3.wireOp",EDGE,"E57.0");Q55=makeQuery(id+"F4.boolean.opBoolean","INTERSECT",EDGE,{"disambiguationData":[OD(1.0)],"derivedFrom":[makeQuery(id+"F1.opExtrude","SWEPT_FACE",FACE,{"disambiguationData":[OSD([sQuery(id+"F0.wireOp",EDGE,"E1")])]}),makeQuery(id+"F4.opExtrude","SWEPT_FACE",FACE,{"disambiguationData":[OSD([subQ0]),TDD([makeQuery(id+"F3.imprint","IMPRINT",EDGE,{"disambiguationData":[TD([[makeQuery(id+"F3.imprint","INTERSECT",VERTEX,{"derivedFrom":[sQuery(id+"F3.wireOp",EDGE,"E48.MirrorCS"),subQ0]}),1.0]])],"derivedFrom":subQ0})])]})]});}
            var Q56;
            Q56=makeQuery(id+"F4.boolean.opBoolean","INTERSECT",EDGE,{"disambiguationData":[OD(1.0)],"derivedFrom":[makeQuery(id+"F1.opExtrude","SWEPT_FACE",FACE,{"disambiguationData":[OSD([sQuery(id+"F0.wireOp",EDGE,"E1")])]}),makeQuery(id+"F4.opExtrude","SWEPT_FACE",FACE,{"disambiguationData":[OSD([sQuery(id+"F3.wireOp",EDGE,"E46.MirrorCS")])]})]});
            var Q57;
            Q57=makeQuery(id+"F4.boolean.opBoolean","INTERSECT",EDGE,{"disambiguationData":[OD(1.0)],"derivedFrom":[makeQuery(id+"F1.opExtrude","SWEPT_FACE",FACE,{"disambiguationData":[OSD([sQuery(id+"F0.wireOp",EDGE,"E1")])]}),makeQuery(id+"F4.opExtrude","SWEPT_FACE",FACE,{"disambiguationData":[OSD([sQuery(id+"F3.wireOp",EDGE,"E47.MirrorCS")])]})]});
            var Q58;
            Q58=makeQuery(id+"F4.boolean.opBoolean","INTERSECT",EDGE,{"disambiguationData":[OD(1.0)],"derivedFrom":[makeQuery(id+"F1.opExtrude","SWEPT_FACE",FACE,{"disambiguationData":[OSD([sQuery(id+"F0.wireOp",EDGE,"E1")])]}),makeQuery(id+"F4.opExtrude","SWEPT_FACE",FACE,{"disambiguationData":[OSD([sQuery(id+"F3.wireOp",EDGE,"E65.3")])]})]});
            var Q59;
            Q59=makeQuery(id+"F4.boolean.opBoolean","INTERSECT",EDGE,{"disambiguationData":[OD(1.0)],"derivedFrom":[makeQuery(id+"F1.opExtrude","SWEPT_FACE",FACE,{"disambiguationData":[OSD([sQuery(id+"F0.wireOp",EDGE,"E1")])]}),makeQuery(id+"F4.opExtrude","SWEPT_FACE",FACE,{"disambiguationData":[OSD([sQuery(id+"F3.wireOp",EDGE,"E65.4")])]})]});
            var Q60;
            Q60=makeQuery(id+"F4.boolean.opBoolean","INTERSECT",EDGE,{"disambiguationData":[OD(1.0)],"derivedFrom":[makeQuery(id+"F1.opExtrude","SWEPT_FACE",FACE,{"disambiguationData":[OSD([sQuery(id+"F0.wireOp",EDGE,"E1")])]}),makeQuery(id+"F4.opExtrude","SWEPT_FACE",FACE,{"disambiguationData":[OSD([sQuery(id+"F3.wireOp",EDGE,"E64")])]})]});
            var Q61;
            Q61=makeQuery(id+"F4.boolean.opBoolean","INTERSECT",EDGE,{"disambiguationData":[OD(1.0)],"derivedFrom":[makeQuery(id+"F1.opExtrude","SWEPT_FACE",FACE,{"disambiguationData":[OSD([sQuery(id+"F0.wireOp",EDGE,"E1")])]}),makeQuery(id+"F4.opExtrude","SWEPT_FACE",FACE,{"disambiguationData":[OSD([sQuery(id+"F3.wireOp",EDGE,"E23"),sQuery(id+"F3.wireOp",EDGE,"E69")])]})]});
            var Q62;
            {var subQ0=sQuery(id+"F3.wireOp",EDGE,"E65.5");Q62=makeQuery(id+"F4.boolean.opBoolean","INTERSECT",EDGE,{"disambiguationData":[OD(1.0)],"derivedFrom":[makeQuery(id+"F1.opExtrude","SWEPT_FACE",FACE,{"disambiguationData":[OSD([sQuery(id+"F0.wireOp",EDGE,"E1")])]}),makeQuery(id+"F4.opExtrude","SWEPT_FACE",FACE,{"disambiguationData":[OSD([subQ0]),TDD([makeQuery(id+"F3.imprint","IMPRINT",EDGE,{"disambiguationData":[TD([[makeQuery(id+"F3.imprint","INTERSECT",VERTEX,{"derivedFrom":[sQuery(id+"F3.wireOp",EDGE,"E65.4"),subQ0]}),1.0]])],"derivedFrom":subQ0})])]})]});}
            var Q63;
            {var subQ0=sQuery(id+"F3.wireOp",EDGE,"E65.5");Q63=makeQuery(id+"F4.boolean.opBoolean","INTERSECT",EDGE,{"disambiguationData":[OD(1.0)],"derivedFrom":[makeQuery(id+"F1.opExtrude","SWEPT_FACE",FACE,{"disambiguationData":[OSD([sQuery(id+"F0.wireOp",EDGE,"E1")])]}),makeQuery(id+"F4.opExtrude","SWEPT_FACE",FACE,{"disambiguationData":[OSD([subQ0]),TDD([makeQuery(id+"F3.imprint","IMPRINT",EDGE,{"disambiguationData":[TD([[makeQuery(id+"F3.imprint","INTERSECT",VERTEX,{"derivedFrom":[subQ0,sQuery(id+"F3.wireOp",EDGE,"E65.6")]}),-1.0]])],"derivedFrom":subQ0})])]})]});}
            var Q64;
            {var subQ0=sQuery(id+"F3.wireOp",EDGE,"E65.6");Q64=makeQuery(id+"F4.boolean.opBoolean","INTERSECT",EDGE,{"disambiguationData":[OD(1.0)],"derivedFrom":[makeQuery(id+"F1.opExtrude","SWEPT_FACE",FACE,{"disambiguationData":[OSD([sQuery(id+"F0.wireOp",EDGE,"E1")])]}),makeQuery(id+"F4.opExtrude","SWEPT_FACE",FACE,{"disambiguationData":[OSD([subQ0]),TDD([makeQuery(id+"F3.imprint","IMPRINT",EDGE,{"disambiguationData":[TD([[makeQuery(id+"F3.imprint","INTERSECT",VERTEX,{"derivedFrom":[sQuery(id+"F3.wireOp",EDGE,"E65.5"),subQ0]}),1.0]])],"derivedFrom":subQ0})])]})]});}
            var Q65;
            Q65=makeQuery(id+"F4.boolean.opBoolean","INTERSECT",EDGE,{"disambiguationData":[OD(1.0)],"derivedFrom":[makeQuery(id+"F1.opExtrude","SWEPT_FACE",FACE,{"disambiguationData":[OSD([sQuery(id+"F0.wireOp",EDGE,"E1")])]}),makeQuery(id+"F4.opExtrude","SWEPT_FACE",FACE,{"disambiguationData":[OSD([sQuery(id+"F3.wireOp",EDGE,"E27.bottom")])]})]});
            var Q66;
            {var subQ0=sQuery(id+"F3.wireOp",EDGE,"E65.2");Q66=makeQuery(id+"F4.boolean.opBoolean","INTERSECT",EDGE,{"disambiguationData":[OD(1.0)],"derivedFrom":[makeQuery(id+"F1.opExtrude","SWEPT_FACE",FACE,{"disambiguationData":[OSD([sQuery(id+"F0.wireOp",EDGE,"E1")])]}),makeQuery(id+"F4.opExtrude","SWEPT_FACE",FACE,{"disambiguationData":[OSD([subQ0]),TDD([makeQuery(id+"F3.imprint","IMPRINT",EDGE,{"disambiguationData":[TD([[makeQuery(id+"F3.imprint","INTERSECT",VERTEX,{"derivedFrom":[subQ0,sQuery(id+"F3.wireOp",EDGE,"E65.6")]}),1.0]])],"derivedFrom":subQ0})])]})]});}
            var Q67;
            {var subQ0=sQuery(id+"F3.wireOp",EDGE,"E65.6");Q67=makeQuery(id+"F4.boolean.opBoolean","INTERSECT",EDGE,{"disambiguationData":[OD(1.0)],"derivedFrom":[makeQuery(id+"F1.opExtrude","SWEPT_FACE",FACE,{"disambiguationData":[OSD([sQuery(id+"F0.wireOp",EDGE,"E1")])]}),makeQuery(id+"F4.opExtrude","SWEPT_FACE",FACE,{"disambiguationData":[OSD([subQ0]),TDD([makeQuery(id+"F3.imprint","IMPRINT",EDGE,{"disambiguationData":[TD([[makeQuery(id+"F3.imprint","INTERSECT",VERTEX,{"derivedFrom":[sQuery(id+"F3.wireOp",EDGE,"E65.2"),subQ0]}),-1.0]])],"derivedFrom":subQ0})])]})]});}
            var Q68;
            Q68=makeQuery(id+"F4.boolean.opBoolean","INTERSECT",EDGE,{"disambiguationData":[OD(1.0)],"derivedFrom":[makeQuery(id+"F1.opExtrude","SWEPT_FACE",FACE,{"disambiguationData":[OSD([sQuery(id+"F0.wireOp",EDGE,"E1")])]}),makeQuery(id+"F4.opExtrude","SWEPT_FACE",FACE,{"disambiguationData":[OSD([sQuery(id+"F3.wireOp",EDGE,"E24.top")])]})]});
            var Q69;
            Q69=makeQuery(id+"F4.boolean.opBoolean","INTERSECT",EDGE,{"disambiguationData":[OD(1.0)],"derivedFrom":[makeQuery(id+"F1.opExtrude","SWEPT_FACE",FACE,{"disambiguationData":[OSD([sQuery(id+"F0.wireOp",EDGE,"E1")])]}),makeQuery(id+"F4.opExtrude","SWEPT_FACE",FACE,{"disambiguationData":[OSD([sQuery(id+"F3.wireOp",EDGE,"E25.bottom")])]})]});
            var Q70;
            Q70=makeQuery(id+"F4.boolean.opBoolean","INTERSECT",EDGE,{"disambiguationData":[OD(1.0)],"derivedFrom":[makeQuery(id+"F1.opExtrude","SWEPT_FACE",FACE,{"disambiguationData":[OSD([sQuery(id+"F0.wireOp",EDGE,"E1")])]}),makeQuery(id+"F4.opExtrude","SWEPT_FACE",FACE,{"disambiguationData":[OSD([sQuery(id+"F3.wireOp",EDGE,"E29")])]})]});
            fillet(context, id + "F17", {"entities" : qUnion([Q0, Q1, Q2, Q3, Q4, Q5, Q6, Q7, Q8, Q9, Q10, Q11, Q12, Q13, Q14, Q15, Q16, Q17, Q18, Q19, Q20, Q21, Q22, Q23, Q24, Q25, Q26, Q27, Q28, Q29, Q30, Q31, Q32, Q33, Q34, Q35, Q36, Q37, Q38, Q39, Q40, Q41, Q42, Q43, Q44, Q45, Q46, Q47, Q48, Q49, Q50, Q51, Q52, Q53, Q54, Q55, Q56, Q57, Q58, Q59, Q60, Q61, Q62, Q63, Q64, Q65, Q66, Q67, Q68, Q69, Q70]), "radius" : .1 * mm, "tangentPropagation" : true, "allowEdgeOverflow" : false});
        }
        {
            var Q0;
            Q0=makeQuery(id+"F6.boolean.opBoolean","INTERSECT",EDGE,{"disambiguationData":[OD(1.0)],"derivedFrom":[makeQuery(id+"F1.opExtrude","SWEPT_FACE",FACE,{"disambiguationData":[OSD([sQuery(id+"F0.wireOp",EDGE,"E1")])]}),makeQuery(id+"F6.opExtrude","SWEPT_FACE",FACE,{"disambiguationData":[OSD([sQuery(id+"F5.wireOp",EDGE,"E100")])]})]});
            var Q1;
            Q1=makeQuery(id+"F6.boolean.opBoolean","INTERSECT",EDGE,{"disambiguationData":[OD(1.0)],"derivedFrom":[makeQuery(id+"F1.opExtrude","SWEPT_FACE",FACE,{"disambiguationData":[OSD([sQuery(id+"F0.wireOp",EDGE,"E1")])]}),makeQuery(id+"F6.opExtrude","SWEPT_FACE",FACE,{"disambiguationData":[OSD([sQuery(id+"F5.wireOp",EDGE,"E101.0")])]})]});
            var Q2;
            Q2=makeQuery(id+"F6.boolean.opBoolean","INTERSECT",EDGE,{"disambiguationData":[OD(1.0)],"derivedFrom":[makeQuery(id+"F1.opExtrude","SWEPT_FACE",FACE,{"disambiguationData":[OSD([sQuery(id+"F0.wireOp",EDGE,"E1")])]}),makeQuery(id+"F6.opExtrude","SWEPT_FACE",FACE,{"disambiguationData":[OSD([sQuery(id+"F5.wireOp",EDGE,"E103")])]})]});
            var Q3;
            Q3=makeQuery(id+"F6.boolean.opBoolean","INTERSECT",EDGE,{"disambiguationData":[OD(1.0)],"derivedFrom":[makeQuery(id+"F1.opExtrude","SWEPT_FACE",FACE,{"disambiguationData":[OSD([sQuery(id+"F0.wireOp",EDGE,"E1")])]}),makeQuery(id+"F6.opExtrude","SWEPT_FACE",FACE,{"disambiguationData":[OSD([sQuery(id+"F5.wireOp",EDGE,"E102")])]})]});
            var Q4;
            {var subQ0=sQuery(id+"F5.wireOp",EDGE,"E90");Q4=makeQuery(id+"F6.boolean.opBoolean","INTERSECT",EDGE,{"disambiguationData":[OD(1.0)],"derivedFrom":[makeQuery(id+"F1.opExtrude","SWEPT_FACE",FACE,{"disambiguationData":[OSD([sQuery(id+"F0.wireOp",EDGE,"E1")])]}),makeQuery(id+"F6.opExtrude","SWEPT_FACE",FACE,{"disambiguationData":[OSD([subQ0]),TDD([makeQuery(id+"F5.imprint","IMPRINT",EDGE,{"disambiguationData":[TD([[makeQuery(id+"F5.imprint","INTERSECT",VERTEX,{"derivedFrom":[subQ0,sQuery(id+"F5.wireOp",EDGE,"E93")]}),1.0]])],"derivedFrom":subQ0})])]})]});}
            var Q5;
            {var subQ0=sQuery(id+"F5.wireOp",EDGE,"E91.0");Q5=makeQuery(id+"F6.boolean.opBoolean","INTERSECT",EDGE,{"disambiguationData":[OD(1.0)],"derivedFrom":[makeQuery(id+"F1.opExtrude","SWEPT_FACE",FACE,{"disambiguationData":[OSD([sQuery(id+"F0.wireOp",EDGE,"E1")])]}),makeQuery(id+"F6.opExtrude","SWEPT_FACE",FACE,{"disambiguationData":[OSD([subQ0]),TDD([makeQuery(id+"F5.imprint","IMPRINT",EDGE,{"disambiguationData":[TD([[makeQuery(id+"F5.imprint","INTERSECT",VERTEX,{"derivedFrom":[subQ0,sQuery(id+"F5.wireOp",EDGE,"E94")]}),1.0]])],"derivedFrom":subQ0})])]})]});}
            var Q6;
            Q6=makeQuery(id+"F6.boolean.opBoolean","INTERSECT",EDGE,{"disambiguationData":[OD(1.0)],"derivedFrom":[makeQuery(id+"F1.opExtrude","SWEPT_FACE",FACE,{"disambiguationData":[OSD([sQuery(id+"F0.wireOp",EDGE,"E1")])]}),makeQuery(id+"F6.opExtrude","SWEPT_FACE",FACE,{"disambiguationData":[OSD([sQuery(id+"F5.wireOp",EDGE,"E94")])]})]});
            var Q7;
            Q7=makeQuery(id+"F6.boolean.opBoolean","INTERSECT",EDGE,{"disambiguationData":[OD(1.0)],"derivedFrom":[makeQuery(id+"F1.opExtrude","SWEPT_FACE",FACE,{"disambiguationData":[OSD([sQuery(id+"F0.wireOp",EDGE,"E1")])]}),makeQuery(id+"F6.opExtrude","SWEPT_FACE",FACE,{"disambiguationData":[OSD([sQuery(id+"F5.wireOp",EDGE,"E93")])]})]});
            var Q8;
            Q8=makeQuery(id+"F6.boolean.opBoolean","INTERSECT",EDGE,{"disambiguationData":[OD(1.0)],"derivedFrom":[makeQuery(id+"F1.opExtrude","SWEPT_FACE",FACE,{"disambiguationData":[OSD([sQuery(id+"F0.wireOp",EDGE,"E1")])]}),makeQuery(id+"F6.opExtrude","SWEPT_FACE",FACE,{"disambiguationData":[OSD([sQuery(id+"F5.wireOp",EDGE,"E104")])]})]});
            var Q9;
            {var subQ0=sQuery(id+"F5.wireOp",EDGE,"E90");Q9=makeQuery(id+"F6.boolean.opBoolean","INTERSECT",EDGE,{"disambiguationData":[OD(1.0)],"derivedFrom":[makeQuery(id+"F1.opExtrude","SWEPT_FACE",FACE,{"disambiguationData":[OSD([sQuery(id+"F0.wireOp",EDGE,"E1")])]}),makeQuery(id+"F6.opExtrude","SWEPT_FACE",FACE,{"disambiguationData":[OSD([subQ0]),TDD([makeQuery(id+"F5.imprint","IMPRINT",EDGE,{"disambiguationData":[TD([[makeQuery(id+"F5.imprint","INTERSECT",VERTEX,{"derivedFrom":[subQ0,sQuery(id+"F5.wireOp",EDGE,"E104")]}),1.0]])],"derivedFrom":subQ0})])]})]});}
            var Q10;
            Q10=makeQuery(id+"F6.boolean.opBoolean","INTERSECT",EDGE,{"disambiguationData":[OD(1.0)],"derivedFrom":[makeQuery(id+"F1.opExtrude","SWEPT_FACE",FACE,{"disambiguationData":[OSD([sQuery(id+"F0.wireOp",EDGE,"E1")])]}),makeQuery(id+"F6.opExtrude","SWEPT_FACE",FACE,{"disambiguationData":[OSD([sQuery(id+"F5.wireOp",EDGE,"E95")])]})]});
            var Q11;
            Q11=makeQuery(id+"F6.boolean.opBoolean","INTERSECT",EDGE,{"disambiguationData":[OD(1.0)],"derivedFrom":[makeQuery(id+"F1.opExtrude","SWEPT_FACE",FACE,{"disambiguationData":[OSD([sQuery(id+"F0.wireOp",EDGE,"E1")])]}),makeQuery(id+"F6.opExtrude","SWEPT_FACE",FACE,{"disambiguationData":[OSD([sQuery(id+"F5.wireOp",EDGE,"E96.0")])]})]});
            var Q12;
            Q12=makeQuery(id+"F6.boolean.opBoolean","INTERSECT",EDGE,{"disambiguationData":[OD(1.0)],"derivedFrom":[makeQuery(id+"F1.opExtrude","SWEPT_FACE",FACE,{"disambiguationData":[OSD([sQuery(id+"F0.wireOp",EDGE,"E1")])]}),makeQuery(id+"F6.opExtrude","SWEPT_FACE",FACE,{"disambiguationData":[OSD([sQuery(id+"F5.wireOp",EDGE,"E99")])]})]});
            var Q13;
            {var subQ0=sQuery(id+"F5.wireOp",EDGE,"E91.0");Q13=makeQuery(id+"F6.boolean.opBoolean","INTERSECT",EDGE,{"disambiguationData":[OD(1.0)],"derivedFrom":[makeQuery(id+"F1.opExtrude","SWEPT_FACE",FACE,{"disambiguationData":[OSD([sQuery(id+"F0.wireOp",EDGE,"E1")])]}),makeQuery(id+"F6.opExtrude","SWEPT_FACE",FACE,{"disambiguationData":[OSD([subQ0]),TDD([makeQuery(id+"F5.imprint","IMPRINT",EDGE,{"disambiguationData":[TD([[makeQuery(id+"F5.imprint","INTERSECT",VERTEX,{"derivedFrom":[subQ0,sQuery(id+"F5.wireOp",EDGE,"E99")]}),1.0]])],"derivedFrom":subQ0})])]})]});}
            var Q14;
            Q14=makeQuery(id+"F6.boolean.opBoolean","INTERSECT",EDGE,{"disambiguationData":[OD(1.0)],"derivedFrom":[makeQuery(id+"F1.opExtrude","SWEPT_FACE",FACE,{"disambiguationData":[OSD([sQuery(id+"F0.wireOp",EDGE,"E1")])]}),makeQuery(id+"F6.opExtrude","SWEPT_FACE",FACE,{"disambiguationData":[OSD([sQuery(id+"F5.wireOp",EDGE,"E97")])]})]});
            var Q15;
            Q15=makeQuery(id+"F6.boolean.opBoolean","INTERSECT",EDGE,{"disambiguationData":[OD(1.0)],"derivedFrom":[makeQuery(id+"F1.opExtrude","SWEPT_FACE",FACE,{"disambiguationData":[OSD([sQuery(id+"F0.wireOp",EDGE,"E1")])]}),makeQuery(id+"F6.opExtrude","SWEPT_FACE",FACE,{"disambiguationData":[OSD([sQuery(id+"F5.wireOp",EDGE,"E98")])]})]});
            var Q16;
            {var subQ0=sQuery(id+"F5.wireOp",EDGE,"E125.6");Q16=makeQuery(id+"F6.boolean.opBoolean","INTERSECT",EDGE,{"disambiguationData":[OD(1.0)],"derivedFrom":[makeQuery(id+"F1.opExtrude","SWEPT_FACE",FACE,{"disambiguationData":[OSD([sQuery(id+"F0.wireOp",EDGE,"E1")])]}),makeQuery(id+"F6.opExtrude","SWEPT_FACE",FACE,{"disambiguationData":[OSD([subQ0]),TDD([makeQuery(id+"F5.imprint","IMPRINT",EDGE,{"disambiguationData":[TD([[makeQuery(id+"F5.imprint","INTERSECT",VERTEX,{"derivedFrom":[sQuery(id+"F5.wireOp",EDGE,"E125.2"),subQ0]}),-1.0]])],"derivedFrom":subQ0})])]})]});}
            var Q17;
            Q17=makeQuery(id+"F6.boolean.opBoolean","INTERSECT",EDGE,{"disambiguationData":[OD(1.0)],"derivedFrom":[makeQuery(id+"F1.opExtrude","SWEPT_FACE",FACE,{"disambiguationData":[OSD([sQuery(id+"F0.wireOp",EDGE,"E1")])]}),makeQuery(id+"F6.opExtrude","SWEPT_FACE",FACE,{"disambiguationData":[OSD([sQuery(id+"F5.wireOp",EDGE,"E81"),sQuery(id+"F5.wireOp",EDGE,"E128")])]})]});
            var Q18;
            {var subQ0=sQuery(id+"F5.wireOp",EDGE,"E125.2");Q18=makeQuery(id+"F6.boolean.opBoolean","INTERSECT",EDGE,{"disambiguationData":[OD(1.0)],"derivedFrom":[makeQuery(id+"F1.opExtrude","SWEPT_FACE",FACE,{"disambiguationData":[OSD([sQuery(id+"F0.wireOp",EDGE,"E1")])]}),makeQuery(id+"F6.opExtrude","SWEPT_FACE",FACE,{"disambiguationData":[OSD([subQ0]),TDD([makeQuery(id+"F5.imprint","IMPRINT",EDGE,{"disambiguationData":[TD([[makeQuery(id+"F5.imprint","INTERSECT",VERTEX,{"derivedFrom":[subQ0,sQuery(id+"F5.wireOp",EDGE,"E125.6")]}),1.0]])],"derivedFrom":subQ0})])]})]});}
            var Q19;
            Q19=makeQuery(id+"F6.boolean.opBoolean","INTERSECT",EDGE,{"disambiguationData":[OD(0.0)],"derivedFrom":[makeQuery(id+"F1.opExtrude","SWEPT_FACE",FACE,{"disambiguationData":[OSD([sQuery(id+"F0.wireOp",EDGE,"E1")])]}),makeQuery(id+"F6.opExtrude","SWEPT_FACE",FACE,{"disambiguationData":[OSD([sQuery(id+"F5.wireOp",EDGE,"E84.top")])]})]});
            var Q20;
            Q20=makeQuery(id+"F6.boolean.opBoolean","INTERSECT",EDGE,{"disambiguationData":[OD(0.0)],"derivedFrom":[makeQuery(id+"F1.opExtrude","SWEPT_FACE",FACE,{"disambiguationData":[OSD([sQuery(id+"F0.wireOp",EDGE,"E1")])]}),makeQuery(id+"F6.opExtrude","SWEPT_FACE",FACE,{"disambiguationData":[OSD([sQuery(id+"F5.wireOp",EDGE,"E84.left")])]})]});
            var Q21;
            {var subQ0=sQuery(id+"F5.wireOp",EDGE,"E125.2");Q21=makeQuery(id+"F6.boolean.opBoolean","INTERSECT",EDGE,{"disambiguationData":[OD(1.0)],"derivedFrom":[makeQuery(id+"F1.opExtrude","SWEPT_FACE",FACE,{"disambiguationData":[OSD([sQuery(id+"F0.wireOp",EDGE,"E1")])]}),makeQuery(id+"F6.opExtrude","SWEPT_FACE",FACE,{"disambiguationData":[OSD([subQ0]),TDD([makeQuery(id+"F5.imprint","IMPRINT",EDGE,{"disambiguationData":[TD([[makeQuery(id+"F5.imprint","INTERSECT",VERTEX,{"derivedFrom":[sQuery(id+"F5.wireOp",EDGE,"E125.1"),subQ0]}),-1.0]])],"derivedFrom":subQ0})])]})]});}
            var Q22;
            Q22=makeQuery(id+"F6.boolean.opBoolean","INTERSECT",EDGE,{"disambiguationData":[OD(1.0)],"derivedFrom":[makeQuery(id+"F1.opExtrude","SWEPT_FACE",FACE,{"disambiguationData":[OSD([sQuery(id+"F0.wireOp",EDGE,"E1")])]}),makeQuery(id+"F6.opExtrude","SWEPT_FACE",FACE,{"disambiguationData":[OSD([sQuery(id+"F5.wireOp",EDGE,"E123")])]})]});
            var Q23;
            Q23=makeQuery(id+"F6.boolean.opBoolean","INTERSECT",EDGE,{"disambiguationData":[OD(1.0)],"derivedFrom":[makeQuery(id+"F1.opExtrude","SWEPT_FACE",FACE,{"disambiguationData":[OSD([sQuery(id+"F0.wireOp",EDGE,"E1")])]}),makeQuery(id+"F6.opExtrude","SWEPT_FACE",FACE,{"disambiguationData":[OSD([sQuery(id+"F5.wireOp",EDGE,"E125.1")])]})]});
            var Q24;
            Q24=makeQuery(id+"F6.boolean.opBoolean","INTERSECT",EDGE,{"disambiguationData":[OD(1.0)],"derivedFrom":[makeQuery(id+"F1.opExtrude","SWEPT_FACE",FACE,{"disambiguationData":[OSD([sQuery(id+"F0.wireOp",EDGE,"E1")])]}),makeQuery(id+"F6.opExtrude","SWEPT_FACE",FACE,{"disambiguationData":[OSD([sQuery(id+"F5.wireOp",EDGE,"E125.0")])]})]});
            var Q25;
            Q25=makeQuery(id+"F6.boolean.opBoolean","INTERSECT",EDGE,{"disambiguationData":[OD(0.0)],"derivedFrom":[makeQuery(id+"F1.opExtrude","SWEPT_FACE",FACE,{"disambiguationData":[OSD([sQuery(id+"F0.wireOp",EDGE,"E1")])]}),makeQuery(id+"F6.opExtrude","SWEPT_FACE",FACE,{"disambiguationData":[OSD([sQuery(id+"F5.wireOp",EDGE,"E120.1")])]})]});
            var Q26;
            Q26=makeQuery(id+"F6.boolean.opBoolean","INTERSECT",EDGE,{"disambiguationData":[OD(0.0)],"derivedFrom":[makeQuery(id+"F1.opExtrude","SWEPT_FACE",FACE,{"disambiguationData":[OSD([sQuery(id+"F0.wireOp",EDGE,"E1")])]}),makeQuery(id+"F6.opExtrude","SWEPT_FACE",FACE,{"disambiguationData":[OSD([sQuery(id+"F5.wireOp",EDGE,"E120.2")])]})]});
            var Q27;
            Q27=makeQuery(id+"F6.boolean.opBoolean","INTERSECT",EDGE,{"disambiguationData":[OD(0.0)],"derivedFrom":[makeQuery(id+"F1.opExtrude","SWEPT_FACE",FACE,{"disambiguationData":[OSD([sQuery(id+"F0.wireOp",EDGE,"E1")])]}),makeQuery(id+"F6.opExtrude","SWEPT_FACE",FACE,{"disambiguationData":[OSD([sQuery(id+"F5.wireOp",EDGE,"E120.0")])]})]});
            var Q28;
            Q28=makeQuery(id+"F6.boolean.opBoolean","INTERSECT",EDGE,{"disambiguationData":[OD(0.0)],"derivedFrom":[makeQuery(id+"F1.opExtrude","SWEPT_FACE",FACE,{"disambiguationData":[OSD([sQuery(id+"F0.wireOp",EDGE,"E1")])]}),makeQuery(id+"F6.opExtrude","SWEPT_FACE",FACE,{"disambiguationData":[OSD([sQuery(id+"F5.wireOp",EDGE,"E84.bottom")])]})]});
            var Q29;
            Q29=makeQuery(id+"F6.boolean.opBoolean","INTERSECT",EDGE,{"disambiguationData":[OD(0.0)],"derivedFrom":[makeQuery(id+"F1.opExtrude","SWEPT_FACE",FACE,{"disambiguationData":[OSD([sQuery(id+"F0.wireOp",EDGE,"E1")])]}),makeQuery(id+"F6.opExtrude","SWEPT_FACE",FACE,{"disambiguationData":[OSD([sQuery(id+"F5.wireOp",EDGE,"E84.right")])]})]});
            var Q30;
            Q30=makeQuery(id+"F6.boolean.opBoolean","INTERSECT",EDGE,{"disambiguationData":[OD(0.0)],"derivedFrom":[makeQuery(id+"F1.opExtrude","SWEPT_FACE",FACE,{"disambiguationData":[OSD([sQuery(id+"F0.wireOp",EDGE,"E1")])]}),makeQuery(id+"F6.opExtrude","SWEPT_FACE",FACE,{"disambiguationData":[OSD([sQuery(id+"F5.wireOp",EDGE,"E85.top")])]})]});
            var Q31;
            Q31=makeQuery(id+"F6.boolean.opBoolean","INTERSECT",EDGE,{"disambiguationData":[OD(0.0)],"derivedFrom":[makeQuery(id+"F1.opExtrude","SWEPT_FACE",FACE,{"disambiguationData":[OSD([sQuery(id+"F0.wireOp",EDGE,"E1")])]}),makeQuery(id+"F6.opExtrude","SWEPT_FACE",FACE,{"disambiguationData":[OSD([sQuery(id+"F5.wireOp",EDGE,"E85.left")])]})]});
            var Q32;
            Q32=makeQuery(id+"F6.boolean.opBoolean","INTERSECT",EDGE,{"disambiguationData":[OD(0.0)],"derivedFrom":[makeQuery(id+"F1.opExtrude","SWEPT_FACE",FACE,{"disambiguationData":[OSD([sQuery(id+"F0.wireOp",EDGE,"E1")])]}),makeQuery(id+"F6.opExtrude","SWEPT_FACE",FACE,{"disambiguationData":[OSD([sQuery(id+"F5.wireOp",EDGE,"E85.right")])]})]});
            var Q33;
            Q33=makeQuery(id+"F6.boolean.opBoolean","INTERSECT",EDGE,{"disambiguationData":[OD(0.0)],"derivedFrom":[makeQuery(id+"F1.opExtrude","SWEPT_FACE",FACE,{"disambiguationData":[OSD([sQuery(id+"F0.wireOp",EDGE,"E1")])]}),makeQuery(id+"F6.opExtrude","SWEPT_FACE",FACE,{"disambiguationData":[OSD([sQuery(id+"F5.wireOp",EDGE,"E86.right")])]})]});
            var Q34;
            Q34=makeQuery(id+"F6.boolean.opBoolean","INTERSECT",EDGE,{"disambiguationData":[OD(0.0)],"derivedFrom":[makeQuery(id+"F1.opExtrude","SWEPT_FACE",FACE,{"disambiguationData":[OSD([sQuery(id+"F0.wireOp",EDGE,"E1")])]}),makeQuery(id+"F6.opExtrude","SWEPT_FACE",FACE,{"disambiguationData":[OSD([sQuery(id+"F5.wireOp",EDGE,"E86.top")])]})]});
            var Q35;
            Q35=makeQuery(id+"F6.boolean.opBoolean","INTERSECT",EDGE,{"disambiguationData":[OD(0.0)],"derivedFrom":[makeQuery(id+"F1.opExtrude","SWEPT_FACE",FACE,{"disambiguationData":[OSD([sQuery(id+"F0.wireOp",EDGE,"E1")])]}),makeQuery(id+"F6.opExtrude","SWEPT_FACE",FACE,{"disambiguationData":[OSD([sQuery(id+"F5.wireOp",EDGE,"E88")])]})]});
            var Q36;
            Q36=makeQuery(id+"F6.boolean.opBoolean","INTERSECT",EDGE,{"disambiguationData":[OD(0.0)],"derivedFrom":[makeQuery(id+"F1.opExtrude","SWEPT_FACE",FACE,{"disambiguationData":[OSD([sQuery(id+"F0.wireOp",EDGE,"E1")])]}),makeQuery(id+"F6.opExtrude","SWEPT_FACE",FACE,{"disambiguationData":[OSD([sQuery(id+"F5.wireOp",EDGE,"E85.bottom")])]})]});
            var Q37;
            Q37=makeQuery(id+"F6.boolean.opBoolean","INTERSECT",EDGE,{"disambiguationData":[OD(0.0)],"derivedFrom":[makeQuery(id+"F1.opExtrude","SWEPT_FACE",FACE,{"disambiguationData":[OSD([sQuery(id+"F0.wireOp",EDGE,"E1")])]}),makeQuery(id+"F6.opExtrude","SWEPT_FACE",FACE,{"disambiguationData":[OSD([sQuery(id+"F5.wireOp",EDGE,"E89")])]})]});
            var Q38;
            Q38=makeQuery(id+"F6.boolean.opBoolean","INTERSECT",EDGE,{"disambiguationData":[OD(0.0)],"derivedFrom":[makeQuery(id+"F1.opExtrude","SWEPT_FACE",FACE,{"disambiguationData":[OSD([sQuery(id+"F0.wireOp",EDGE,"E1")])]}),makeQuery(id+"F6.opExtrude","SWEPT_FACE",FACE,{"disambiguationData":[OSD([sQuery(id+"F5.wireOp",EDGE,"E87.bottom")])]})]});
            var Q39;
            {var subQ0=sQuery(id+"F5.wireOp",EDGE,"E125.6");Q39=makeQuery(id+"F6.boolean.opBoolean","INTERSECT",EDGE,{"disambiguationData":[OD(1.0)],"derivedFrom":[makeQuery(id+"F1.opExtrude","SWEPT_FACE",FACE,{"disambiguationData":[OSD([sQuery(id+"F0.wireOp",EDGE,"E1")])]}),makeQuery(id+"F6.opExtrude","SWEPT_FACE",FACE,{"disambiguationData":[OSD([subQ0]),TDD([makeQuery(id+"F5.imprint","IMPRINT",EDGE,{"disambiguationData":[TD([[makeQuery(id+"F5.imprint","INTERSECT",VERTEX,{"derivedFrom":[sQuery(id+"F5.wireOp",EDGE,"E125.5"),subQ0]}),1.0]])],"derivedFrom":subQ0})])]})]});}
            var Q40;
            {var subQ0=sQuery(id+"F5.wireOp",EDGE,"E125.5");Q40=makeQuery(id+"F6.boolean.opBoolean","INTERSECT",EDGE,{"disambiguationData":[OD(1.0)],"derivedFrom":[makeQuery(id+"F1.opExtrude","SWEPT_FACE",FACE,{"disambiguationData":[OSD([sQuery(id+"F0.wireOp",EDGE,"E1")])]}),makeQuery(id+"F6.opExtrude","SWEPT_FACE",FACE,{"disambiguationData":[OSD([subQ0]),TDD([makeQuery(id+"F5.imprint","IMPRINT",EDGE,{"disambiguationData":[TD([[makeQuery(id+"F5.imprint","INTERSECT",VERTEX,{"derivedFrom":[subQ0,sQuery(id+"F5.wireOp",EDGE,"E125.6")]}),-1.0]])],"derivedFrom":subQ0})])]})]});}
            var Q41;
            Q41=makeQuery(id+"F6.boolean.opBoolean","INTERSECT",EDGE,{"disambiguationData":[OD(1.0)],"derivedFrom":[makeQuery(id+"F1.opExtrude","SWEPT_FACE",FACE,{"disambiguationData":[OSD([sQuery(id+"F0.wireOp",EDGE,"E1")])]}),makeQuery(id+"F6.opExtrude","SWEPT_FACE",FACE,{"disambiguationData":[OSD([sQuery(id+"F5.wireOp",EDGE,"E83"),sQuery(id+"F5.wireOp",EDGE,"E129")])]})]});
            var Q42;
            Q42=makeQuery(id+"F6.boolean.opBoolean","INTERSECT",EDGE,{"disambiguationData":[OD(0.0)],"derivedFrom":[makeQuery(id+"F1.opExtrude","SWEPT_FACE",FACE,{"disambiguationData":[OSD([sQuery(id+"F0.wireOp",EDGE,"E1")])]}),makeQuery(id+"F6.opExtrude","SWEPT_FACE",FACE,{"disambiguationData":[OSD([sQuery(id+"F5.wireOp",EDGE,"E87.right")])]})]});
            var Q43;
            Q43=makeQuery(id+"F6.boolean.opBoolean","INTERSECT",EDGE,{"disambiguationData":[OD(0.0)],"derivedFrom":[makeQuery(id+"F1.opExtrude","SWEPT_FACE",FACE,{"disambiguationData":[OSD([sQuery(id+"F0.wireOp",EDGE,"E1")])]}),makeQuery(id+"F6.opExtrude","SWEPT_FACE",FACE,{"disambiguationData":[OSD([sQuery(id+"F5.wireOp",EDGE,"E87.left")])]})]});
            var Q44;
            Q44=makeQuery(id+"F6.boolean.opBoolean","INTERSECT",EDGE,{"disambiguationData":[OD(0.0)],"derivedFrom":[makeQuery(id+"F1.opExtrude","SWEPT_FACE",FACE,{"disambiguationData":[OSD([sQuery(id+"F0.wireOp",EDGE,"E1")])]}),makeQuery(id+"F6.opExtrude","SWEPT_FACE",FACE,{"disambiguationData":[OSD([sQuery(id+"F5.wireOp",EDGE,"E87.top")])]})]});
            var Q45;
            Q45=makeQuery(id+"F6.boolean.opBoolean","INTERSECT",EDGE,{"disambiguationData":[OD(0.0)],"derivedFrom":[makeQuery(id+"F1.opExtrude","SWEPT_FACE",FACE,{"disambiguationData":[OSD([sQuery(id+"F0.wireOp",EDGE,"E1")])]}),makeQuery(id+"F6.opExtrude","SWEPT_FACE",FACE,{"disambiguationData":[OSD([sQuery(id+"F5.wireOp",EDGE,"E121.0")])]})]});
            var Q46;
            Q46=makeQuery(id+"F6.boolean.opBoolean","INTERSECT",EDGE,{"disambiguationData":[OD(0.0)],"derivedFrom":[makeQuery(id+"F1.opExtrude","SWEPT_FACE",FACE,{"disambiguationData":[OSD([sQuery(id+"F0.wireOp",EDGE,"E1")])]}),makeQuery(id+"F6.opExtrude","SWEPT_FACE",FACE,{"disambiguationData":[OSD([sQuery(id+"F5.wireOp",EDGE,"E121.1")])]})]});
            var Q47;
            Q47=makeQuery(id+"F6.boolean.opBoolean","INTERSECT",EDGE,{"disambiguationData":[OD(0.0)],"derivedFrom":[makeQuery(id+"F1.opExtrude","SWEPT_FACE",FACE,{"disambiguationData":[OSD([sQuery(id+"F0.wireOp",EDGE,"E1")])]}),makeQuery(id+"F6.opExtrude","SWEPT_FACE",FACE,{"disambiguationData":[OSD([sQuery(id+"F5.wireOp",EDGE,"E121.2")])]})]});
            var Q48;
            Q48=makeQuery(id+"F6.boolean.opBoolean","INTERSECT",EDGE,{"disambiguationData":[OD(1.0)],"derivedFrom":[makeQuery(id+"F1.opExtrude","SWEPT_FACE",FACE,{"disambiguationData":[OSD([sQuery(id+"F0.wireOp",EDGE,"E1")])]}),makeQuery(id+"F6.opExtrude","SWEPT_FACE",FACE,{"disambiguationData":[OSD([sQuery(id+"F5.wireOp",EDGE,"E124")])]})]});
            var Q49;
            Q49=makeQuery(id+"F6.boolean.opBoolean","INTERSECT",EDGE,{"disambiguationData":[OD(1.0)],"derivedFrom":[makeQuery(id+"F1.opExtrude","SWEPT_FACE",FACE,{"disambiguationData":[OSD([sQuery(id+"F0.wireOp",EDGE,"E1")])]}),makeQuery(id+"F6.opExtrude","SWEPT_FACE",FACE,{"disambiguationData":[OSD([sQuery(id+"F5.wireOp",EDGE,"E125.4")])]})]});
            var Q50;
            {var subQ0=sQuery(id+"F5.wireOp",EDGE,"E125.5");Q50=makeQuery(id+"F6.boolean.opBoolean","INTERSECT",EDGE,{"disambiguationData":[OD(1.0)],"derivedFrom":[makeQuery(id+"F1.opExtrude","SWEPT_FACE",FACE,{"disambiguationData":[OSD([sQuery(id+"F0.wireOp",EDGE,"E1")])]}),makeQuery(id+"F6.opExtrude","SWEPT_FACE",FACE,{"disambiguationData":[OSD([subQ0]),TDD([makeQuery(id+"F5.imprint","IMPRINT",EDGE,{"disambiguationData":[TD([[makeQuery(id+"F5.imprint","INTERSECT",VERTEX,{"derivedFrom":[sQuery(id+"F5.wireOp",EDGE,"E125.4"),subQ0]}),1.0]])],"derivedFrom":subQ0})])]})]});}
            var Q51;
            Q51=makeQuery(id+"F6.boolean.opBoolean","INTERSECT",EDGE,{"disambiguationData":[OD(1.0)],"derivedFrom":[makeQuery(id+"F1.opExtrude","SWEPT_FACE",FACE,{"disambiguationData":[OSD([sQuery(id+"F0.wireOp",EDGE,"E1")])]}),makeQuery(id+"F6.opExtrude","SWEPT_FACE",FACE,{"disambiguationData":[OSD([sQuery(id+"F5.wireOp",EDGE,"E125.3")])]})]});
            var Q52;
            Q52=makeQuery(id+"F6.boolean.opBoolean","INTERSECT",EDGE,{"disambiguationData":[OD(0.0)],"derivedFrom":[makeQuery(id+"F1.opExtrude","SWEPT_FACE",FACE,{"disambiguationData":[OSD([sQuery(id+"F0.wireOp",EDGE,"E1")])]}),makeQuery(id+"F6.opExtrude","SWEPT_FACE",FACE,{"disambiguationData":[OSD([sQuery(id+"F5.wireOp",EDGE,"E122.1")])]})]});
            var Q53;
            Q53=makeQuery(id+"F6.boolean.opBoolean","INTERSECT",EDGE,{"disambiguationData":[OD(0.0)],"derivedFrom":[makeQuery(id+"F1.opExtrude","SWEPT_FACE",FACE,{"disambiguationData":[OSD([sQuery(id+"F0.wireOp",EDGE,"E1")])]}),makeQuery(id+"F6.opExtrude","SWEPT_FACE",FACE,{"disambiguationData":[OSD([sQuery(id+"F5.wireOp",EDGE,"E122.0")])]})]});
            var Q54;
            Q54=makeQuery(id+"F6.boolean.opBoolean","INTERSECT",EDGE,{"disambiguationData":[OD(0.0)],"derivedFrom":[makeQuery(id+"F1.opExtrude","SWEPT_FACE",FACE,{"disambiguationData":[OSD([sQuery(id+"F0.wireOp",EDGE,"E1")])]}),makeQuery(id+"F6.opExtrude","SWEPT_FACE",FACE,{"disambiguationData":[OSD([sQuery(id+"F5.wireOp",EDGE,"E122.2")])]})]});
            var Q55;
            {var subQ0=sQuery(id+"F5.wireOp",EDGE,"E116.MirrorCS");Q55=makeQuery(id+"F6.boolean.opBoolean","INTERSECT",EDGE,{"disambiguationData":[OD(1.0)],"derivedFrom":[makeQuery(id+"F1.opExtrude","SWEPT_FACE",FACE,{"disambiguationData":[OSD([sQuery(id+"F0.wireOp",EDGE,"E1")])]}),makeQuery(id+"F6.opExtrude","SWEPT_FACE",FACE,{"disambiguationData":[OSD([subQ0]),TDD([makeQuery(id+"F5.imprint","IMPRINT",EDGE,{"disambiguationData":[TD([[makeQuery(id+"F5.imprint","INTERSECT",VERTEX,{"derivedFrom":[sQuery(id+"F5.wireOp",EDGE,"E110.MirrorCS"),subQ0]}),1.0]])],"derivedFrom":subQ0})])]})]});}
            var Q56;
            {var subQ0=sQuery(id+"F5.wireOp",EDGE,"E117.0");Q56=makeQuery(id+"F6.boolean.opBoolean","INTERSECT",EDGE,{"disambiguationData":[OD(1.0)],"derivedFrom":[makeQuery(id+"F1.opExtrude","SWEPT_FACE",FACE,{"disambiguationData":[OSD([sQuery(id+"F0.wireOp",EDGE,"E1")])]}),makeQuery(id+"F6.opExtrude","SWEPT_FACE",FACE,{"disambiguationData":[OSD([subQ0]),TDD([makeQuery(id+"F5.imprint","IMPRINT",EDGE,{"disambiguationData":[TD([[makeQuery(id+"F5.imprint","INTERSECT",VERTEX,{"derivedFrom":[sQuery(id+"F5.wireOp",EDGE,"E109.MirrorCS"),subQ0]}),-1.0]])],"derivedFrom":subQ0})])]})]});}
            var Q57;
            Q57=makeQuery(id+"F6.boolean.opBoolean","INTERSECT",EDGE,{"disambiguationData":[OD(1.0)],"derivedFrom":[makeQuery(id+"F1.opExtrude","SWEPT_FACE",FACE,{"disambiguationData":[OSD([sQuery(id+"F0.wireOp",EDGE,"E1")])]}),makeQuery(id+"F6.opExtrude","SWEPT_FACE",FACE,{"disambiguationData":[OSD([sQuery(id+"F5.wireOp",EDGE,"E112.MirrorCS")])]})]});
            var Q58;
            Q58=makeQuery(id+"F6.boolean.opBoolean","INTERSECT",EDGE,{"disambiguationData":[OD(1.0)],"derivedFrom":[makeQuery(id+"F1.opExtrude","SWEPT_FACE",FACE,{"disambiguationData":[OSD([sQuery(id+"F0.wireOp",EDGE,"E1")])]}),makeQuery(id+"F6.opExtrude","SWEPT_FACE",FACE,{"disambiguationData":[OSD([sQuery(id+"F5.wireOp",EDGE,"E110.MirrorCS")])]})]});
            var Q59;
            Q59=makeQuery(id+"F6.boolean.opBoolean","INTERSECT",EDGE,{"disambiguationData":[OD(1.0)],"derivedFrom":[makeQuery(id+"F1.opExtrude","SWEPT_FACE",FACE,{"disambiguationData":[OSD([sQuery(id+"F0.wireOp",EDGE,"E1")])]}),makeQuery(id+"F6.opExtrude","SWEPT_FACE",FACE,{"disambiguationData":[OSD([sQuery(id+"F5.wireOp",EDGE,"E115.MirrorCS")])]})]});
            var Q60;
            Q60=makeQuery(id+"F6.boolean.opBoolean","INTERSECT",EDGE,{"disambiguationData":[OD(1.0)],"derivedFrom":[makeQuery(id+"F1.opExtrude","SWEPT_FACE",FACE,{"disambiguationData":[OSD([sQuery(id+"F0.wireOp",EDGE,"E1")])]}),makeQuery(id+"F6.opExtrude","SWEPT_FACE",FACE,{"disambiguationData":[OSD([sQuery(id+"F5.wireOp",EDGE,"E119.0")])]})]});
            var Q61;
            Q61=makeQuery(id+"F6.boolean.opBoolean","INTERSECT",EDGE,{"disambiguationData":[OD(1.0)],"derivedFrom":[makeQuery(id+"F1.opExtrude","SWEPT_FACE",FACE,{"disambiguationData":[OSD([sQuery(id+"F0.wireOp",EDGE,"E1")])]}),makeQuery(id+"F6.opExtrude","SWEPT_FACE",FACE,{"disambiguationData":[OSD([sQuery(id+"F5.wireOp",EDGE,"E114.MirrorCS")])]})]});
            var Q62;
            Q62=makeQuery(id+"F6.boolean.opBoolean","INTERSECT",EDGE,{"disambiguationData":[OD(1.0)],"derivedFrom":[makeQuery(id+"F1.opExtrude","SWEPT_FACE",FACE,{"disambiguationData":[OSD([sQuery(id+"F0.wireOp",EDGE,"E1")])]}),makeQuery(id+"F6.opExtrude","SWEPT_FACE",FACE,{"disambiguationData":[OSD([sQuery(id+"F5.wireOp",EDGE,"E113.MirrorCS")])]})]});
            var Q63;
            Q63=makeQuery(id+"F6.boolean.opBoolean","INTERSECT",EDGE,{"disambiguationData":[OD(1.0)],"derivedFrom":[makeQuery(id+"F1.opExtrude","SWEPT_FACE",FACE,{"disambiguationData":[OSD([sQuery(id+"F0.wireOp",EDGE,"E1")])]}),makeQuery(id+"F6.opExtrude","SWEPT_FACE",FACE,{"disambiguationData":[OSD([sQuery(id+"F5.wireOp",EDGE,"E111.MirrorCS")])]})]});
            var Q64;
            {var subQ0=sQuery(id+"F5.wireOp",EDGE,"E116.MirrorCS");Q64=makeQuery(id+"F6.boolean.opBoolean","INTERSECT",EDGE,{"disambiguationData":[OD(1.0)],"derivedFrom":[makeQuery(id+"F1.opExtrude","SWEPT_FACE",FACE,{"disambiguationData":[OSD([sQuery(id+"F0.wireOp",EDGE,"E1")])]}),makeQuery(id+"F6.opExtrude","SWEPT_FACE",FACE,{"disambiguationData":[OSD([subQ0]),TDD([makeQuery(id+"F5.imprint","IMPRINT",EDGE,{"disambiguationData":[TD([[makeQuery(id+"F5.imprint","INTERSECT",VERTEX,{"derivedFrom":[sQuery(id+"F5.wireOp",EDGE,"E111.MirrorCS"),subQ0]}),1.0]])],"derivedFrom":subQ0})])]})]});}
            var Q65;
            Q65=makeQuery(id+"F6.boolean.opBoolean","INTERSECT",EDGE,{"disambiguationData":[OD(1.0)],"derivedFrom":[makeQuery(id+"F1.opExtrude","SWEPT_FACE",FACE,{"disambiguationData":[OSD([sQuery(id+"F0.wireOp",EDGE,"E1")])]}),makeQuery(id+"F6.opExtrude","SWEPT_FACE",FACE,{"disambiguationData":[OSD([sQuery(id+"F5.wireOp",EDGE,"E109.MirrorCS")])]})]});
            var Q66;
            Q66=makeQuery(id+"F6.boolean.opBoolean","INTERSECT",EDGE,{"disambiguationData":[OD(1.0)],"derivedFrom":[makeQuery(id+"F1.opExtrude","SWEPT_FACE",FACE,{"disambiguationData":[OSD([sQuery(id+"F0.wireOp",EDGE,"E1")])]}),makeQuery(id+"F6.opExtrude","SWEPT_FACE",FACE,{"disambiguationData":[OSD([sQuery(id+"F5.wireOp",EDGE,"E118.0")])]})]});
            var Q67;
            Q67=makeQuery(id+"F6.boolean.opBoolean","INTERSECT",EDGE,{"disambiguationData":[OD(1.0)],"derivedFrom":[makeQuery(id+"F1.opExtrude","SWEPT_FACE",FACE,{"disambiguationData":[OSD([sQuery(id+"F0.wireOp",EDGE,"E1")])]}),makeQuery(id+"F6.opExtrude","SWEPT_FACE",FACE,{"disambiguationData":[OSD([sQuery(id+"F5.wireOp",EDGE,"E106.MirrorCS")])]})]});
            var Q68;
            Q68=makeQuery(id+"F6.boolean.opBoolean","INTERSECT",EDGE,{"disambiguationData":[OD(1.0)],"derivedFrom":[makeQuery(id+"F1.opExtrude","SWEPT_FACE",FACE,{"disambiguationData":[OSD([sQuery(id+"F0.wireOp",EDGE,"E1")])]}),makeQuery(id+"F6.opExtrude","SWEPT_FACE",FACE,{"disambiguationData":[OSD([sQuery(id+"F5.wireOp",EDGE,"E107.MirrorCS")])]})]});
            var Q69;
            Q69=makeQuery(id+"F6.boolean.opBoolean","INTERSECT",EDGE,{"disambiguationData":[OD(1.0)],"derivedFrom":[makeQuery(id+"F1.opExtrude","SWEPT_FACE",FACE,{"disambiguationData":[OSD([sQuery(id+"F0.wireOp",EDGE,"E1")])]}),makeQuery(id+"F6.opExtrude","SWEPT_FACE",FACE,{"disambiguationData":[OSD([sQuery(id+"F5.wireOp",EDGE,"E108.MirrorCS")])]})]});
            var Q70;
            {var subQ0=sQuery(id+"F5.wireOp",EDGE,"E117.0");Q70=makeQuery(id+"F6.boolean.opBoolean","INTERSECT",EDGE,{"disambiguationData":[OD(1.0)],"derivedFrom":[makeQuery(id+"F1.opExtrude","SWEPT_FACE",FACE,{"disambiguationData":[OSD([sQuery(id+"F0.wireOp",EDGE,"E1")])]}),makeQuery(id+"F6.opExtrude","SWEPT_FACE",FACE,{"disambiguationData":[OSD([subQ0]),TDD([makeQuery(id+"F5.imprint","IMPRINT",EDGE,{"disambiguationData":[TD([[makeQuery(id+"F5.imprint","INTERSECT",VERTEX,{"derivedFrom":[sQuery(id+"F5.wireOp",EDGE,"E108.MirrorCS"),subQ0]}),1.0]])],"derivedFrom":subQ0})])]})]});}
            fillet(context, id + "F18", {"entities" : qUnion([Q0, Q1, Q2, Q3, Q4, Q5, Q6, Q7, Q8, Q9, Q10, Q11, Q12, Q13, Q14, Q15, Q16, Q17, Q18, Q19, Q20, Q21, Q22, Q23, Q24, Q25, Q26, Q27, Q28, Q29, Q30, Q31, Q32, Q33, Q34, Q35, Q36, Q37, Q38, Q39, Q40, Q41, Q42, Q43, Q44, Q45, Q46, Q47, Q48, Q49, Q50, Q51, Q52, Q53, Q54, Q55, Q56, Q57, Q58, Q59, Q60, Q61, Q62, Q63, Q64, Q65, Q66, Q67, Q68, Q69, Q70]), "radius" : 0.1 * mm, "tangentPropagation" : true, "allowEdgeOverflow" : false});
        }
    });
